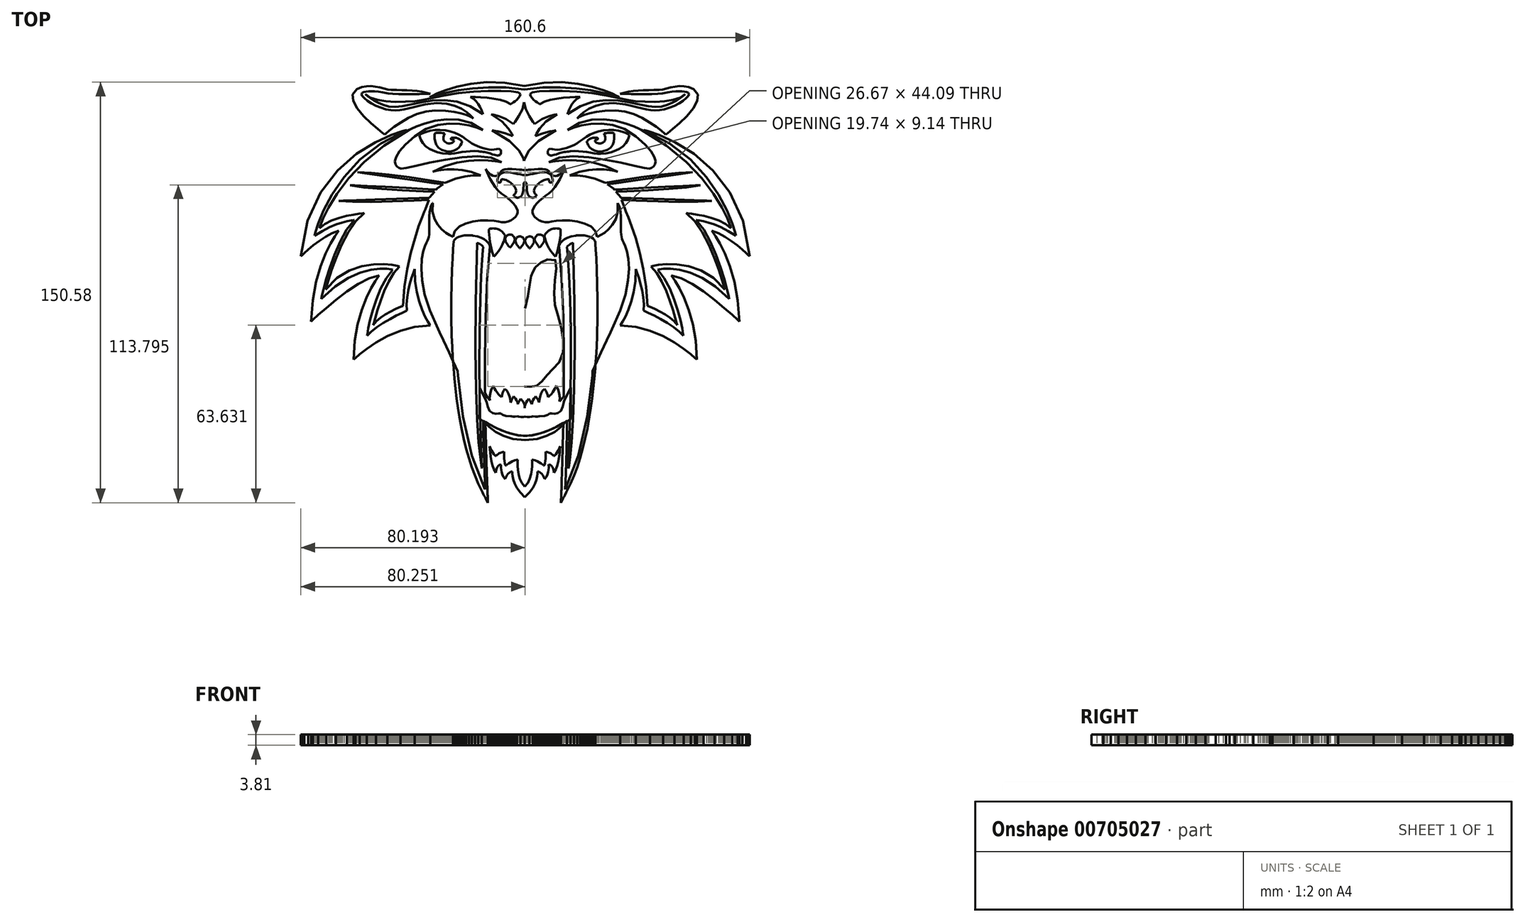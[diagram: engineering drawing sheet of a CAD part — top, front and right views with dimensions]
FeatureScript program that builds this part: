
annotation { "Feature Type Name" : "Feature", "Feature Type Description" : "" }
export const myFeature = defineFeature(function(context is Context, id is Id, definition is map)
    precondition{}
    {
        {
            var Q0;
            Q0=qCreatedBy(makeId("Top.planeOp"),FACE);
            var sketch = newSketch(context, id + "F0", { "sketchPlane" : qUnion([Q0])});
            skLineSegment(sketch, "E0", {"start": v(12.77, -75.29) * mm, "end": v(12.8, -74.69) * mm});
            skLineSegment(sketch, "E1", {"start": v(12.8, -74.69) * mm, "end": v(12.82, -74.1) * mm});
            skLineSegment(sketch, "E2", {"start": v(12.82, -74.1) * mm, "end": v(12.84, -73.5) * mm});
            skLineSegment(sketch, "E3", {"start": v(12.84, -73.5) * mm, "end": v(12.87, -72.9) * mm});
            skLineSegment(sketch, "E4", {"start": v(12.87, -72.9) * mm, "end": v(12.9, -72.3) * mm});
            skLineSegment(sketch, "E5", {"start": v(12.9, -72.3) * mm, "end": v(12.92, -71.7) * mm});
            skLineSegment(sketch, "E6", {"start": v(12.92, -71.7) * mm, "end": v(12.94, -71.1) * mm});
            skLineSegment(sketch, "E7", {"start": v(12.94, -71.1) * mm, "end": v(12.97, -70.5) * mm});
            skLineSegment(sketch, "E8", {"start": v(12.97, -70.5) * mm, "end": v(13.08, -67.74) * mm});
            skLineSegment(sketch, "E9", {"start": v(13.08, -67.74) * mm, "end": v(13.31, -60.6) * mm});
            skLineSegment(sketch, "E10", {"start": v(13.31, -60.6) * mm, "end": v(13.58, -50.1) * mm});
            skLineSegment(sketch, "E11", {"start": v(13.58, -50.1) * mm, "end": v(13.79, -37.28) * mm});
            skLineSegment(sketch, "E12", {"start": v(13.79, -37.28) * mm, "end": v(13.84, -23.18) * mm});
            skLineSegment(sketch, "E13", {"start": v(13.84, -23.18) * mm, "end": v(13.63, -8.86) * mm});
            skLineSegment(sketch, "E14", {"start": v(13.63, -8.86) * mm, "end": v(13.07, 4.68) * mm});
            skLineSegment(sketch, "E15", {"start": v(13.07, 4.68) * mm, "end": v(12.07, 16.37) * mm});
            skLineSegment(sketch, "E16", {"start": v(12.07, 16.37) * mm, "end": v(12.06, 16.4) * mm});
            skLineSegment(sketch, "E17", {"start": v(12.06, 16.4) * mm, "end": v(12.06, 16.43) * mm});
            skLineSegment(sketch, "E18", {"start": v(12.06, 16.43) * mm, "end": v(12.06, 16.46) * mm});
            skLineSegment(sketch, "E19", {"start": v(12.06, 16.46) * mm, "end": v(12.05, 16.49) * mm});
            skLineSegment(sketch, "E20", {"start": v(12.05, 16.49) * mm, "end": v(12.05, 16.52) * mm});
            skLineSegment(sketch, "E21", {"start": v(12.05, 16.52) * mm, "end": v(12.04, 16.54) * mm});
            skLineSegment(sketch, "E22", {"start": v(12.04, 16.54) * mm, "end": v(12.04, 16.57) * mm});
            skLineSegment(sketch, "E23", {"start": v(12.04, 16.57) * mm, "end": v(12.04, 16.6) * mm});
            skLineSegment(sketch, "E24", {"start": v(12.04, 16.6) * mm, "end": v(12.05, 16.63) * mm});
            skLineSegment(sketch, "E25", {"start": v(12.05, 16.63) * mm, "end": v(12.06, 16.66) * mm});
            skLineSegment(sketch, "E26", {"start": v(12.06, 16.66) * mm, "end": v(12.06, 16.69) * mm});
            skLineSegment(sketch, "E27", {"start": v(12.06, 16.69) * mm, "end": v(12.07, 16.71) * mm});
            skLineSegment(sketch, "E28", {"start": v(12.07, 16.71) * mm, "end": v(12.08, 16.74) * mm});
            skLineSegment(sketch, "E29", {"start": v(12.08, 16.74) * mm, "end": v(12.1, 16.77) * mm});
            skLineSegment(sketch, "E30", {"start": v(12.1, 16.77) * mm, "end": v(12.1, 16.8) * mm});
            skLineSegment(sketch, "E31", {"start": v(12.1, 16.8) * mm, "end": v(12.1, 16.82) * mm});
            skLineSegment(sketch, "E32", {"start": v(12.1, 16.82) * mm, "end": v(12.2, 17.03) * mm});
            skLineSegment(sketch, "E33", {"start": v(12.2, 17.03) * mm, "end": v(12.4, 17.4) * mm});
            skLineSegment(sketch, "E34", {"start": v(12.4, 17.4) * mm, "end": v(12.74, 17.88) * mm});
            skLineSegment(sketch, "E35", {"start": v(12.74, 17.88) * mm, "end": v(13.29, 18.43) * mm});
            skLineSegment(sketch, "E36", {"start": v(13.29, 18.43) * mm, "end": v(14.06, 19) * mm});
            skLineSegment(sketch, "E37", {"start": v(14.06, 19) * mm, "end": v(15.09, 19.54) * mm});
            skLineSegment(sketch, "E38", {"start": v(15.09, 19.54) * mm, "end": v(16.42, 20) * mm});
            skLineSegment(sketch, "E39", {"start": v(16.42, 20) * mm, "end": v(18.09, 20.35) * mm});
            skLineSegment(sketch, "E40", {"start": v(18.09, 20.35) * mm, "end": v(18.34, 20.38) * mm});
            skLineSegment(sketch, "E41", {"start": v(18.34, 20.38) * mm, "end": v(18.6, 20.41) * mm});
            skLineSegment(sketch, "E42", {"start": v(18.6, 20.41) * mm, "end": v(18.84, 20.44) * mm});
            skLineSegment(sketch, "E43", {"start": v(18.84, 20.44) * mm, "end": v(19.08, 20.46) * mm});
            skLineSegment(sketch, "E44", {"start": v(19.08, 20.46) * mm, "end": v(19.32, 20.47) * mm});
            skLineSegment(sketch, "E45", {"start": v(19.32, 20.47) * mm, "end": v(19.56, 20.49) * mm});
            skLineSegment(sketch, "E46", {"start": v(19.56, 20.49) * mm, "end": v(19.8, 20.5) * mm});
            skLineSegment(sketch, "E47", {"start": v(19.8, 20.5) * mm, "end": v(20.02, 20.5) * mm});
            skLineSegment(sketch, "E48", {"start": v(20.02, 20.5) * mm, "end": v(21.18, 20.43) * mm});
            skLineSegment(sketch, "E49", {"start": v(21.18, 20.43) * mm, "end": v(22.18, 20.25) * mm});
            skLineSegment(sketch, "E50", {"start": v(22.18, 20.25) * mm, "end": v(23.03, 19.98) * mm});
            skLineSegment(sketch, "E51", {"start": v(23.03, 19.98) * mm, "end": v(23.74, 19.63) * mm});
            skLineSegment(sketch, "E52", {"start": v(23.74, 19.63) * mm, "end": v(24.29, 19.24) * mm});
            skLineSegment(sketch, "E53", {"start": v(24.29, 19.24) * mm, "end": v(24.69, 18.83) * mm});
            skLineSegment(sketch, "E54", {"start": v(24.69, 18.83) * mm, "end": v(24.94, 18.42) * mm});
            skLineSegment(sketch, "E55", {"start": v(24.94, 18.42) * mm, "end": v(25.04, 18.02) * mm});
            skLineSegment(sketch, "E56", {"start": v(25.04, 18.02) * mm, "end": v(25.1, 17.3) * mm});
            skLineSegment(sketch, "E57", {"start": v(25.1, 17.3) * mm, "end": v(25.24, 15.31) * mm});
            skLineSegment(sketch, "E58", {"start": v(25.24, 15.31) * mm, "end": v(25.42, 12.2) * mm});
            skLineSegment(sketch, "E59", {"start": v(25.42, 12.2) * mm, "end": v(25.6, 8.12) * mm});
            skLineSegment(sketch, "E60", {"start": v(25.6, 8.12) * mm, "end": v(25.76, 3.17) * mm});
            skLineSegment(sketch, "E61", {"start": v(25.76, 3.17) * mm, "end": v(25.85, -2.49) * mm});
            skLineSegment(sketch, "E62", {"start": v(25.85, -2.49) * mm, "end": v(25.84, -8.74) * mm});
            skLineSegment(sketch, "E63", {"start": v(25.84, -8.74) * mm, "end": v(25.7, -15.43) * mm});
            skLineSegment(sketch, "E64", {"start": v(25.7, -15.43) * mm, "end": v(25.54, -19.43) * mm});
            skLineSegment(sketch, "E65", {"start": v(25.54, -19.43) * mm, "end": v(25.32, -23.33) * mm});
            skLineSegment(sketch, "E66", {"start": v(25.32, -23.33) * mm, "end": v(25.06, -27.14) * mm});
            skLineSegment(sketch, "E67", {"start": v(25.06, -27.14) * mm, "end": v(24.74, -30.85) * mm});
            skLineSegment(sketch, "E68", {"start": v(24.74, -30.85) * mm, "end": v(24.37, -34.46) * mm});
            skLineSegment(sketch, "E69", {"start": v(24.37, -34.46) * mm, "end": v(23.95, -37.96) * mm});
            skLineSegment(sketch, "E70", {"start": v(23.95, -37.96) * mm, "end": v(23.48, -41.35) * mm});
            skLineSegment(sketch, "E71", {"start": v(23.48, -41.35) * mm, "end": v(22.96, -44.63) * mm});
            skLineSegment(sketch, "E72", {"start": v(22.96, -44.63) * mm, "end": v(22.24, -48.58) * mm});
            skLineSegment(sketch, "E73", {"start": v(22.24, -48.58) * mm, "end": v(21.43, -52.36) * mm});
            skLineSegment(sketch, "E74", {"start": v(21.43, -52.36) * mm, "end": v(20.54, -55.95) * mm});
            skLineSegment(sketch, "E75", {"start": v(20.54, -55.95) * mm, "end": v(19.58, -59.35) * mm});
            skLineSegment(sketch, "E76", {"start": v(19.58, -59.35) * mm, "end": v(18.54, -62.56) * mm});
            skLineSegment(sketch, "E77", {"start": v(18.54, -62.56) * mm, "end": v(17.42, -65.58) * mm});
            skLineSegment(sketch, "E78", {"start": v(17.42, -65.58) * mm, "end": v(16.23, -68.4) * mm});
            skLineSegment(sketch, "E79", {"start": v(16.23, -68.4) * mm, "end": v(14.96, -71.03) * mm});
            skLineSegment(sketch, "E80", {"start": v(14.96, -71.03) * mm, "end": v(14.69, -71.56) * mm});
            skLineSegment(sketch, "E81", {"start": v(14.69, -71.56) * mm, "end": v(14.41, -72.1) * mm});
            skLineSegment(sketch, "E82", {"start": v(14.41, -72.1) * mm, "end": v(14.14, -72.63) * mm});
            skLineSegment(sketch, "E83", {"start": v(14.14, -72.63) * mm, "end": v(13.87, -73.16) * mm});
            skLineSegment(sketch, "E84", {"start": v(13.87, -73.16) * mm, "end": v(13.6, -73.7) * mm});
            skLineSegment(sketch, "E85", {"start": v(13.6, -73.7) * mm, "end": v(13.32, -74.22) * mm});
            skLineSegment(sketch, "E86", {"start": v(13.32, -74.22) * mm, "end": v(13.04, -74.76) * mm});
            skLineSegment(sketch, "E87", {"start": v(13.04, -74.76) * mm, "end": v(12.77, -75.29) * mm});
            skLineSegment(sketch, "E88", {"start": v(14.2, 16.3) * mm, "end": v(15.05, 6.8) * mm});
            skLineSegment(sketch, "E89", {"start": v(15.05, 6.8) * mm, "end": v(15.6, -4.05) * mm});
            skLineSegment(sketch, "E90", {"start": v(15.6, -4.05) * mm, "end": v(15.88, -15.66) * mm});
            skLineSegment(sketch, "E91", {"start": v(15.88, -15.66) * mm, "end": v(15.96, -27.46) * mm});
            skLineSegment(sketch, "E92", {"start": v(15.96, -27.46) * mm, "end": v(15.88, -38.9) * mm});
            skLineSegment(sketch, "E93", {"start": v(15.88, -38.9) * mm, "end": v(15.71, -49.38) * mm});
            skLineSegment(sketch, "E94", {"start": v(15.71, -49.38) * mm, "end": v(15.5, -58.35) * mm});
            skLineSegment(sketch, "E95", {"start": v(15.5, -58.35) * mm, "end": v(15.28, -65.25) * mm});
            skLineSegment(sketch, "E96", {"start": v(15.28, -65.25) * mm, "end": v(16.97, -60.57) * mm});
            skLineSegment(sketch, "E97", {"start": v(16.97, -60.57) * mm, "end": v(18.48, -55.42) * mm});
            skLineSegment(sketch, "E98", {"start": v(18.48, -55.42) * mm, "end": v(19.81, -49.8) * mm});
            skLineSegment(sketch, "E99", {"start": v(19.81, -49.8) * mm, "end": v(20.95, -43.74) * mm});
            skLineSegment(sketch, "E100", {"start": v(20.95, -43.74) * mm, "end": v(21.9, -37.25) * mm});
            skLineSegment(sketch, "E101", {"start": v(21.9, -37.25) * mm, "end": v(22.66, -30.35) * mm});
            skLineSegment(sketch, "E102", {"start": v(22.66, -30.35) * mm, "end": v(23.22, -23.04) * mm});
            skLineSegment(sketch, "E103", {"start": v(23.22, -23.04) * mm, "end": v(23.58, -15.36) * mm});
            skLineSegment(sketch, "E104", {"start": v(23.58, -15.36) * mm, "end": v(23.73, -9.17) * mm});
            skLineSegment(sketch, "E105", {"start": v(23.73, -9.17) * mm, "end": v(23.75, -3.37) * mm});
            skLineSegment(sketch, "E106", {"start": v(23.75, -3.37) * mm, "end": v(23.68, 1.96) * mm});
            skLineSegment(sketch, "E107", {"start": v(23.68, 1.96) * mm, "end": v(23.54, 6.7) * mm});
            skLineSegment(sketch, "E108", {"start": v(23.54, 6.7) * mm, "end": v(23.37, 10.73) * mm});
            skLineSegment(sketch, "E109", {"start": v(23.37, 10.73) * mm, "end": v(23.2, 13.96) * mm});
            skLineSegment(sketch, "E110", {"start": v(23.2, 13.96) * mm, "end": v(23.05, 16.29) * mm});
            skLineSegment(sketch, "E111", {"start": v(23.05, 16.29) * mm, "end": v(22.96, 17.6) * mm});
            skLineSegment(sketch, "E112", {"start": v(22.96, 17.6) * mm, "end": v(22.84, 17.7) * mm});
            skLineSegment(sketch, "E113", {"start": v(22.84, 17.7) * mm, "end": v(22.67, 17.8) * mm});
            skLineSegment(sketch, "E114", {"start": v(22.67, 17.8) * mm, "end": v(22.43, 17.94) * mm});
            skLineSegment(sketch, "E115", {"start": v(22.43, 17.94) * mm, "end": v(22.11, 18.07) * mm});
            skLineSegment(sketch, "E116", {"start": v(22.11, 18.07) * mm, "end": v(21.72, 18.19) * mm});
            skLineSegment(sketch, "E117", {"start": v(21.72, 18.19) * mm, "end": v(21.25, 18.29) * mm});
            skLineSegment(sketch, "E118", {"start": v(21.25, 18.29) * mm, "end": v(20.68, 18.36) * mm});
            skLineSegment(sketch, "E119", {"start": v(20.68, 18.36) * mm, "end": v(20.02, 18.38) * mm});
            skLineSegment(sketch, "E120", {"start": v(20.02, 18.38) * mm, "end": v(19.83, 18.38) * mm});
            skLineSegment(sketch, "E121", {"start": v(19.83, 18.38) * mm, "end": v(19.63, 18.37) * mm});
            skLineSegment(sketch, "E122", {"start": v(19.63, 18.37) * mm, "end": v(19.43, 18.36) * mm});
            skLineSegment(sketch, "E123", {"start": v(19.43, 18.36) * mm, "end": v(19.23, 18.35) * mm});
            skLineSegment(sketch, "E124", {"start": v(19.23, 18.35) * mm, "end": v(19.02, 18.33) * mm});
            skLineSegment(sketch, "E125", {"start": v(19.02, 18.33) * mm, "end": v(18.81, 18.31) * mm});
            skLineSegment(sketch, "E126", {"start": v(18.81, 18.31) * mm, "end": v(18.6, 18.29) * mm});
            skLineSegment(sketch, "E127", {"start": v(18.6, 18.29) * mm, "end": v(18.38, 18.26) * mm});
            skLineSegment(sketch, "E128", {"start": v(18.38, 18.26) * mm, "end": v(17.38, 18.07) * mm});
            skLineSegment(sketch, "E129", {"start": v(17.38, 18.07) * mm, "end": v(16.55, 17.84) * mm});
            skLineSegment(sketch, "E130", {"start": v(16.55, 17.84) * mm, "end": v(15.86, 17.57) * mm});
            skLineSegment(sketch, "E131", {"start": v(15.86, 17.57) * mm, "end": v(15.31, 17.28) * mm});
            skLineSegment(sketch, "E132", {"start": v(15.31, 17.28) * mm, "end": v(14.88, 17) * mm});
            skLineSegment(sketch, "E133", {"start": v(14.88, 17) * mm, "end": v(14.57, 16.73) * mm});
            skLineSegment(sketch, "E134", {"start": v(14.57, 16.73) * mm, "end": v(14.34, 16.5) * mm});
            skLineSegment(sketch, "E135", {"start": v(14.34, 16.5) * mm, "end": v(14.2, 16.3) * mm});
            skLineSegment(sketch, "E136", {"start": v(-16.27, -43.5) * mm, "end": v(-16.09, -43.9) * mm});
            skLineSegment(sketch, "E137", {"start": v(-16.09, -43.9) * mm, "end": v(-15.49, -44.96) * mm});
            skLineSegment(sketch, "E138", {"start": v(-15.49, -44.96) * mm, "end": v(-14.42, -46.45) * mm});
            skLineSegment(sketch, "E139", {"start": v(-14.42, -46.45) * mm, "end": v(-12.83, -48.16) * mm});
            skLineSegment(sketch, "E140", {"start": v(-12.83, -48.16) * mm, "end": v(-10.66, -49.87) * mm});
            skLineSegment(sketch, "E141", {"start": v(-10.66, -49.87) * mm, "end": v(-7.84, -51.36) * mm});
            skLineSegment(sketch, "E142", {"start": v(-7.84, -51.36) * mm, "end": v(-4.32, -52.41) * mm});
            skLineSegment(sketch, "E143", {"start": v(-4.32, -52.41) * mm, "end": v(-0.05, -52.81) * mm});
            skLineSegment(sketch, "E144", {"start": v(-0.05, -52.81) * mm, "end": v(4.23, -52.41) * mm});
            skLineSegment(sketch, "E145", {"start": v(4.23, -52.41) * mm, "end": v(7.74, -51.36) * mm});
            skLineSegment(sketch, "E146", {"start": v(7.74, -51.36) * mm, "end": v(10.56, -49.87) * mm});
            skLineSegment(sketch, "E147", {"start": v(10.56, -49.87) * mm, "end": v(12.74, -48.16) * mm});
            skLineSegment(sketch, "E148", {"start": v(12.74, -48.16) * mm, "end": v(14.33, -46.45) * mm});
            skLineSegment(sketch, "E149", {"start": v(14.33, -46.45) * mm, "end": v(15.4, -44.96) * mm});
            skLineSegment(sketch, "E150", {"start": v(15.4, -44.96) * mm, "end": v(15.99, -43.9) * mm});
            skLineSegment(sketch, "E151", {"start": v(15.99, -43.9) * mm, "end": v(16.17, -43.5) * mm});
            skLineSegment(sketch, "E152", {"start": v(16.17, -43.5) * mm, "end": v(12.12, -43.5) * mm});
            skLineSegment(sketch, "E153", {"start": v(12.12, -43.5) * mm, "end": v(8.06, -43.5) * mm});
            skLineSegment(sketch, "E154", {"start": v(8.06, -43.5) * mm, "end": v(4, -43.5) * mm});
            skLineSegment(sketch, "E155", {"start": v(4, -43.5) * mm, "end": v(-0.05, -43.5) * mm});
            skLineSegment(sketch, "E156", {"start": v(-0.05, -43.5) * mm, "end": v(-4.1, -43.5) * mm});
            skLineSegment(sketch, "E157", {"start": v(-4.1, -43.5) * mm, "end": v(-8.16, -43.5) * mm});
            skLineSegment(sketch, "E158", {"start": v(-8.16, -43.5) * mm, "end": v(-12.22, -43.5) * mm});
            skLineSegment(sketch, "E159", {"start": v(-12.22, -43.5) * mm, "end": v(-16.27, -43.5) * mm});
            skLineSegment(sketch, "E160", {"start": v(-13.36, -75.29) * mm, "end": v(-13.64, -74.76) * mm});
            skLineSegment(sketch, "E161", {"start": v(-13.64, -74.76) * mm, "end": v(-13.9, -74.22) * mm});
            skLineSegment(sketch, "E162", {"start": v(-13.9, -74.22) * mm, "end": v(-14.18, -73.7) * mm});
            skLineSegment(sketch, "E163", {"start": v(-14.18, -73.7) * mm, "end": v(-14.46, -73.16) * mm});
            skLineSegment(sketch, "E164", {"start": v(-14.46, -73.16) * mm, "end": v(-14.73, -72.63) * mm});
            skLineSegment(sketch, "E165", {"start": v(-14.73, -72.63) * mm, "end": v(-15, -72.1) * mm});
            skLineSegment(sketch, "E166", {"start": v(-15, -72.1) * mm, "end": v(-15.28, -71.56) * mm});
            skLineSegment(sketch, "E167", {"start": v(-15.28, -71.56) * mm, "end": v(-15.56, -71.03) * mm});
            skLineSegment(sketch, "E168", {"start": v(-15.56, -71.03) * mm, "end": v(-16.83, -68.4) * mm});
            skLineSegment(sketch, "E169", {"start": v(-16.83, -68.4) * mm, "end": v(-18.02, -65.58) * mm});
            skLineSegment(sketch, "E170", {"start": v(-18.02, -65.58) * mm, "end": v(-19.13, -62.56) * mm});
            skLineSegment(sketch, "E171", {"start": v(-19.13, -62.56) * mm, "end": v(-20.18, -59.35) * mm});
            skLineSegment(sketch, "E172", {"start": v(-20.18, -59.35) * mm, "end": v(-21.14, -55.95) * mm});
            skLineSegment(sketch, "E173", {"start": v(-21.14, -55.95) * mm, "end": v(-22.02, -52.36) * mm});
            skLineSegment(sketch, "E174", {"start": v(-22.02, -52.36) * mm, "end": v(-22.83, -48.58) * mm});
            skLineSegment(sketch, "E175", {"start": v(-22.83, -48.58) * mm, "end": v(-23.56, -44.63) * mm});
            skLineSegment(sketch, "E176", {"start": v(-23.56, -44.63) * mm, "end": v(-24.08, -41.35) * mm});
            skLineSegment(sketch, "E177", {"start": v(-24.08, -41.35) * mm, "end": v(-24.55, -37.96) * mm});
            skLineSegment(sketch, "E178", {"start": v(-24.55, -37.96) * mm, "end": v(-24.97, -34.46) * mm});
            skLineSegment(sketch, "E179", {"start": v(-24.97, -34.46) * mm, "end": v(-25.34, -30.85) * mm});
            skLineSegment(sketch, "E180", {"start": v(-25.34, -30.85) * mm, "end": v(-25.65, -27.14) * mm});
            skLineSegment(sketch, "E181", {"start": v(-25.65, -27.14) * mm, "end": v(-25.92, -23.33) * mm});
            skLineSegment(sketch, "E182", {"start": v(-25.92, -23.33) * mm, "end": v(-26.13, -19.43) * mm});
            skLineSegment(sketch, "E183", {"start": v(-26.13, -19.43) * mm, "end": v(-26.3, -15.43) * mm});
            skLineSegment(sketch, "E184", {"start": v(-26.3, -15.43) * mm, "end": v(-26.44, -8.74) * mm});
            skLineSegment(sketch, "E185", {"start": v(-26.44, -8.74) * mm, "end": v(-26.45, -2.49) * mm});
            skLineSegment(sketch, "E186", {"start": v(-26.45, -2.49) * mm, "end": v(-26.35, 3.17) * mm});
            skLineSegment(sketch, "E187", {"start": v(-26.35, 3.17) * mm, "end": v(-26.2, 8.12) * mm});
            skLineSegment(sketch, "E188", {"start": v(-26.2, 8.12) * mm, "end": v(-26, 12.21) * mm});
            skLineSegment(sketch, "E189", {"start": v(-26, 12.21) * mm, "end": v(-25.83, 15.32) * mm});
            skLineSegment(sketch, "E190", {"start": v(-25.83, 15.32) * mm, "end": v(-25.7, 17.3) * mm});
            skLineSegment(sketch, "E191", {"start": v(-25.7, 17.3) * mm, "end": v(-25.64, 18.03) * mm});
            skLineSegment(sketch, "E192", {"start": v(-25.64, 18.03) * mm, "end": v(-25.53, 18.42) * mm});
            skLineSegment(sketch, "E193", {"start": v(-25.53, 18.42) * mm, "end": v(-25.28, 18.83) * mm});
            skLineSegment(sketch, "E194", {"start": v(-25.28, 18.83) * mm, "end": v(-24.88, 19.24) * mm});
            skLineSegment(sketch, "E195", {"start": v(-24.88, 19.24) * mm, "end": v(-24.33, 19.63) * mm});
            skLineSegment(sketch, "E196", {"start": v(-24.33, 19.63) * mm, "end": v(-23.63, 19.98) * mm});
            skLineSegment(sketch, "E197", {"start": v(-23.63, 19.98) * mm, "end": v(-22.78, 20.25) * mm});
            skLineSegment(sketch, "E198", {"start": v(-22.78, 20.25) * mm, "end": v(-21.77, 20.43) * mm});
            skLineSegment(sketch, "E199", {"start": v(-21.77, 20.43) * mm, "end": v(-20.62, 20.5) * mm});
            skLineSegment(sketch, "E200", {"start": v(-20.62, 20.5) * mm, "end": v(-20.39, 20.5) * mm});
            skLineSegment(sketch, "E201", {"start": v(-20.39, 20.5) * mm, "end": v(-20.15, 20.49) * mm});
            skLineSegment(sketch, "E202", {"start": v(-20.15, 20.49) * mm, "end": v(-19.92, 20.47) * mm});
            skLineSegment(sketch, "E203", {"start": v(-19.92, 20.47) * mm, "end": v(-19.68, 20.46) * mm});
            skLineSegment(sketch, "E204", {"start": v(-19.68, 20.46) * mm, "end": v(-19.43, 20.44) * mm});
            skLineSegment(sketch, "E205", {"start": v(-19.43, 20.44) * mm, "end": v(-19.18, 20.41) * mm});
            skLineSegment(sketch, "E206", {"start": v(-19.18, 20.41) * mm, "end": v(-18.93, 20.38) * mm});
            skLineSegment(sketch, "E207", {"start": v(-18.93, 20.38) * mm, "end": v(-18.68, 20.35) * mm});
            skLineSegment(sketch, "E208", {"start": v(-18.68, 20.35) * mm, "end": v(-17.02, 20) * mm});
            skLineSegment(sketch, "E209", {"start": v(-17.02, 20) * mm, "end": v(-15.68, 19.54) * mm});
            skLineSegment(sketch, "E210", {"start": v(-15.68, 19.54) * mm, "end": v(-14.65, 19) * mm});
            skLineSegment(sketch, "E211", {"start": v(-14.65, 19) * mm, "end": v(-13.88, 18.43) * mm});
            skLineSegment(sketch, "E212", {"start": v(-13.88, 18.43) * mm, "end": v(-13.34, 17.88) * mm});
            skLineSegment(sketch, "E213", {"start": v(-13.34, 17.88) * mm, "end": v(-12.99, 17.4) * mm});
            skLineSegment(sketch, "E214", {"start": v(-12.99, 17.4) * mm, "end": v(-12.79, 17.03) * mm});
            skLineSegment(sketch, "E215", {"start": v(-12.79, 17.03) * mm, "end": v(-12.7, 16.82) * mm});
            skLineSegment(sketch, "E216", {"start": v(-12.7, 16.82) * mm, "end": v(-12.7, 16.8) * mm});
            skLineSegment(sketch, "E217", {"start": v(-12.7, 16.8) * mm, "end": v(-12.69, 16.77) * mm});
            skLineSegment(sketch, "E218", {"start": v(-12.69, 16.77) * mm, "end": v(-12.68, 16.74) * mm});
            skLineSegment(sketch, "E219", {"start": v(-12.68, 16.74) * mm, "end": v(-12.67, 16.71) * mm});
            skLineSegment(sketch, "E220", {"start": v(-12.67, 16.71) * mm, "end": v(-12.66, 16.69) * mm});
            skLineSegment(sketch, "E221", {"start": v(-12.66, 16.69) * mm, "end": v(-12.65, 16.66) * mm});
            skLineSegment(sketch, "E222", {"start": v(-12.65, 16.66) * mm, "end": v(-12.64, 16.63) * mm});
            skLineSegment(sketch, "E223", {"start": v(-12.64, 16.63) * mm, "end": v(-12.63, 16.6) * mm});
            skLineSegment(sketch, "E224", {"start": v(-12.63, 16.6) * mm, "end": v(-12.64, 16.57) * mm});
            skLineSegment(sketch, "E225", {"start": v(-12.64, 16.57) * mm, "end": v(-12.64, 16.54) * mm});
            skLineSegment(sketch, "E226", {"start": v(-12.64, 16.54) * mm, "end": v(-12.64, 16.52) * mm});
            skLineSegment(sketch, "E227", {"start": v(-12.64, 16.52) * mm, "end": v(-12.65, 16.49) * mm});
            skLineSegment(sketch, "E228", {"start": v(-12.65, 16.49) * mm, "end": v(-12.65, 16.46) * mm});
            skLineSegment(sketch, "E229", {"start": v(-12.65, 16.46) * mm, "end": v(-12.65, 16.43) * mm});
            skLineSegment(sketch, "E230", {"start": v(-12.65, 16.43) * mm, "end": v(-12.66, 16.4) * mm});
            skLineSegment(sketch, "E231", {"start": v(-12.66, 16.4) * mm, "end": v(-12.66, 16.37) * mm});
            skLineSegment(sketch, "E232", {"start": v(-12.66, 16.37) * mm, "end": v(-13.67, 4.68) * mm});
            skLineSegment(sketch, "E233", {"start": v(-13.67, 4.68) * mm, "end": v(-14.22, -8.86) * mm});
            skLineSegment(sketch, "E234", {"start": v(-14.22, -8.86) * mm, "end": v(-14.43, -23.18) * mm});
            skLineSegment(sketch, "E235", {"start": v(-14.43, -23.18) * mm, "end": v(-14.38, -37.28) * mm});
            skLineSegment(sketch, "E236", {"start": v(-14.38, -37.28) * mm, "end": v(-14.18, -50.1) * mm});
            skLineSegment(sketch, "E237", {"start": v(-14.18, -50.1) * mm, "end": v(-13.9, -60.6) * mm});
            skLineSegment(sketch, "E238", {"start": v(-13.9, -60.6) * mm, "end": v(-13.67, -67.74) * mm});
            skLineSegment(sketch, "E239", {"start": v(-13.67, -67.74) * mm, "end": v(-13.56, -70.5) * mm});
            skLineSegment(sketch, "E240", {"start": v(-13.56, -70.5) * mm, "end": v(-13.54, -71.1) * mm});
            skLineSegment(sketch, "E241", {"start": v(-13.54, -71.1) * mm, "end": v(-13.51, -71.7) * mm});
            skLineSegment(sketch, "E242", {"start": v(-13.51, -71.7) * mm, "end": v(-13.49, -72.3) * mm});
            skLineSegment(sketch, "E243", {"start": v(-13.49, -72.3) * mm, "end": v(-13.46, -72.9) * mm});
            skLineSegment(sketch, "E244", {"start": v(-13.46, -72.9) * mm, "end": v(-13.44, -73.5) * mm});
            skLineSegment(sketch, "E245", {"start": v(-13.44, -73.5) * mm, "end": v(-13.41, -74.1) * mm});
            skLineSegment(sketch, "E246", {"start": v(-13.41, -74.1) * mm, "end": v(-13.39, -74.69) * mm});
            skLineSegment(sketch, "E247", {"start": v(-13.39, -74.69) * mm, "end": v(-13.36, -75.29) * mm});
            skLineSegment(sketch, "E248", {"start": v(-23.55, 17.6) * mm, "end": v(-23.65, 16.28) * mm});
            skLineSegment(sketch, "E249", {"start": v(-23.65, 16.28) * mm, "end": v(-23.8, 13.95) * mm});
            skLineSegment(sketch, "E250", {"start": v(-23.8, 13.95) * mm, "end": v(-23.97, 10.71) * mm});
            skLineSegment(sketch, "E251", {"start": v(-23.97, 10.71) * mm, "end": v(-24.14, 6.67) * mm});
            skLineSegment(sketch, "E252", {"start": v(-24.14, 6.67) * mm, "end": v(-24.27, 1.94) * mm});
            skLineSegment(sketch, "E253", {"start": v(-24.27, 1.94) * mm, "end": v(-24.34, -3.4) * mm});
            skLineSegment(sketch, "E254", {"start": v(-24.34, -3.4) * mm, "end": v(-24.32, -9.2) * mm});
            skLineSegment(sketch, "E255", {"start": v(-24.32, -9.2) * mm, "end": v(-24.18, -15.39) * mm});
            skLineSegment(sketch, "E256", {"start": v(-24.18, -15.39) * mm, "end": v(-23.82, -23.06) * mm});
            skLineSegment(sketch, "E257", {"start": v(-23.82, -23.06) * mm, "end": v(-23.26, -30.36) * mm});
            skLineSegment(sketch, "E258", {"start": v(-23.26, -30.36) * mm, "end": v(-22.5, -37.26) * mm});
            skLineSegment(sketch, "E259", {"start": v(-22.5, -37.26) * mm, "end": v(-21.55, -43.75) * mm});
            skLineSegment(sketch, "E260", {"start": v(-21.55, -43.75) * mm, "end": v(-20.4, -49.8) * mm});
            skLineSegment(sketch, "E261", {"start": v(-20.4, -49.8) * mm, "end": v(-19.08, -55.42) * mm});
            skLineSegment(sketch, "E262", {"start": v(-19.08, -55.42) * mm, "end": v(-17.57, -60.57) * mm});
            skLineSegment(sketch, "E263", {"start": v(-17.57, -60.57) * mm, "end": v(-15.87, -65.25) * mm});
            skLineSegment(sketch, "E264", {"start": v(-15.87, -65.25) * mm, "end": v(-16.08, -58.35) * mm});
            skLineSegment(sketch, "E265", {"start": v(-16.08, -58.35) * mm, "end": v(-16.3, -49.38) * mm});
            skLineSegment(sketch, "E266", {"start": v(-16.3, -49.38) * mm, "end": v(-16.48, -38.9) * mm});
            skLineSegment(sketch, "E267", {"start": v(-16.48, -38.9) * mm, "end": v(-16.55, -27.46) * mm});
            skLineSegment(sketch, "E268", {"start": v(-16.55, -27.46) * mm, "end": v(-16.47, -15.66) * mm});
            skLineSegment(sketch, "E269", {"start": v(-16.47, -15.66) * mm, "end": v(-16.19, -4.05) * mm});
            skLineSegment(sketch, "E270", {"start": v(-16.19, -4.05) * mm, "end": v(-15.65, 6.8) * mm});
            skLineSegment(sketch, "E271", {"start": v(-15.65, 6.8) * mm, "end": v(-14.8, 16.3) * mm});
            skLineSegment(sketch, "E272", {"start": v(-14.8, 16.3) * mm, "end": v(-14.94, 16.5) * mm});
            skLineSegment(sketch, "E273", {"start": v(-14.94, 16.5) * mm, "end": v(-15.16, 16.73) * mm});
            skLineSegment(sketch, "E274", {"start": v(-15.16, 16.73) * mm, "end": v(-15.48, 17) * mm});
            skLineSegment(sketch, "E275", {"start": v(-15.48, 17) * mm, "end": v(-15.9, 17.28) * mm});
            skLineSegment(sketch, "E276", {"start": v(-15.9, 17.28) * mm, "end": v(-16.46, 17.57) * mm});
            skLineSegment(sketch, "E277", {"start": v(-16.46, 17.57) * mm, "end": v(-17.14, 17.84) * mm});
            skLineSegment(sketch, "E278", {"start": v(-17.14, 17.84) * mm, "end": v(-17.98, 18.07) * mm});
            skLineSegment(sketch, "E279", {"start": v(-17.98, 18.07) * mm, "end": v(-18.98, 18.26) * mm});
            skLineSegment(sketch, "E280", {"start": v(-18.98, 18.26) * mm, "end": v(-19.2, 18.29) * mm});
            skLineSegment(sketch, "E281", {"start": v(-19.2, 18.29) * mm, "end": v(-19.4, 18.31) * mm});
            skLineSegment(sketch, "E282", {"start": v(-19.4, 18.31) * mm, "end": v(-19.62, 18.33) * mm});
            skLineSegment(sketch, "E283", {"start": v(-19.62, 18.33) * mm, "end": v(-19.82, 18.35) * mm});
            skLineSegment(sketch, "E284", {"start": v(-19.82, 18.35) * mm, "end": v(-20.03, 18.36) * mm});
            skLineSegment(sketch, "E285", {"start": v(-20.03, 18.36) * mm, "end": v(-20.23, 18.37) * mm});
            skLineSegment(sketch, "E286", {"start": v(-20.23, 18.37) * mm, "end": v(-20.42, 18.38) * mm});
            skLineSegment(sketch, "E287", {"start": v(-20.42, 18.38) * mm, "end": v(-20.62, 18.38) * mm});
            skLineSegment(sketch, "E288", {"start": v(-20.62, 18.38) * mm, "end": v(-21.28, 18.36) * mm});
            skLineSegment(sketch, "E289", {"start": v(-21.28, 18.36) * mm, "end": v(-21.84, 18.29) * mm});
            skLineSegment(sketch, "E290", {"start": v(-21.84, 18.29) * mm, "end": v(-22.32, 18.19) * mm});
            skLineSegment(sketch, "E291", {"start": v(-22.32, 18.19) * mm, "end": v(-22.7, 18.07) * mm});
            skLineSegment(sketch, "E292", {"start": v(-22.7, 18.07) * mm, "end": v(-23.02, 17.94) * mm});
            skLineSegment(sketch, "E293", {"start": v(-23.02, 17.94) * mm, "end": v(-23.26, 17.8) * mm});
            skLineSegment(sketch, "E294", {"start": v(-23.26, 17.8) * mm, "end": v(-23.43, 17.7) * mm});
            skLineSegment(sketch, "E295", {"start": v(-23.43, 17.7) * mm, "end": v(-23.55, 17.6) * mm});
            skLineSegment(sketch, "E296", {"start": v(-0.05, 43.85) * mm, "end": v(-0.03, 43.85) * mm});
            skLineSegment(sketch, "E297", {"start": v(-0.03, 43.85) * mm, "end": v(0.06, 43.84) * mm});
            skLineSegment(sketch, "E298", {"start": v(0.06, 43.84) * mm, "end": v(0.27, 43.84) * mm});
            skLineSegment(sketch, "E299", {"start": v(0.27, 43.84) * mm, "end": v(0.64, 43.86) * mm});
            skLineSegment(sketch, "E300", {"start": v(0.64, 43.86) * mm, "end": v(1.22, 43.89) * mm});
            skLineSegment(sketch, "E301", {"start": v(1.22, 43.89) * mm, "end": v(2.06, 43.95) * mm});
            skLineSegment(sketch, "E302", {"start": v(2.06, 43.95) * mm, "end": v(3.2, 44.04) * mm});
            skLineSegment(sketch, "E303", {"start": v(3.2, 44.04) * mm, "end": v(4.68, 44.17) * mm});
            skLineSegment(sketch, "E304", {"start": v(4.68, 44.17) * mm, "end": v(6.13, 44.22) * mm});
            skLineSegment(sketch, "E305", {"start": v(6.13, 44.22) * mm, "end": v(7.18, 44.08) * mm});
            skLineSegment(sketch, "E306", {"start": v(7.18, 44.08) * mm, "end": v(7.92, 43.8) * mm});
            skLineSegment(sketch, "E307", {"start": v(7.92, 43.8) * mm, "end": v(8.44, 43.4) * mm});
            skLineSegment(sketch, "E308", {"start": v(8.44, 43.4) * mm, "end": v(8.84, 42.97) * mm});
            skLineSegment(sketch, "E309", {"start": v(8.84, 42.97) * mm, "end": v(9.2, 42.52) * mm});
            skLineSegment(sketch, "E310", {"start": v(9.2, 42.52) * mm, "end": v(9.6, 42.1) * mm});
            skLineSegment(sketch, "E311", {"start": v(9.6, 42.1) * mm, "end": v(10.15, 41.77) * mm});
            skLineSegment(sketch, "E312", {"start": v(10.15, 41.77) * mm, "end": v(10.82, 41.66) * mm});
            skLineSegment(sketch, "E313", {"start": v(10.82, 41.66) * mm, "end": v(11.5, 41.83) * mm});
            skLineSegment(sketch, "E314", {"start": v(11.5, 41.83) * mm, "end": v(12.14, 42.2) * mm});
            skLineSegment(sketch, "E315", {"start": v(12.14, 42.2) * mm, "end": v(12.74, 42.7) * mm});
            skLineSegment(sketch, "E316", {"start": v(12.74, 42.7) * mm, "end": v(13.26, 43.22) * mm});
            skLineSegment(sketch, "E317", {"start": v(13.26, 43.22) * mm, "end": v(13.66, 43.7) * mm});
            skLineSegment(sketch, "E318", {"start": v(13.66, 43.7) * mm, "end": v(13.93, 44.04) * mm});
            skLineSegment(sketch, "E319", {"start": v(13.93, 44.04) * mm, "end": v(14.02, 44.17) * mm});
            skLineSegment(sketch, "E320", {"start": v(14.02, 44.17) * mm, "end": v(13.9, 43.88) * mm});
            skLineSegment(sketch, "E321", {"start": v(13.9, 43.88) * mm, "end": v(13.57, 43.1) * mm});
            skLineSegment(sketch, "E322", {"start": v(13.57, 43.1) * mm, "end": v(13.05, 41.94) * mm});
            skLineSegment(sketch, "E323", {"start": v(13.05, 41.94) * mm, "end": v(12.36, 40.57) * mm});
            skLineSegment(sketch, "E324", {"start": v(12.36, 40.57) * mm, "end": v(11.53, 39.1) * mm});
            skLineSegment(sketch, "E325", {"start": v(11.53, 39.1) * mm, "end": v(10.58, 37.67) * mm});
            skLineSegment(sketch, "E326", {"start": v(10.58, 37.67) * mm, "end": v(9.55, 36.42) * mm});
            skLineSegment(sketch, "E327", {"start": v(9.55, 36.42) * mm, "end": v(8.45, 35.47) * mm});
            skLineSegment(sketch, "E328", {"start": v(8.45, 35.47) * mm, "end": v(7.33, 34.69) * mm});
            skLineSegment(sketch, "E329", {"start": v(7.33, 34.69) * mm, "end": v(6.24, 33.84) * mm});
            skLineSegment(sketch, "E330", {"start": v(6.24, 33.84) * mm, "end": v(5.21, 32.94) * mm});
            skLineSegment(sketch, "E331", {"start": v(5.21, 32.94) * mm, "end": v(4.3, 32.03) * mm});
            skLineSegment(sketch, "E332", {"start": v(4.3, 32.03) * mm, "end": v(3.53, 31.12) * mm});
            skLineSegment(sketch, "E333", {"start": v(3.53, 31.12) * mm, "end": v(2.97, 30.23) * mm});
            skLineSegment(sketch, "E334", {"start": v(2.97, 30.23) * mm, "end": v(2.64, 29.38) * mm});
            skLineSegment(sketch, "E335", {"start": v(2.64, 29.38) * mm, "end": v(2.6, 28.6) * mm});
            skLineSegment(sketch, "E336", {"start": v(2.6, 28.6) * mm, "end": v(2.86, 27.84) * mm});
            skLineSegment(sketch, "E337", {"start": v(2.86, 27.84) * mm, "end": v(3.37, 27.1) * mm});
            skLineSegment(sketch, "E338", {"start": v(3.37, 27.1) * mm, "end": v(4.1, 26.42) * mm});
            skLineSegment(sketch, "E339", {"start": v(4.1, 26.42) * mm, "end": v(5, 25.84) * mm});
            skLineSegment(sketch, "E340", {"start": v(5, 25.84) * mm, "end": v(6.02, 25.4) * mm});
            skLineSegment(sketch, "E341", {"start": v(6.02, 25.4) * mm, "end": v(7.14, 25.15) * mm});
            skLineSegment(sketch, "E342", {"start": v(7.14, 25.15) * mm, "end": v(8.31, 25.12) * mm});
            skLineSegment(sketch, "E343", {"start": v(8.31, 25.12) * mm, "end": v(9.49, 25.36) * mm});
            skLineSegment(sketch, "E344", {"start": v(9.49, 25.36) * mm, "end": v(11.07, 25.68) * mm});
            skLineSegment(sketch, "E345", {"start": v(11.07, 25.68) * mm, "end": v(13.3, 25.83) * mm});
            skLineSegment(sketch, "E346", {"start": v(13.3, 25.83) * mm, "end": v(15.92, 25.76) * mm});
            skLineSegment(sketch, "E347", {"start": v(15.92, 25.76) * mm, "end": v(18.66, 25.4) * mm});
            skLineSegment(sketch, "E348", {"start": v(18.66, 25.4) * mm, "end": v(21.28, 24.7) * mm});
            skLineSegment(sketch, "E349", {"start": v(21.28, 24.7) * mm, "end": v(23.5, 23.59) * mm});
            skLineSegment(sketch, "E350", {"start": v(23.5, 23.59) * mm, "end": v(25.05, 22.03) * mm});
            skLineSegment(sketch, "E351", {"start": v(25.05, 22.03) * mm, "end": v(25.7, 19.95) * mm});
            skLineSegment(sketch, "E352", {"start": v(25.7, 19.95) * mm, "end": v(26.06, 20.1) * mm});
            skLineSegment(sketch, "E353", {"start": v(26.06, 20.1) * mm, "end": v(27, 20.56) * mm});
            skLineSegment(sketch, "E354", {"start": v(27, 20.56) * mm, "end": v(28.33, 21.37) * mm});
            skLineSegment(sketch, "E355", {"start": v(28.33, 21.37) * mm, "end": v(29.8, 22.58) * mm});
            skLineSegment(sketch, "E356", {"start": v(29.8, 22.58) * mm, "end": v(31.23, 24.22) * mm});
            skLineSegment(sketch, "E357", {"start": v(31.23, 24.22) * mm, "end": v(32.39, 26.32) * mm});
            skLineSegment(sketch, "E358", {"start": v(32.39, 26.32) * mm, "end": v(33.06, 28.92) * mm});
            skLineSegment(sketch, "E359", {"start": v(33.06, 28.92) * mm, "end": v(33.04, 32.06) * mm});
            skLineSegment(sketch, "E360", {"start": v(33.04, 32.06) * mm, "end": v(33.1, 31.98) * mm});
            skLineSegment(sketch, "E361", {"start": v(33.1, 31.98) * mm, "end": v(33.25, 31.74) * mm});
            skLineSegment(sketch, "E362", {"start": v(33.25, 31.74) * mm, "end": v(33.46, 31.3) * mm});
            skLineSegment(sketch, "E363", {"start": v(33.46, 31.3) * mm, "end": v(33.7, 30.67) * mm});
            skLineSegment(sketch, "E364", {"start": v(33.7, 30.67) * mm, "end": v(33.94, 29.81) * mm});
            skLineSegment(sketch, "E365", {"start": v(33.94, 29.81) * mm, "end": v(34.13, 28.71) * mm});
            skLineSegment(sketch, "E366", {"start": v(34.13, 28.71) * mm, "end": v(34.25, 27.36) * mm});
            skLineSegment(sketch, "E367", {"start": v(34.25, 27.36) * mm, "end": v(34.27, 25.73) * mm});
            skLineSegment(sketch, "E368", {"start": v(34.27, 25.73) * mm, "end": v(34.23, 24.12) * mm});
            skLineSegment(sketch, "E369", {"start": v(34.23, 24.12) * mm, "end": v(34.22, 22.78) * mm});
            skLineSegment(sketch, "E370", {"start": v(34.22, 22.78) * mm, "end": v(34.24, 21.67) * mm});
            skLineSegment(sketch, "E371", {"start": v(34.24, 21.67) * mm, "end": v(34.3, 20.74) * mm});
            skLineSegment(sketch, "E372", {"start": v(34.3, 20.74) * mm, "end": v(34.43, 19.94) * mm});
            skLineSegment(sketch, "E373", {"start": v(34.43, 19.94) * mm, "end": v(34.62, 19.22) * mm});
            skLineSegment(sketch, "E374", {"start": v(34.62, 19.22) * mm, "end": v(34.9, 18.52) * mm});
            skLineSegment(sketch, "E375", {"start": v(34.9, 18.52) * mm, "end": v(35.27, 17.8) * mm});
            skLineSegment(sketch, "E376", {"start": v(35.27, 17.8) * mm, "end": v(35.8, 16.65) * mm});
            skLineSegment(sketch, "E377", {"start": v(35.8, 16.65) * mm, "end": v(36.4, 14.71) * mm});
            skLineSegment(sketch, "E378", {"start": v(36.4, 14.71) * mm, "end": v(36.91, 12) * mm});
            skLineSegment(sketch, "E379", {"start": v(36.91, 12) * mm, "end": v(37.12, 8.52) * mm});
            skLineSegment(sketch, "E380", {"start": v(37.12, 8.52) * mm, "end": v(36.82, 4.26) * mm});
            skLineSegment(sketch, "E381", {"start": v(36.82, 4.26) * mm, "end": v(35.84, -0.75) * mm});
            skLineSegment(sketch, "E382", {"start": v(35.84, -0.75) * mm, "end": v(33.98, -6.53) * mm});
            skLineSegment(sketch, "E383", {"start": v(33.98, -6.53) * mm, "end": v(31.04, -13.05) * mm});
            skLineSegment(sketch, "E384", {"start": v(31.04, -13.05) * mm, "end": v(30.52, -14.19) * mm});
            skLineSegment(sketch, "E385", {"start": v(30.52, -14.19) * mm, "end": v(29.13, -17.2) * mm});
            skLineSegment(sketch, "E386", {"start": v(29.13, -17.2) * mm, "end": v(27.15, -21.52) * mm});
            skLineSegment(sketch, "E387", {"start": v(27.15, -21.52) * mm, "end": v(24.86, -26.57) * mm});
            skLineSegment(sketch, "E388", {"start": v(24.86, -26.57) * mm, "end": v(22.51, -31.77) * mm});
            skLineSegment(sketch, "E389", {"start": v(22.51, -31.77) * mm, "end": v(20.4, -36.55) * mm});
            skLineSegment(sketch, "E390", {"start": v(20.4, -36.55) * mm, "end": v(18.78, -40.34) * mm});
            skLineSegment(sketch, "E391", {"start": v(18.78, -40.34) * mm, "end": v(17.93, -42.56) * mm});
            skLineSegment(sketch, "E392", {"start": v(17.93, -42.56) * mm, "end": v(17.14, -43.88) * mm});
            skLineSegment(sketch, "E393", {"start": v(17.14, -43.88) * mm, "end": v(15.64, -45.33) * mm});
            skLineSegment(sketch, "E394", {"start": v(15.64, -45.33) * mm, "end": v(13.56, -46.8) * mm});
            skLineSegment(sketch, "E395", {"start": v(13.56, -46.8) * mm, "end": v(11.06, -48.2) * mm});
            skLineSegment(sketch, "E396", {"start": v(11.06, -48.2) * mm, "end": v(8.3, -49.44) * mm});
            skLineSegment(sketch, "E397", {"start": v(8.3, -49.44) * mm, "end": v(5.43, -50.44) * mm});
            skLineSegment(sketch, "E398", {"start": v(5.43, -50.44) * mm, "end": v(2.6, -51.1) * mm});
            skLineSegment(sketch, "E399", {"start": v(2.6, -51.1) * mm, "end": v(-0.05, -51.35) * mm});
            skLineSegment(sketch, "E400", {"start": v(-0.05, -51.35) * mm, "end": v(-2.7, -51.1) * mm});
            skLineSegment(sketch, "E401", {"start": v(-2.7, -51.1) * mm, "end": v(-5.53, -50.44) * mm});
            skLineSegment(sketch, "E402", {"start": v(-5.53, -50.44) * mm, "end": v(-8.4, -49.44) * mm});
            skLineSegment(sketch, "E403", {"start": v(-8.4, -49.44) * mm, "end": v(-11.16, -48.2) * mm});
            skLineSegment(sketch, "E404", {"start": v(-11.16, -48.2) * mm, "end": v(-13.66, -46.8) * mm});
            skLineSegment(sketch, "E405", {"start": v(-13.66, -46.8) * mm, "end": v(-15.73, -45.33) * mm});
            skLineSegment(sketch, "E406", {"start": v(-15.73, -45.33) * mm, "end": v(-17.24, -43.88) * mm});
            skLineSegment(sketch, "E407", {"start": v(-17.24, -43.88) * mm, "end": v(-18.03, -42.56) * mm});
            skLineSegment(sketch, "E408", {"start": v(-18.03, -42.56) * mm, "end": v(-18.87, -40.34) * mm});
            skLineSegment(sketch, "E409", {"start": v(-18.87, -40.34) * mm, "end": v(-20.5, -36.55) * mm});
            skLineSegment(sketch, "E410", {"start": v(-20.5, -36.55) * mm, "end": v(-22.61, -31.77) * mm});
            skLineSegment(sketch, "E411", {"start": v(-22.61, -31.77) * mm, "end": v(-24.95, -26.57) * mm});
            skLineSegment(sketch, "E412", {"start": v(-24.95, -26.57) * mm, "end": v(-27.25, -21.52) * mm});
            skLineSegment(sketch, "E413", {"start": v(-27.25, -21.52) * mm, "end": v(-29.23, -17.2) * mm});
            skLineSegment(sketch, "E414", {"start": v(-29.23, -17.2) * mm, "end": v(-30.61, -14.19) * mm});
            skLineSegment(sketch, "E415", {"start": v(-30.61, -14.19) * mm, "end": v(-31.14, -13.05) * mm});
            skLineSegment(sketch, "E416", {"start": v(-31.14, -13.05) * mm, "end": v(-34.08, -6.53) * mm});
            skLineSegment(sketch, "E417", {"start": v(-34.08, -6.53) * mm, "end": v(-35.94, -0.75) * mm});
            skLineSegment(sketch, "E418", {"start": v(-35.94, -0.75) * mm, "end": v(-36.92, 4.26) * mm});
            skLineSegment(sketch, "E419", {"start": v(-36.92, 4.26) * mm, "end": v(-37.21, 8.52) * mm});
            skLineSegment(sketch, "E420", {"start": v(-37.21, 8.52) * mm, "end": v(-37, 12) * mm});
            skLineSegment(sketch, "E421", {"start": v(-37, 12) * mm, "end": v(-36.5, 14.71) * mm});
            skLineSegment(sketch, "E422", {"start": v(-36.5, 14.71) * mm, "end": v(-35.89, 16.65) * mm});
            skLineSegment(sketch, "E423", {"start": v(-35.89, 16.65) * mm, "end": v(-35.36, 17.8) * mm});
            skLineSegment(sketch, "E424", {"start": v(-35.36, 17.8) * mm, "end": v(-35, 18.52) * mm});
            skLineSegment(sketch, "E425", {"start": v(-35, 18.52) * mm, "end": v(-34.72, 19.22) * mm});
            skLineSegment(sketch, "E426", {"start": v(-34.72, 19.22) * mm, "end": v(-34.52, 19.94) * mm});
            skLineSegment(sketch, "E427", {"start": v(-34.52, 19.94) * mm, "end": v(-34.4, 20.74) * mm});
            skLineSegment(sketch, "E428", {"start": v(-34.4, 20.74) * mm, "end": v(-34.33, 21.67) * mm});
            skLineSegment(sketch, "E429", {"start": v(-34.33, 21.67) * mm, "end": v(-34.31, 22.78) * mm});
            skLineSegment(sketch, "E430", {"start": v(-34.31, 22.78) * mm, "end": v(-34.33, 24.12) * mm});
            skLineSegment(sketch, "E431", {"start": v(-34.33, 24.12) * mm, "end": v(-34.37, 25.73) * mm});
            skLineSegment(sketch, "E432", {"start": v(-34.37, 25.73) * mm, "end": v(-34.35, 27.36) * mm});
            skLineSegment(sketch, "E433", {"start": v(-34.35, 27.36) * mm, "end": v(-34.23, 28.71) * mm});
            skLineSegment(sketch, "E434", {"start": v(-34.23, 28.71) * mm, "end": v(-34.03, 29.81) * mm});
            skLineSegment(sketch, "E435", {"start": v(-34.03, 29.81) * mm, "end": v(-33.8, 30.67) * mm});
            skLineSegment(sketch, "E436", {"start": v(-33.8, 30.67) * mm, "end": v(-33.56, 31.3) * mm});
            skLineSegment(sketch, "E437", {"start": v(-33.56, 31.3) * mm, "end": v(-33.35, 31.74) * mm});
            skLineSegment(sketch, "E438", {"start": v(-33.35, 31.74) * mm, "end": v(-33.2, 31.98) * mm});
            skLineSegment(sketch, "E439", {"start": v(-33.2, 31.98) * mm, "end": v(-33.14, 32.06) * mm});
            skLineSegment(sketch, "E440", {"start": v(-33.14, 32.06) * mm, "end": v(-33.16, 28.92) * mm});
            skLineSegment(sketch, "E441", {"start": v(-33.16, 28.92) * mm, "end": v(-32.49, 26.32) * mm});
            skLineSegment(sketch, "E442", {"start": v(-32.49, 26.32) * mm, "end": v(-31.33, 24.22) * mm});
            skLineSegment(sketch, "E443", {"start": v(-31.33, 24.22) * mm, "end": v(-29.9, 22.58) * mm});
            skLineSegment(sketch, "E444", {"start": v(-29.9, 22.58) * mm, "end": v(-28.42, 21.37) * mm});
            skLineSegment(sketch, "E445", {"start": v(-28.42, 21.37) * mm, "end": v(-27.1, 20.56) * mm});
            skLineSegment(sketch, "E446", {"start": v(-27.1, 20.56) * mm, "end": v(-26.15, 20.1) * mm});
            skLineSegment(sketch, "E447", {"start": v(-26.15, 20.1) * mm, "end": v(-25.79, 19.95) * mm});
            skLineSegment(sketch, "E448", {"start": v(-25.79, 19.95) * mm, "end": v(-25.15, 22.03) * mm});
            skLineSegment(sketch, "E449", {"start": v(-25.15, 22.03) * mm, "end": v(-23.6, 23.59) * mm});
            skLineSegment(sketch, "E450", {"start": v(-23.6, 23.59) * mm, "end": v(-21.37, 24.7) * mm});
            skLineSegment(sketch, "E451", {"start": v(-21.37, 24.7) * mm, "end": v(-18.76, 25.4) * mm});
            skLineSegment(sketch, "E452", {"start": v(-18.76, 25.4) * mm, "end": v(-16.01, 25.76) * mm});
            skLineSegment(sketch, "E453", {"start": v(-16.01, 25.76) * mm, "end": v(-13.4, 25.83) * mm});
            skLineSegment(sketch, "E454", {"start": v(-13.4, 25.83) * mm, "end": v(-11.16, 25.68) * mm});
            skLineSegment(sketch, "E455", {"start": v(-11.16, 25.68) * mm, "end": v(-9.59, 25.36) * mm});
            skLineSegment(sketch, "E456", {"start": v(-9.59, 25.36) * mm, "end": v(-8.4, 25.12) * mm});
            skLineSegment(sketch, "E457", {"start": v(-8.4, 25.12) * mm, "end": v(-7.24, 25.15) * mm});
            skLineSegment(sketch, "E458", {"start": v(-7.24, 25.15) * mm, "end": v(-6.12, 25.4) * mm});
            skLineSegment(sketch, "E459", {"start": v(-6.12, 25.4) * mm, "end": v(-5.09, 25.84) * mm});
            skLineSegment(sketch, "E460", {"start": v(-5.09, 25.84) * mm, "end": v(-4.19, 26.42) * mm});
            skLineSegment(sketch, "E461", {"start": v(-4.19, 26.42) * mm, "end": v(-3.46, 27.1) * mm});
            skLineSegment(sketch, "E462", {"start": v(-3.46, 27.1) * mm, "end": v(-2.95, 27.84) * mm});
            skLineSegment(sketch, "E463", {"start": v(-2.95, 27.84) * mm, "end": v(-2.7, 28.6) * mm});
            skLineSegment(sketch, "E464", {"start": v(-2.7, 28.6) * mm, "end": v(-2.74, 29.38) * mm});
            skLineSegment(sketch, "E465", {"start": v(-2.74, 29.38) * mm, "end": v(-3.07, 30.23) * mm});
            skLineSegment(sketch, "E466", {"start": v(-3.07, 30.23) * mm, "end": v(-3.63, 31.12) * mm});
            skLineSegment(sketch, "E467", {"start": v(-3.63, 31.12) * mm, "end": v(-4.4, 32.03) * mm});
            skLineSegment(sketch, "E468", {"start": v(-4.4, 32.03) * mm, "end": v(-5.3, 32.94) * mm});
            skLineSegment(sketch, "E469", {"start": v(-5.3, 32.94) * mm, "end": v(-6.34, 33.84) * mm});
            skLineSegment(sketch, "E470", {"start": v(-6.34, 33.84) * mm, "end": v(-7.43, 34.69) * mm});
            skLineSegment(sketch, "E471", {"start": v(-7.43, 34.69) * mm, "end": v(-8.55, 35.47) * mm});
            skLineSegment(sketch, "E472", {"start": v(-8.55, 35.47) * mm, "end": v(-9.65, 36.42) * mm});
            skLineSegment(sketch, "E473", {"start": v(-9.65, 36.42) * mm, "end": v(-10.68, 37.67) * mm});
            skLineSegment(sketch, "E474", {"start": v(-10.68, 37.67) * mm, "end": v(-11.62, 39.1) * mm});
            skLineSegment(sketch, "E475", {"start": v(-11.62, 39.1) * mm, "end": v(-12.45, 40.57) * mm});
            skLineSegment(sketch, "E476", {"start": v(-12.45, 40.57) * mm, "end": v(-13.14, 41.94) * mm});
            skLineSegment(sketch, "E477", {"start": v(-13.14, 41.94) * mm, "end": v(-13.67, 43.1) * mm});
            skLineSegment(sketch, "E478", {"start": v(-13.67, 43.1) * mm, "end": v(-14, 43.88) * mm});
            skLineSegment(sketch, "E479", {"start": v(-14, 43.88) * mm, "end": v(-14.12, 44.17) * mm});
            skLineSegment(sketch, "E480", {"start": v(-14.12, 44.17) * mm, "end": v(-14.03, 44.04) * mm});
            skLineSegment(sketch, "E481", {"start": v(-14.03, 44.04) * mm, "end": v(-13.76, 43.7) * mm});
            skLineSegment(sketch, "E482", {"start": v(-13.76, 43.7) * mm, "end": v(-13.35, 43.22) * mm});
            skLineSegment(sketch, "E483", {"start": v(-13.35, 43.22) * mm, "end": v(-12.84, 42.7) * mm});
            skLineSegment(sketch, "E484", {"start": v(-12.84, 42.7) * mm, "end": v(-12.24, 42.2) * mm});
            skLineSegment(sketch, "E485", {"start": v(-12.24, 42.2) * mm, "end": v(-11.59, 41.83) * mm});
            skLineSegment(sketch, "E486", {"start": v(-11.59, 41.83) * mm, "end": v(-10.92, 41.66) * mm});
            skLineSegment(sketch, "E487", {"start": v(-10.92, 41.66) * mm, "end": v(-10.25, 41.77) * mm});
            skLineSegment(sketch, "E488", {"start": v(-10.25, 41.77) * mm, "end": v(-9.7, 42.1) * mm});
            skLineSegment(sketch, "E489", {"start": v(-9.7, 42.1) * mm, "end": v(-9.3, 42.52) * mm});
            skLineSegment(sketch, "E490", {"start": v(-9.3, 42.52) * mm, "end": v(-8.93, 42.97) * mm});
            skLineSegment(sketch, "E491", {"start": v(-8.93, 42.97) * mm, "end": v(-8.54, 43.4) * mm});
            skLineSegment(sketch, "E492", {"start": v(-8.54, 43.4) * mm, "end": v(-8.02, 43.8) * mm});
            skLineSegment(sketch, "E493", {"start": v(-8.02, 43.8) * mm, "end": v(-7.28, 44.08) * mm});
            skLineSegment(sketch, "E494", {"start": v(-7.28, 44.08) * mm, "end": v(-6.23, 44.22) * mm});
            skLineSegment(sketch, "E495", {"start": v(-6.23, 44.22) * mm, "end": v(-4.78, 44.17) * mm});
            skLineSegment(sketch, "E496", {"start": v(-4.78, 44.17) * mm, "end": v(-3.3, 44.04) * mm});
            skLineSegment(sketch, "E497", {"start": v(-3.3, 44.04) * mm, "end": v(-2.15, 43.95) * mm});
            skLineSegment(sketch, "E498", {"start": v(-2.15, 43.95) * mm, "end": v(-1.32, 43.89) * mm});
            skLineSegment(sketch, "E499", {"start": v(-1.32, 43.89) * mm, "end": v(-0.74, 43.86) * mm});
            skLineSegment(sketch, "E500", {"start": v(-0.74, 43.86) * mm, "end": v(-0.37, 43.84) * mm});
            skLineSegment(sketch, "E501", {"start": v(-0.37, 43.84) * mm, "end": v(-0.16, 43.84) * mm});
            skLineSegment(sketch, "E502", {"start": v(-0.16, 43.84) * mm, "end": v(-0.07, 43.85) * mm});
            skLineSegment(sketch, "E503", {"start": v(-0.07, 43.85) * mm, "end": v(-0.05, 43.85) * mm});
            skLineSegment(sketch, "E504", {"start": v(0.06, -42.54) * mm, "end": v(0.3, -42.5) * mm});
            skLineSegment(sketch, "E505", {"start": v(0.3, -42.5) * mm, "end": v(0.96, -42.36) * mm});
            skLineSegment(sketch, "E506", {"start": v(0.96, -42.36) * mm, "end": v(1.98, -42.16) * mm});
            skLineSegment(sketch, "E507", {"start": v(1.98, -42.16) * mm, "end": v(3.3, -41.89) * mm});
            skLineSegment(sketch, "E508", {"start": v(3.3, -41.89) * mm, "end": v(4.84, -41.57) * mm});
            skLineSegment(sketch, "E509", {"start": v(4.84, -41.57) * mm, "end": v(6.55, -41.2) * mm});
            skLineSegment(sketch, "E510", {"start": v(6.55, -41.2) * mm, "end": v(8.35, -40.8) * mm});
            skLineSegment(sketch, "E511", {"start": v(8.35, -40.8) * mm, "end": v(10.2, -40.38) * mm});
            skLineSegment(sketch, "E512", {"start": v(10.2, -40.38) * mm, "end": v(11.93, -39.42) * mm});
            skLineSegment(sketch, "E513", {"start": v(11.93, -39.42) * mm, "end": v(13.48, -37.58) * mm});
            skLineSegment(sketch, "E514", {"start": v(13.48, -37.58) * mm, "end": v(14.82, -35.18) * mm});
            skLineSegment(sketch, "E515", {"start": v(14.82, -35.18) * mm, "end": v(15.95, -32.53) * mm});
            skLineSegment(sketch, "E516", {"start": v(15.95, -32.53) * mm, "end": v(16.84, -29.94) * mm});
            skLineSegment(sketch, "E517", {"start": v(16.84, -29.94) * mm, "end": v(17.5, -27.7) * mm});
            skLineSegment(sketch, "E518", {"start": v(17.5, -27.7) * mm, "end": v(17.9, -26.13) * mm});
            skLineSegment(sketch, "E519", {"start": v(17.9, -26.13) * mm, "end": v(18.04, -25.54) * mm});
            skLineSegment(sketch, "E520", {"start": v(18.04, -25.54) * mm, "end": v(17.76, -20.88) * mm});
            skLineSegment(sketch, "E521", {"start": v(17.76, -20.88) * mm, "end": v(17.48, -16.22) * mm});
            skLineSegment(sketch, "E522", {"start": v(17.48, -16.22) * mm, "end": v(17.2, -11.56) * mm});
            skLineSegment(sketch, "E523", {"start": v(17.2, -11.56) * mm, "end": v(16.92, -6.9) * mm});
            skLineSegment(sketch, "E524", {"start": v(16.92, -6.9) * mm, "end": v(16.65, -2.23) * mm});
            skLineSegment(sketch, "E525", {"start": v(16.65, -2.23) * mm, "end": v(16.37, 2.43) * mm});
            skLineSegment(sketch, "E526", {"start": v(16.37, 2.43) * mm, "end": v(16.09, 7.1) * mm});
            skLineSegment(sketch, "E527", {"start": v(16.09, 7.1) * mm, "end": v(15.8, 11.76) * mm});
            skLineSegment(sketch, "E528", {"start": v(15.8, 11.76) * mm, "end": v(14.44, 14.82) * mm});
            skLineSegment(sketch, "E529", {"start": v(14.44, 14.82) * mm, "end": v(12.32, 16.83) * mm});
            skLineSegment(sketch, "E530", {"start": v(12.32, 16.83) * mm, "end": v(9.74, 17.98) * mm});
            skLineSegment(sketch, "E531", {"start": v(9.74, 17.98) * mm, "end": v(6.98, 18.48) * mm});
            skLineSegment(sketch, "E532", {"start": v(6.98, 18.48) * mm, "end": v(4.34, 18.52) * mm});
            skLineSegment(sketch, "E533", {"start": v(4.34, 18.52) * mm, "end": v(2.1, 18.3) * mm});
            skLineSegment(sketch, "E534", {"start": v(2.1, 18.3) * mm, "end": v(0.53, 18.02) * mm});
            skLineSegment(sketch, "E535", {"start": v(0.53, 18.02) * mm, "end": v(-0.05, 17.89) * mm});
            skLineSegment(sketch, "E536", {"start": v(-0.05, 17.89) * mm, "end": v(-0.63, 18.02) * mm});
            skLineSegment(sketch, "E537", {"start": v(-0.63, 18.02) * mm, "end": v(-2.2, 18.3) * mm});
            skLineSegment(sketch, "E538", {"start": v(-2.2, 18.3) * mm, "end": v(-4.44, 18.52) * mm});
            skLineSegment(sketch, "E539", {"start": v(-4.44, 18.52) * mm, "end": v(-7.08, 18.48) * mm});
            skLineSegment(sketch, "E540", {"start": v(-7.08, 18.48) * mm, "end": v(-9.84, 17.98) * mm});
            skLineSegment(sketch, "E541", {"start": v(-9.84, 17.98) * mm, "end": v(-12.42, 16.83) * mm});
            skLineSegment(sketch, "E542", {"start": v(-12.42, 16.83) * mm, "end": v(-14.54, 14.82) * mm});
            skLineSegment(sketch, "E543", {"start": v(-14.54, 14.82) * mm, "end": v(-15.9, 11.76) * mm});
            skLineSegment(sketch, "E544", {"start": v(-15.9, 11.76) * mm, "end": v(-16.18, 7.1) * mm});
            skLineSegment(sketch, "E545", {"start": v(-16.18, 7.1) * mm, "end": v(-16.46, 2.43) * mm});
            skLineSegment(sketch, "E546", {"start": v(-16.46, 2.43) * mm, "end": v(-16.74, -2.23) * mm});
            skLineSegment(sketch, "E547", {"start": v(-16.74, -2.23) * mm, "end": v(-17.02, -6.9) * mm});
            skLineSegment(sketch, "E548", {"start": v(-17.02, -6.9) * mm, "end": v(-17.3, -11.56) * mm});
            skLineSegment(sketch, "E549", {"start": v(-17.3, -11.56) * mm, "end": v(-17.58, -16.22) * mm});
            skLineSegment(sketch, "E550", {"start": v(-17.58, -16.22) * mm, "end": v(-17.86, -20.88) * mm});
            skLineSegment(sketch, "E551", {"start": v(-17.86, -20.88) * mm, "end": v(-18.14, -25.54) * mm});
            skLineSegment(sketch, "E552", {"start": v(-18.14, -25.54) * mm, "end": v(-18, -26.13) * mm});
            skLineSegment(sketch, "E553", {"start": v(-18, -26.13) * mm, "end": v(-17.6, -27.7) * mm});
            skLineSegment(sketch, "E554", {"start": v(-17.6, -27.7) * mm, "end": v(-16.94, -29.94) * mm});
            skLineSegment(sketch, "E555", {"start": v(-16.94, -29.94) * mm, "end": v(-16.04, -32.53) * mm});
            skLineSegment(sketch, "E556", {"start": v(-16.04, -32.53) * mm, "end": v(-14.92, -35.18) * mm});
            skLineSegment(sketch, "E557", {"start": v(-14.92, -35.18) * mm, "end": v(-13.57, -37.58) * mm});
            skLineSegment(sketch, "E558", {"start": v(-13.57, -37.58) * mm, "end": v(-12.03, -39.42) * mm});
            skLineSegment(sketch, "E559", {"start": v(-12.03, -39.42) * mm, "end": v(-10.29, -40.38) * mm});
            skLineSegment(sketch, "E560", {"start": v(-10.29, -40.38) * mm, "end": v(-8.45, -40.8) * mm});
            skLineSegment(sketch, "E561", {"start": v(-8.45, -40.8) * mm, "end": v(-6.64, -41.2) * mm});
            skLineSegment(sketch, "E562", {"start": v(-6.64, -41.2) * mm, "end": v(-4.94, -41.57) * mm});
            skLineSegment(sketch, "E563", {"start": v(-4.94, -41.57) * mm, "end": v(-3.4, -41.89) * mm});
            skLineSegment(sketch, "E564", {"start": v(-3.4, -41.89) * mm, "end": v(-2.08, -42.16) * mm});
            skLineSegment(sketch, "E565", {"start": v(-2.08, -42.16) * mm, "end": v(-1.05, -42.36) * mm});
            skLineSegment(sketch, "E566", {"start": v(-1.05, -42.36) * mm, "end": v(-0.4, -42.5) * mm});
            skLineSegment(sketch, "E567", {"start": v(-0.4, -42.5) * mm, "end": v(-0.16, -42.54) * mm});
            skLineSegment(sketch, "E568", {"start": v(-0.16, -42.54) * mm, "end": v(-0.13, -42.54) * mm});
            skLineSegment(sketch, "E569", {"start": v(-0.13, -42.54) * mm, "end": v(-0.1, -42.54) * mm});
            skLineSegment(sketch, "E570", {"start": v(-0.1, -42.54) * mm, "end": v(-0.08, -42.54) * mm});
            skLineSegment(sketch, "E571", {"start": v(-0.08, -42.54) * mm, "end": v(-0.05, -42.54) * mm});
            skLineSegment(sketch, "E572", {"start": v(-0.05, -42.54) * mm, "end": v(-0.02, -42.54) * mm});
            skLineSegment(sketch, "E573", {"start": v(-0.02, -42.54) * mm, "end": v(0, -42.54) * mm});
            skLineSegment(sketch, "E574", {"start": v(0, -42.54) * mm, "end": v(0.03, -42.54) * mm});
            skLineSegment(sketch, "E575", {"start": v(0.03, -42.54) * mm, "end": v(0.06, -42.54) * mm});
            skLineSegment(sketch, "E576", {"start": v(-24.33, 17.94) * mm, "end": v(-24.52, 15.33) * mm});
            skLineSegment(sketch, "E577", {"start": v(-24.52, 15.33) * mm, "end": v(-24.9, 8.2) * mm});
            skLineSegment(sketch, "E578", {"start": v(-24.9, 8.2) * mm, "end": v(-25.14, -2.39) * mm});
            skLineSegment(sketch, "E579", {"start": v(-25.14, -2.39) * mm, "end": v(-24.99, -15.4) * mm});
            skLineSegment(sketch, "E580", {"start": v(-24.99, -15.4) * mm, "end": v(-24.13, -29.77) * mm});
            skLineSegment(sketch, "E581", {"start": v(-24.13, -29.77) * mm, "end": v(-22.27, -44.45) * mm});
            skLineSegment(sketch, "E582", {"start": v(-22.27, -44.45) * mm, "end": v(-19.11, -58.4) * mm});
            skLineSegment(sketch, "E583", {"start": v(-19.11, -58.4) * mm, "end": v(-14.37, -70.55) * mm});
            skLineSegment(sketch, "E584", {"start": v(-14.37, -70.55) * mm, "end": v(-14.47, -67.96) * mm});
            skLineSegment(sketch, "E585", {"start": v(-14.47, -67.96) * mm, "end": v(-14.7, -60.91) * mm});
            skLineSegment(sketch, "E586", {"start": v(-14.7, -60.91) * mm, "end": v(-14.98, -50.45) * mm});
            skLineSegment(sketch, "E587", {"start": v(-14.98, -50.45) * mm, "end": v(-15.2, -37.6) * mm});
            skLineSegment(sketch, "E588", {"start": v(-15.2, -37.6) * mm, "end": v(-15.25, -23.45) * mm});
            skLineSegment(sketch, "E589", {"start": v(-15.25, -23.45) * mm, "end": v(-15.04, -9) * mm});
            skLineSegment(sketch, "E590", {"start": v(-15.04, -9) * mm, "end": v(-14.48, 4.65) * mm});
            skLineSegment(sketch, "E591", {"start": v(-14.48, 4.65) * mm, "end": v(-13.46, 16.5) * mm});
            skLineSegment(sketch, "E592", {"start": v(-13.46, 16.5) * mm, "end": v(-13.5, 16.6) * mm});
            skLineSegment(sketch, "E593", {"start": v(-13.5, 16.6) * mm, "end": v(-13.64, 16.85) * mm});
            skLineSegment(sketch, "E594", {"start": v(-13.64, 16.85) * mm, "end": v(-13.92, 17.22) * mm});
            skLineSegment(sketch, "E595", {"start": v(-13.92, 17.22) * mm, "end": v(-14.37, 17.67) * mm});
            skLineSegment(sketch, "E596", {"start": v(-14.37, 17.67) * mm, "end": v(-15.02, 18.14) * mm});
            skLineSegment(sketch, "E597", {"start": v(-15.02, 18.14) * mm, "end": v(-15.92, 18.6) * mm});
            skLineSegment(sketch, "E598", {"start": v(-15.92, 18.6) * mm, "end": v(-17.1, 19) * mm});
            skLineSegment(sketch, "E599", {"start": v(-17.1, 19) * mm, "end": v(-18.58, 19.3) * mm});
            skLineSegment(sketch, "E600", {"start": v(-18.58, 19.3) * mm, "end": v(-20.09, 19.43) * mm});
            skLineSegment(sketch, "E601", {"start": v(-20.09, 19.43) * mm, "end": v(-21.33, 19.39) * mm});
            skLineSegment(sketch, "E602", {"start": v(-21.33, 19.39) * mm, "end": v(-22.33, 19.21) * mm});
            skLineSegment(sketch, "E603", {"start": v(-22.33, 19.21) * mm, "end": v(-23.1, 18.95) * mm});
            skLineSegment(sketch, "E604", {"start": v(-23.1, 18.95) * mm, "end": v(-23.66, 18.65) * mm});
            skLineSegment(sketch, "E605", {"start": v(-23.66, 18.65) * mm, "end": v(-24.04, 18.35) * mm});
            skLineSegment(sketch, "E606", {"start": v(-24.04, 18.35) * mm, "end": v(-24.26, 18.1) * mm});
            skLineSegment(sketch, "E607", {"start": v(-24.26, 18.1) * mm, "end": v(-24.33, 17.94) * mm});
            skLineSegment(sketch, "E608", {"start": v(-13.02, 22.63) * mm, "end": v(-13.02, 22.4) * mm});
            skLineSegment(sketch, "E609", {"start": v(-13.02, 22.4) * mm, "end": v(-13, 21.75) * mm});
            skLineSegment(sketch, "E610", {"start": v(-13, 21.75) * mm, "end": v(-12.93, 20.76) * mm});
            skLineSegment(sketch, "E611", {"start": v(-12.93, 20.76) * mm, "end": v(-12.8, 19.48) * mm});
            skLineSegment(sketch, "E612", {"start": v(-12.8, 19.48) * mm, "end": v(-12.6, 17.99) * mm});
            skLineSegment(sketch, "E613", {"start": v(-12.6, 17.99) * mm, "end": v(-12.28, 16.34) * mm});
            skLineSegment(sketch, "E614", {"start": v(-12.28, 16.34) * mm, "end": v(-11.84, 14.6) * mm});
            skLineSegment(sketch, "E615", {"start": v(-11.84, 14.6) * mm, "end": v(-11.26, 12.85) * mm});
            skLineSegment(sketch, "E616", {"start": v(-11.26, 12.85) * mm, "end": v(-11.12, 12.97) * mm});
            skLineSegment(sketch, "E617", {"start": v(-11.12, 12.97) * mm, "end": v(-10.75, 13.34) * mm});
            skLineSegment(sketch, "E618", {"start": v(-10.75, 13.34) * mm, "end": v(-10.2, 13.93) * mm});
            skLineSegment(sketch, "E619", {"start": v(-10.2, 13.93) * mm, "end": v(-9.54, 14.76) * mm});
            skLineSegment(sketch, "E620", {"start": v(-9.54, 14.76) * mm, "end": v(-8.85, 15.82) * mm});
            skLineSegment(sketch, "E621", {"start": v(-8.85, 15.82) * mm, "end": v(-8.18, 17.1) * mm});
            skLineSegment(sketch, "E622", {"start": v(-8.18, 17.1) * mm, "end": v(-7.6, 18.6) * mm});
            skLineSegment(sketch, "E623", {"start": v(-7.6, 18.6) * mm, "end": v(-7.18, 20.3) * mm});
            skLineSegment(sketch, "E624", {"start": v(-7.18, 20.3) * mm, "end": v(-7.21, 20.37) * mm});
            skLineSegment(sketch, "E625", {"start": v(-7.21, 20.37) * mm, "end": v(-7.3, 20.52) * mm});
            skLineSegment(sketch, "E626", {"start": v(-7.3, 20.52) * mm, "end": v(-7.43, 20.75) * mm});
            skLineSegment(sketch, "E627", {"start": v(-7.43, 20.75) * mm, "end": v(-7.63, 21.04) * mm});
            skLineSegment(sketch, "E628", {"start": v(-7.63, 21.04) * mm, "end": v(-7.9, 21.37) * mm});
            skLineSegment(sketch, "E629", {"start": v(-7.9, 21.37) * mm, "end": v(-8.23, 21.71) * mm});
            skLineSegment(sketch, "E630", {"start": v(-8.23, 21.71) * mm, "end": v(-8.64, 22.05) * mm});
            skLineSegment(sketch, "E631", {"start": v(-8.64, 22.05) * mm, "end": v(-9.13, 22.36) * mm});
            skLineSegment(sketch, "E632", {"start": v(-9.13, 22.36) * mm, "end": v(-9.53, 22.55) * mm});
            skLineSegment(sketch, "E633", {"start": v(-9.53, 22.55) * mm, "end": v(-9.98, 22.7) * mm});
            skLineSegment(sketch, "E634", {"start": v(-9.98, 22.7) * mm, "end": v(-10.47, 22.83) * mm});
            skLineSegment(sketch, "E635", {"start": v(-10.47, 22.83) * mm, "end": v(-10.98, 22.9) * mm});
            skLineSegment(sketch, "E636", {"start": v(-10.98, 22.9) * mm, "end": v(-11.5, 22.93) * mm});
            skLineSegment(sketch, "E637", {"start": v(-11.5, 22.93) * mm, "end": v(-12.02, 22.9) * mm});
            skLineSegment(sketch, "E638", {"start": v(-12.02, 22.9) * mm, "end": v(-12.54, 22.8) * mm});
            skLineSegment(sketch, "E639", {"start": v(-12.54, 22.8) * mm, "end": v(-13.02, 22.63) * mm});
            skLineSegment(sketch, "E640", {"start": v(-5.45, 20.74) * mm, "end": v(-5.03, 20.68) * mm});
            skLineSegment(sketch, "E641", {"start": v(-5.03, 20.68) * mm, "end": v(-4.65, 20.5) * mm});
            skLineSegment(sketch, "E642", {"start": v(-4.65, 20.5) * mm, "end": v(-4.32, 20.25) * mm});
            skLineSegment(sketch, "E643", {"start": v(-4.32, 20.25) * mm, "end": v(-4.05, 19.92) * mm});
            skLineSegment(sketch, "E644", {"start": v(-4.05, 19.92) * mm, "end": v(-3.85, 19.55) * mm});
            skLineSegment(sketch, "E645", {"start": v(-3.85, 19.55) * mm, "end": v(-3.74, 19.15) * mm});
            skLineSegment(sketch, "E646", {"start": v(-3.74, 19.15) * mm, "end": v(-3.74, 18.75) * mm});
            skLineSegment(sketch, "E647", {"start": v(-3.74, 18.75) * mm, "end": v(-3.85, 18.38) * mm});
            skLineSegment(sketch, "E648", {"start": v(-3.85, 18.38) * mm, "end": v(-4.05, 18) * mm});
            skLineSegment(sketch, "E649", {"start": v(-4.05, 18) * mm, "end": v(-4.29, 17.6) * mm});
            skLineSegment(sketch, "E650", {"start": v(-4.29, 17.6) * mm, "end": v(-4.55, 17.22) * mm});
            skLineSegment(sketch, "E651", {"start": v(-4.55, 17.22) * mm, "end": v(-4.82, 16.85) * mm});
            skLineSegment(sketch, "E652", {"start": v(-4.82, 16.85) * mm, "end": v(-5.07, 16.53) * mm});
            skLineSegment(sketch, "E653", {"start": v(-5.07, 16.53) * mm, "end": v(-5.27, 16.28) * mm});
            skLineSegment(sketch, "E654", {"start": v(-5.27, 16.28) * mm, "end": v(-5.4, 16.11) * mm});
            skLineSegment(sketch, "E655", {"start": v(-5.4, 16.11) * mm, "end": v(-5.46, 16.05) * mm});
            skLineSegment(sketch, "E656", {"start": v(-5.46, 16.05) * mm, "end": v(-5.53, 16.13) * mm});
            skLineSegment(sketch, "E657", {"start": v(-5.53, 16.13) * mm, "end": v(-5.71, 16.34) * mm});
            skLineSegment(sketch, "E658", {"start": v(-5.71, 16.34) * mm, "end": v(-5.98, 16.65) * mm});
            skLineSegment(sketch, "E659", {"start": v(-5.98, 16.65) * mm, "end": v(-6.29, 17.04) * mm});
            skLineSegment(sketch, "E660", {"start": v(-6.29, 17.04) * mm, "end": v(-6.6, 17.49) * mm});
            skLineSegment(sketch, "E661", {"start": v(-6.6, 17.49) * mm, "end": v(-6.88, 17.96) * mm});
            skLineSegment(sketch, "E662", {"start": v(-6.88, 17.96) * mm, "end": v(-7.08, 18.44) * mm});
            skLineSegment(sketch, "E663", {"start": v(-7.08, 18.44) * mm, "end": v(-7.18, 18.9) * mm});
            skLineSegment(sketch, "E664", {"start": v(-7.18, 18.9) * mm, "end": v(-7.17, 19.3) * mm});
            skLineSegment(sketch, "E665", {"start": v(-7.17, 19.3) * mm, "end": v(-7.08, 19.67) * mm});
            skLineSegment(sketch, "E666", {"start": v(-7.08, 19.67) * mm, "end": v(-6.93, 19.99) * mm});
            skLineSegment(sketch, "E667", {"start": v(-6.93, 19.99) * mm, "end": v(-6.72, 20.25) * mm});
            skLineSegment(sketch, "E668", {"start": v(-6.72, 20.25) * mm, "end": v(-6.45, 20.46) * mm});
            skLineSegment(sketch, "E669", {"start": v(-6.45, 20.46) * mm, "end": v(-6.15, 20.62) * mm});
            skLineSegment(sketch, "E670", {"start": v(-6.15, 20.62) * mm, "end": v(-5.81, 20.71) * mm});
            skLineSegment(sketch, "E671", {"start": v(-5.81, 20.71) * mm, "end": v(-5.45, 20.74) * mm});
            skLineSegment(sketch, "E672", {"start": v(-1.9, 20.08) * mm, "end": v(-1.5, 20.02) * mm});
            skLineSegment(sketch, "E673", {"start": v(-1.5, 20.02) * mm, "end": v(-1.15, 19.86) * mm});
            skLineSegment(sketch, "E674", {"start": v(-1.15, 19.86) * mm, "end": v(-0.84, 19.62) * mm});
            skLineSegment(sketch, "E675", {"start": v(-0.84, 19.62) * mm, "end": v(-0.6, 19.32) * mm});
            skLineSegment(sketch, "E676", {"start": v(-0.6, 19.32) * mm, "end": v(-0.41, 18.97) * mm});
            skLineSegment(sketch, "E677", {"start": v(-0.41, 18.97) * mm, "end": v(-0.31, 18.6) * mm});
            skLineSegment(sketch, "E678", {"start": v(-0.31, 18.6) * mm, "end": v(-0.3, 18.24) * mm});
            skLineSegment(sketch, "E679", {"start": v(-0.3, 18.24) * mm, "end": v(-0.4, 17.89) * mm});
            skLineSegment(sketch, "E680", {"start": v(-0.4, 17.89) * mm, "end": v(-0.6, 17.54) * mm});
            skLineSegment(sketch, "E681", {"start": v(-0.6, 17.54) * mm, "end": v(-0.82, 17.18) * mm});
            skLineSegment(sketch, "E682", {"start": v(-0.82, 17.18) * mm, "end": v(-1.06, 16.82) * mm});
            skLineSegment(sketch, "E683", {"start": v(-1.06, 16.82) * mm, "end": v(-1.3, 16.48) * mm});
            skLineSegment(sketch, "E684", {"start": v(-1.3, 16.48) * mm, "end": v(-1.54, 16.18) * mm});
            skLineSegment(sketch, "E685", {"start": v(-1.54, 16.18) * mm, "end": v(-1.72, 15.95) * mm});
            skLineSegment(sketch, "E686", {"start": v(-1.72, 15.95) * mm, "end": v(-1.85, 15.8) * mm});
            skLineSegment(sketch, "E687", {"start": v(-1.85, 15.8) * mm, "end": v(-1.9, 15.74) * mm});
            skLineSegment(sketch, "E688", {"start": v(-1.9, 15.74) * mm, "end": v(-1.96, 15.8) * mm});
            skLineSegment(sketch, "E689", {"start": v(-1.96, 15.8) * mm, "end": v(-2.14, 16) * mm});
            skLineSegment(sketch, "E690", {"start": v(-2.14, 16) * mm, "end": v(-2.38, 16.29) * mm});
            skLineSegment(sketch, "E691", {"start": v(-2.38, 16.29) * mm, "end": v(-2.67, 16.65) * mm});
            skLineSegment(sketch, "E692", {"start": v(-2.67, 16.65) * mm, "end": v(-2.95, 17.07) * mm});
            skLineSegment(sketch, "E693", {"start": v(-2.95, 17.07) * mm, "end": v(-3.21, 17.5) * mm});
            skLineSegment(sketch, "E694", {"start": v(-3.21, 17.5) * mm, "end": v(-3.4, 17.95) * mm});
            skLineSegment(sketch, "E695", {"start": v(-3.4, 17.95) * mm, "end": v(-3.5, 18.37) * mm});
            skLineSegment(sketch, "E696", {"start": v(-3.5, 18.37) * mm, "end": v(-3.48, 18.75) * mm});
            skLineSegment(sketch, "E697", {"start": v(-3.48, 18.75) * mm, "end": v(-3.4, 19.08) * mm});
            skLineSegment(sketch, "E698", {"start": v(-3.4, 19.08) * mm, "end": v(-3.26, 19.38) * mm});
            skLineSegment(sketch, "E699", {"start": v(-3.26, 19.38) * mm, "end": v(-3.06, 19.62) * mm});
            skLineSegment(sketch, "E700", {"start": v(-3.06, 19.62) * mm, "end": v(-2.82, 19.82) * mm});
            skLineSegment(sketch, "E701", {"start": v(-2.82, 19.82) * mm, "end": v(-2.54, 19.96) * mm});
            skLineSegment(sketch, "E702", {"start": v(-2.54, 19.96) * mm, "end": v(-2.23, 20.05) * mm});
            skLineSegment(sketch, "E703", {"start": v(-2.23, 20.05) * mm, "end": v(-1.9, 20.08) * mm});
            skLineSegment(sketch, "E704", {"start": v(12.68, 22.63) * mm, "end": v(12.67, 22.4) * mm});
            skLineSegment(sketch, "E705", {"start": v(12.67, 22.4) * mm, "end": v(12.65, 21.75) * mm});
            skLineSegment(sketch, "E706", {"start": v(12.65, 21.75) * mm, "end": v(12.58, 20.76) * mm});
            skLineSegment(sketch, "E707", {"start": v(12.58, 20.76) * mm, "end": v(12.46, 19.48) * mm});
            skLineSegment(sketch, "E708", {"start": v(12.46, 19.48) * mm, "end": v(12.25, 17.99) * mm});
            skLineSegment(sketch, "E709", {"start": v(12.25, 17.99) * mm, "end": v(11.94, 16.34) * mm});
            skLineSegment(sketch, "E710", {"start": v(11.94, 16.34) * mm, "end": v(11.5, 14.6) * mm});
            skLineSegment(sketch, "E711", {"start": v(11.5, 14.6) * mm, "end": v(10.92, 12.85) * mm});
            skLineSegment(sketch, "E712", {"start": v(10.92, 12.85) * mm, "end": v(10.78, 12.97) * mm});
            skLineSegment(sketch, "E713", {"start": v(10.78, 12.97) * mm, "end": v(10.4, 13.34) * mm});
            skLineSegment(sketch, "E714", {"start": v(10.4, 13.34) * mm, "end": v(9.85, 13.93) * mm});
            skLineSegment(sketch, "E715", {"start": v(9.85, 13.93) * mm, "end": v(9.2, 14.76) * mm});
            skLineSegment(sketch, "E716", {"start": v(9.2, 14.76) * mm, "end": v(8.5, 15.82) * mm});
            skLineSegment(sketch, "E717", {"start": v(8.5, 15.82) * mm, "end": v(7.83, 17.1) * mm});
            skLineSegment(sketch, "E718", {"start": v(7.83, 17.1) * mm, "end": v(7.26, 18.6) * mm});
            skLineSegment(sketch, "E719", {"start": v(7.26, 18.6) * mm, "end": v(6.84, 20.3) * mm});
            skLineSegment(sketch, "E720", {"start": v(6.84, 20.3) * mm, "end": v(6.87, 20.37) * mm});
            skLineSegment(sketch, "E721", {"start": v(6.87, 20.37) * mm, "end": v(6.95, 20.52) * mm});
            skLineSegment(sketch, "E722", {"start": v(6.95, 20.52) * mm, "end": v(7.09, 20.75) * mm});
            skLineSegment(sketch, "E723", {"start": v(7.09, 20.75) * mm, "end": v(7.29, 21.04) * mm});
            skLineSegment(sketch, "E724", {"start": v(7.29, 21.04) * mm, "end": v(7.55, 21.37) * mm});
            skLineSegment(sketch, "E725", {"start": v(7.55, 21.37) * mm, "end": v(7.89, 21.71) * mm});
            skLineSegment(sketch, "E726", {"start": v(7.89, 21.71) * mm, "end": v(8.3, 22.05) * mm});
            skLineSegment(sketch, "E727", {"start": v(8.3, 22.05) * mm, "end": v(8.79, 22.36) * mm});
            skLineSegment(sketch, "E728", {"start": v(8.79, 22.36) * mm, "end": v(9.19, 22.55) * mm});
            skLineSegment(sketch, "E729", {"start": v(9.19, 22.55) * mm, "end": v(9.64, 22.7) * mm});
            skLineSegment(sketch, "E730", {"start": v(9.64, 22.7) * mm, "end": v(10.12, 22.83) * mm});
            skLineSegment(sketch, "E731", {"start": v(10.12, 22.83) * mm, "end": v(10.63, 22.9) * mm});
            skLineSegment(sketch, "E732", {"start": v(10.63, 22.9) * mm, "end": v(11.16, 22.93) * mm});
            skLineSegment(sketch, "E733", {"start": v(11.16, 22.93) * mm, "end": v(11.68, 22.9) * mm});
            skLineSegment(sketch, "E734", {"start": v(11.68, 22.9) * mm, "end": v(12.2, 22.8) * mm});
            skLineSegment(sketch, "E735", {"start": v(12.2, 22.8) * mm, "end": v(12.68, 22.63) * mm});
            skLineSegment(sketch, "E736", {"start": v(5.1, 20.74) * mm, "end": v(4.69, 20.68) * mm});
            skLineSegment(sketch, "E737", {"start": v(4.69, 20.68) * mm, "end": v(4.3, 20.5) * mm});
            skLineSegment(sketch, "E738", {"start": v(4.3, 20.5) * mm, "end": v(3.97, 20.25) * mm});
            skLineSegment(sketch, "E739", {"start": v(3.97, 20.25) * mm, "end": v(3.7, 19.92) * mm});
            skLineSegment(sketch, "E740", {"start": v(3.7, 19.92) * mm, "end": v(3.5, 19.55) * mm});
            skLineSegment(sketch, "E741", {"start": v(3.5, 19.55) * mm, "end": v(3.4, 19.15) * mm});
            skLineSegment(sketch, "E742", {"start": v(3.4, 19.15) * mm, "end": v(3.4, 18.75) * mm});
            skLineSegment(sketch, "E743", {"start": v(3.4, 18.75) * mm, "end": v(3.5, 18.38) * mm});
            skLineSegment(sketch, "E744", {"start": v(3.5, 18.38) * mm, "end": v(3.7, 18) * mm});
            skLineSegment(sketch, "E745", {"start": v(3.7, 18) * mm, "end": v(3.94, 17.6) * mm});
            skLineSegment(sketch, "E746", {"start": v(3.94, 17.6) * mm, "end": v(4.2, 17.22) * mm});
            skLineSegment(sketch, "E747", {"start": v(4.2, 17.22) * mm, "end": v(4.47, 16.85) * mm});
            skLineSegment(sketch, "E748", {"start": v(4.47, 16.85) * mm, "end": v(4.72, 16.53) * mm});
            skLineSegment(sketch, "E749", {"start": v(4.72, 16.53) * mm, "end": v(4.92, 16.28) * mm});
            skLineSegment(sketch, "E750", {"start": v(4.92, 16.28) * mm, "end": v(5.06, 16.11) * mm});
            skLineSegment(sketch, "E751", {"start": v(5.06, 16.11) * mm, "end": v(5.1, 16.05) * mm});
            skLineSegment(sketch, "E752", {"start": v(5.1, 16.05) * mm, "end": v(5.18, 16.13) * mm});
            skLineSegment(sketch, "E753", {"start": v(5.18, 16.13) * mm, "end": v(5.37, 16.34) * mm});
            skLineSegment(sketch, "E754", {"start": v(5.37, 16.34) * mm, "end": v(5.63, 16.65) * mm});
            skLineSegment(sketch, "E755", {"start": v(5.63, 16.65) * mm, "end": v(5.94, 17.04) * mm});
            skLineSegment(sketch, "E756", {"start": v(5.94, 17.04) * mm, "end": v(6.25, 17.49) * mm});
            skLineSegment(sketch, "E757", {"start": v(6.25, 17.49) * mm, "end": v(6.53, 17.96) * mm});
            skLineSegment(sketch, "E758", {"start": v(6.53, 17.96) * mm, "end": v(6.74, 18.44) * mm});
            skLineSegment(sketch, "E759", {"start": v(6.74, 18.44) * mm, "end": v(6.83, 18.9) * mm});
            skLineSegment(sketch, "E760", {"start": v(6.83, 18.9) * mm, "end": v(6.82, 19.3) * mm});
            skLineSegment(sketch, "E761", {"start": v(6.82, 19.3) * mm, "end": v(6.74, 19.67) * mm});
            skLineSegment(sketch, "E762", {"start": v(6.74, 19.67) * mm, "end": v(6.58, 19.99) * mm});
            skLineSegment(sketch, "E763", {"start": v(6.58, 19.99) * mm, "end": v(6.37, 20.25) * mm});
            skLineSegment(sketch, "E764", {"start": v(6.37, 20.25) * mm, "end": v(6.1, 20.46) * mm});
            skLineSegment(sketch, "E765", {"start": v(6.1, 20.46) * mm, "end": v(5.8, 20.62) * mm});
            skLineSegment(sketch, "E766", {"start": v(5.8, 20.62) * mm, "end": v(5.47, 20.71) * mm});
            skLineSegment(sketch, "E767", {"start": v(5.47, 20.71) * mm, "end": v(5.1, 20.74) * mm});
            skLineSegment(sketch, "E768", {"start": v(1.55, 20.08) * mm, "end": v(1.16, 20.02) * mm});
            skLineSegment(sketch, "E769", {"start": v(1.16, 20.02) * mm, "end": v(0.8, 19.86) * mm});
            skLineSegment(sketch, "E770", {"start": v(0.8, 19.86) * mm, "end": v(0.5, 19.62) * mm});
            skLineSegment(sketch, "E771", {"start": v(0.5, 19.62) * mm, "end": v(0.25, 19.32) * mm});
            skLineSegment(sketch, "E772", {"start": v(0.25, 19.32) * mm, "end": v(0.07, 18.97) * mm});
            skLineSegment(sketch, "E773", {"start": v(0.07, 18.97) * mm, "end": v(-0.03, 18.6) * mm});
            skLineSegment(sketch, "E774", {"start": v(-0.03, 18.6) * mm, "end": v(-0.04, 18.24) * mm});
            skLineSegment(sketch, "E775", {"start": v(-0.04, 18.24) * mm, "end": v(0.06, 17.89) * mm});
            skLineSegment(sketch, "E776", {"start": v(0.06, 17.89) * mm, "end": v(0.25, 17.54) * mm});
            skLineSegment(sketch, "E777", {"start": v(0.25, 17.54) * mm, "end": v(0.47, 17.18) * mm});
            skLineSegment(sketch, "E778", {"start": v(0.47, 17.18) * mm, "end": v(0.72, 16.82) * mm});
            skLineSegment(sketch, "E779", {"start": v(0.72, 16.82) * mm, "end": v(0.96, 16.48) * mm});
            skLineSegment(sketch, "E780", {"start": v(0.96, 16.48) * mm, "end": v(1.2, 16.18) * mm});
            skLineSegment(sketch, "E781", {"start": v(1.2, 16.18) * mm, "end": v(1.38, 15.95) * mm});
            skLineSegment(sketch, "E782", {"start": v(1.38, 15.95) * mm, "end": v(1.5, 15.8) * mm});
            skLineSegment(sketch, "E783", {"start": v(1.5, 15.8) * mm, "end": v(1.55, 15.74) * mm});
            skLineSegment(sketch, "E784", {"start": v(1.55, 15.74) * mm, "end": v(1.62, 15.8) * mm});
            skLineSegment(sketch, "E785", {"start": v(1.62, 15.8) * mm, "end": v(1.8, 16) * mm});
            skLineSegment(sketch, "E786", {"start": v(1.8, 16) * mm, "end": v(2.04, 16.29) * mm});
            skLineSegment(sketch, "E787", {"start": v(2.04, 16.29) * mm, "end": v(2.32, 16.65) * mm});
            skLineSegment(sketch, "E788", {"start": v(2.32, 16.65) * mm, "end": v(2.6, 17.07) * mm});
            skLineSegment(sketch, "E789", {"start": v(2.6, 17.07) * mm, "end": v(2.87, 17.5) * mm});
            skLineSegment(sketch, "E790", {"start": v(2.87, 17.5) * mm, "end": v(3.06, 17.95) * mm});
            skLineSegment(sketch, "E791", {"start": v(3.06, 17.95) * mm, "end": v(3.15, 18.37) * mm});
            skLineSegment(sketch, "E792", {"start": v(3.15, 18.37) * mm, "end": v(3.14, 18.75) * mm});
            skLineSegment(sketch, "E793", {"start": v(3.14, 18.75) * mm, "end": v(3.06, 19.08) * mm});
            skLineSegment(sketch, "E794", {"start": v(3.06, 19.08) * mm, "end": v(2.92, 19.38) * mm});
            skLineSegment(sketch, "E795", {"start": v(2.92, 19.38) * mm, "end": v(2.72, 19.62) * mm});
            skLineSegment(sketch, "E796", {"start": v(2.72, 19.62) * mm, "end": v(2.48, 19.82) * mm});
            skLineSegment(sketch, "E797", {"start": v(2.48, 19.82) * mm, "end": v(2.2, 19.96) * mm});
            skLineSegment(sketch, "E798", {"start": v(2.2, 19.96) * mm, "end": v(1.88, 20.05) * mm});
            skLineSegment(sketch, "E799", {"start": v(1.88, 20.05) * mm, "end": v(1.55, 20.08) * mm});
            skLineSegment(sketch, "E800", {"start": v(-8.28, -41.69) * mm, "end": v(-8.62, -42.08) * mm});
            skLineSegment(sketch, "E801", {"start": v(-8.62, -42.08) * mm, "end": v(-9.07, -42.34) * mm});
            skLineSegment(sketch, "E802", {"start": v(-9.07, -42.34) * mm, "end": v(-9.56, -42.49) * mm});
            skLineSegment(sketch, "E803", {"start": v(-9.56, -42.49) * mm, "end": v(-10.06, -42.55) * mm});
            skLineSegment(sketch, "E804", {"start": v(-10.06, -42.55) * mm, "end": v(-10.53, -42.56) * mm});
            skLineSegment(sketch, "E805", {"start": v(-10.53, -42.56) * mm, "end": v(-10.91, -42.53) * mm});
            skLineSegment(sketch, "E806", {"start": v(-10.91, -42.53) * mm, "end": v(-11.18, -42.49) * mm});
            skLineSegment(sketch, "E807", {"start": v(-11.18, -42.49) * mm, "end": v(-11.28, -42.47) * mm});
            skLineSegment(sketch, "E808", {"start": v(-11.28, -42.47) * mm, "end": v(-12.19, -40.75) * mm});
            skLineSegment(sketch, "E809", {"start": v(-12.19, -40.75) * mm, "end": v(-12.63, -39.1) * mm});
            skLineSegment(sketch, "E810", {"start": v(-12.63, -39.1) * mm, "end": v(-12.7, -37.56) * mm});
            skLineSegment(sketch, "E811", {"start": v(-12.7, -37.56) * mm, "end": v(-12.53, -36.2) * mm});
            skLineSegment(sketch, "E812", {"start": v(-12.53, -36.2) * mm, "end": v(-12.2, -35.05) * mm});
            skLineSegment(sketch, "E813", {"start": v(-12.2, -35.05) * mm, "end": v(-11.84, -34.17) * mm});
            skLineSegment(sketch, "E814", {"start": v(-11.84, -34.17) * mm, "end": v(-11.55, -33.6) * mm});
            skLineSegment(sketch, "E815", {"start": v(-11.55, -33.6) * mm, "end": v(-11.42, -33.4) * mm});
            skLineSegment(sketch, "E816", {"start": v(-11.42, -33.4) * mm, "end": v(-11.37, -33.53) * mm});
            skLineSegment(sketch, "E817", {"start": v(-11.37, -33.53) * mm, "end": v(-11.2, -33.9) * mm});
            skLineSegment(sketch, "E818", {"start": v(-11.2, -33.9) * mm, "end": v(-10.94, -34.41) * mm});
            skLineSegment(sketch, "E819", {"start": v(-10.94, -34.41) * mm, "end": v(-10.58, -35.04) * mm});
            skLineSegment(sketch, "E820", {"start": v(-10.58, -35.04) * mm, "end": v(-10.15, -35.72) * mm});
            skLineSegment(sketch, "E821", {"start": v(-10.15, -35.72) * mm, "end": v(-9.64, -36.4) * mm});
            skLineSegment(sketch, "E822", {"start": v(-9.64, -36.4) * mm, "end": v(-9.07, -37) * mm});
            skLineSegment(sketch, "E823", {"start": v(-9.07, -37) * mm, "end": v(-8.45, -37.47) * mm});
            skLineSegment(sketch, "E824", {"start": v(-8.45, -37.47) * mm, "end": v(-7.95, -37.96) * mm});
            skLineSegment(sketch, "E825", {"start": v(-7.95, -37.96) * mm, "end": v(-7.7, -38.58) * mm});
            skLineSegment(sketch, "E826", {"start": v(-7.7, -38.58) * mm, "end": v(-7.64, -39.27) * mm});
            skLineSegment(sketch, "E827", {"start": v(-7.64, -39.27) * mm, "end": v(-7.72, -39.97) * mm});
            skLineSegment(sketch, "E828", {"start": v(-7.72, -39.97) * mm, "end": v(-7.88, -40.63) * mm});
            skLineSegment(sketch, "E829", {"start": v(-7.88, -40.63) * mm, "end": v(-8.06, -41.17) * mm});
            skLineSegment(sketch, "E830", {"start": v(-8.06, -41.17) * mm, "end": v(-8.22, -41.55) * mm});
            skLineSegment(sketch, "E831", {"start": v(-8.22, -41.55) * mm, "end": v(-8.28, -41.69) * mm});
            skLineSegment(sketch, "E832", {"start": v(-7.3, -34.49) * mm, "end": v(-7.42, -34.65) * mm});
            skLineSegment(sketch, "E833", {"start": v(-7.42, -34.65) * mm, "end": v(-7.68, -35.1) * mm});
            skLineSegment(sketch, "E834", {"start": v(-7.68, -35.1) * mm, "end": v(-8.03, -35.85) * mm});
            skLineSegment(sketch, "E835", {"start": v(-8.03, -35.85) * mm, "end": v(-8.37, -36.85) * mm});
            skLineSegment(sketch, "E836", {"start": v(-8.37, -36.85) * mm, "end": v(-8.63, -38.08) * mm});
            skLineSegment(sketch, "E837", {"start": v(-8.63, -38.08) * mm, "end": v(-8.72, -39.54) * mm});
            skLineSegment(sketch, "E838", {"start": v(-8.72, -39.54) * mm, "end": v(-8.56, -41.19) * mm});
            skLineSegment(sketch, "E839", {"start": v(-8.56, -41.19) * mm, "end": v(-8.06, -43.02) * mm});
            skLineSegment(sketch, "E840", {"start": v(-8.06, -43.02) * mm, "end": v(-8.03, -43.06) * mm});
            skLineSegment(sketch, "E841", {"start": v(-8.03, -43.06) * mm, "end": v(-7.96, -43.14) * mm});
            skLineSegment(sketch, "E842", {"start": v(-7.96, -43.14) * mm, "end": v(-7.86, -43.22) * mm});
            skLineSegment(sketch, "E843", {"start": v(-7.86, -43.22) * mm, "end": v(-7.7, -43.32) * mm});
            skLineSegment(sketch, "E844", {"start": v(-7.7, -43.32) * mm, "end": v(-7.51, -43.4) * mm});
            skLineSegment(sketch, "E845", {"start": v(-7.51, -43.4) * mm, "end": v(-7.27, -43.47) * mm});
            skLineSegment(sketch, "E846", {"start": v(-7.27, -43.47) * mm, "end": v(-6.98, -43.5) * mm});
            skLineSegment(sketch, "E847", {"start": v(-6.98, -43.5) * mm, "end": v(-6.64, -43.5) * mm});
            skLineSegment(sketch, "E848", {"start": v(-6.64, -43.5) * mm, "end": v(-6.42, -43.45) * mm});
            skLineSegment(sketch, "E849", {"start": v(-6.42, -43.45) * mm, "end": v(-6.22, -43.4) * mm});
            skLineSegment(sketch, "E850", {"start": v(-6.22, -43.4) * mm, "end": v(-6.05, -43.33) * mm});
            skLineSegment(sketch, "E851", {"start": v(-6.05, -43.33) * mm, "end": v(-5.9, -43.24) * mm});
            skLineSegment(sketch, "E852", {"start": v(-5.9, -43.24) * mm, "end": v(-5.78, -43.16) * mm});
            skLineSegment(sketch, "E853", {"start": v(-5.78, -43.16) * mm, "end": v(-5.68, -43.07) * mm});
            skLineSegment(sketch, "E854", {"start": v(-5.68, -43.07) * mm, "end": v(-5.6, -43) * mm});
            skLineSegment(sketch, "E855", {"start": v(-5.6, -43) * mm, "end": v(-5.56, -42.92) * mm});
            skLineSegment(sketch, "E856", {"start": v(-5.56, -42.92) * mm, "end": v(-5.33, -42.2) * mm});
            skLineSegment(sketch, "E857", {"start": v(-5.33, -42.2) * mm, "end": v(-5.2, -41.2) * mm});
            skLineSegment(sketch, "E858", {"start": v(-5.2, -41.2) * mm, "end": v(-5.2, -40) * mm});
            skLineSegment(sketch, "E859", {"start": v(-5.2, -40) * mm, "end": v(-5.32, -38.72) * mm});
            skLineSegment(sketch, "E860", {"start": v(-5.32, -38.72) * mm, "end": v(-5.59, -37.43) * mm});
            skLineSegment(sketch, "E861", {"start": v(-5.59, -37.43) * mm, "end": v(-6, -36.23) * mm});
            skLineSegment(sketch, "E862", {"start": v(-6, -36.23) * mm, "end": v(-6.57, -35.22) * mm});
            skLineSegment(sketch, "E863", {"start": v(-6.57, -35.22) * mm, "end": v(-7.3, -34.49) * mm});
            skLineSegment(sketch, "E864", {"start": v(-4.14, -37.26) * mm, "end": v(-4.21, -37.35) * mm});
            skLineSegment(sketch, "E865", {"start": v(-4.21, -37.35) * mm, "end": v(-4.4, -37.6) * mm});
            skLineSegment(sketch, "E866", {"start": v(-4.4, -37.6) * mm, "end": v(-4.67, -38.01) * mm});
            skLineSegment(sketch, "E867", {"start": v(-4.67, -38.01) * mm, "end": v(-4.95, -38.55) * mm});
            skLineSegment(sketch, "E868", {"start": v(-4.95, -38.55) * mm, "end": v(-5.2, -39.18) * mm});
            skLineSegment(sketch, "E869", {"start": v(-5.2, -39.18) * mm, "end": v(-5.37, -39.9) * mm});
            skLineSegment(sketch, "E870", {"start": v(-5.37, -39.9) * mm, "end": v(-5.42, -40.7) * mm});
            skLineSegment(sketch, "E871", {"start": v(-5.42, -40.7) * mm, "end": v(-5.3, -41.52) * mm});
            skLineSegment(sketch, "E872", {"start": v(-5.3, -41.52) * mm, "end": v(-5.21, -41.81) * mm});
            skLineSegment(sketch, "E873", {"start": v(-5.21, -41.81) * mm, "end": v(-5.14, -42.06) * mm});
            skLineSegment(sketch, "E874", {"start": v(-5.14, -42.06) * mm, "end": v(-5.06, -42.28) * mm});
            skLineSegment(sketch, "E875", {"start": v(-5.06, -42.28) * mm, "end": v(-4.99, -42.47) * mm});
            skLineSegment(sketch, "E876", {"start": v(-4.99, -42.47) * mm, "end": v(-4.91, -42.63) * mm});
            skLineSegment(sketch, "E877", {"start": v(-4.91, -42.63) * mm, "end": v(-4.83, -42.78) * mm});
            skLineSegment(sketch, "E878", {"start": v(-4.83, -42.78) * mm, "end": v(-4.75, -42.9) * mm});
            skLineSegment(sketch, "E879", {"start": v(-4.75, -42.9) * mm, "end": v(-4.66, -43.01) * mm});
            skLineSegment(sketch, "E880", {"start": v(-4.66, -43.01) * mm, "end": v(-4.5, -43.18) * mm});
            skLineSegment(sketch, "E881", {"start": v(-4.5, -43.18) * mm, "end": v(-4.37, -43.3) * mm});
            skLineSegment(sketch, "E882", {"start": v(-4.37, -43.3) * mm, "end": v(-4.25, -43.38) * mm});
            skLineSegment(sketch, "E883", {"start": v(-4.25, -43.38) * mm, "end": v(-4.13, -43.44) * mm});
            skLineSegment(sketch, "E884", {"start": v(-4.13, -43.44) * mm, "end": v(-4.01, -43.48) * mm});
            skLineSegment(sketch, "E885", {"start": v(-4.01, -43.48) * mm, "end": v(-3.88, -43.5) * mm});
            skLineSegment(sketch, "E886", {"start": v(-3.88, -43.5) * mm, "end": v(-3.74, -43.5) * mm});
            skLineSegment(sketch, "E887", {"start": v(-3.74, -43.5) * mm, "end": v(-3.57, -43.5) * mm});
            skLineSegment(sketch, "E888", {"start": v(-3.57, -43.5) * mm, "end": v(-3.45, -43.49) * mm});
            skLineSegment(sketch, "E889", {"start": v(-3.45, -43.49) * mm, "end": v(-3.34, -43.44) * mm});
            skLineSegment(sketch, "E890", {"start": v(-3.34, -43.44) * mm, "end": v(-3.23, -43.38) * mm});
            skLineSegment(sketch, "E891", {"start": v(-3.23, -43.38) * mm, "end": v(-3.13, -43.3) * mm});
            skLineSegment(sketch, "E892", {"start": v(-3.13, -43.3) * mm, "end": v(-3.04, -43.2) * mm});
            skLineSegment(sketch, "E893", {"start": v(-3.04, -43.2) * mm, "end": v(-2.96, -43.08) * mm});
            skLineSegment(sketch, "E894", {"start": v(-2.96, -43.08) * mm, "end": v(-2.89, -42.97) * mm});
            skLineSegment(sketch, "E895", {"start": v(-2.89, -42.97) * mm, "end": v(-2.83, -42.85) * mm});
            skLineSegment(sketch, "E896", {"start": v(-2.83, -42.85) * mm, "end": v(-2.68, -42.34) * mm});
            skLineSegment(sketch, "E897", {"start": v(-2.68, -42.34) * mm, "end": v(-2.57, -41.7) * mm});
            skLineSegment(sketch, "E898", {"start": v(-2.57, -41.7) * mm, "end": v(-2.53, -41) * mm});
            skLineSegment(sketch, "E899", {"start": v(-2.53, -41) * mm, "end": v(-2.6, -40.22) * mm});
            skLineSegment(sketch, "E900", {"start": v(-2.6, -40.22) * mm, "end": v(-2.76, -39.43) * mm});
            skLineSegment(sketch, "E901", {"start": v(-2.76, -39.43) * mm, "end": v(-3.06, -38.65) * mm});
            skLineSegment(sketch, "E902", {"start": v(-3.06, -38.65) * mm, "end": v(-3.51, -37.92) * mm});
            skLineSegment(sketch, "E903", {"start": v(-3.51, -37.92) * mm, "end": v(-4.14, -37.26) * mm});
            skLineSegment(sketch, "E904", {"start": v(-1.6, -38.11) * mm, "end": v(-1.67, -38.2) * mm});
            skLineSegment(sketch, "E905", {"start": v(-1.67, -38.2) * mm, "end": v(-1.84, -38.42) * mm});
            skLineSegment(sketch, "E906", {"start": v(-1.84, -38.42) * mm, "end": v(-2.08, -38.77) * mm});
            skLineSegment(sketch, "E907", {"start": v(-2.08, -38.77) * mm, "end": v(-2.33, -39.22) * mm});
            skLineSegment(sketch, "E908", {"start": v(-2.33, -39.22) * mm, "end": v(-2.56, -39.77) * mm});
            skLineSegment(sketch, "E909", {"start": v(-2.56, -39.77) * mm, "end": v(-2.72, -40.4) * mm});
            skLineSegment(sketch, "E910", {"start": v(-2.72, -40.4) * mm, "end": v(-2.77, -41.08) * mm});
            skLineSegment(sketch, "E911", {"start": v(-2.77, -41.08) * mm, "end": v(-2.65, -41.8) * mm});
            skLineSegment(sketch, "E912", {"start": v(-2.65, -41.8) * mm, "end": v(-2.58, -42.02) * mm});
            skLineSegment(sketch, "E913", {"start": v(-2.58, -42.02) * mm, "end": v(-2.51, -42.23) * mm});
            skLineSegment(sketch, "E914", {"start": v(-2.51, -42.23) * mm, "end": v(-2.44, -42.42) * mm});
            skLineSegment(sketch, "E915", {"start": v(-2.44, -42.42) * mm, "end": v(-2.36, -42.6) * mm});
            skLineSegment(sketch, "E916", {"start": v(-2.36, -42.6) * mm, "end": v(-2.29, -42.74) * mm});
            skLineSegment(sketch, "E917", {"start": v(-2.29, -42.74) * mm, "end": v(-2.21, -42.88) * mm});
            skLineSegment(sketch, "E918", {"start": v(-2.21, -42.88) * mm, "end": v(-2.13, -43) * mm});
            skLineSegment(sketch, "E919", {"start": v(-2.13, -43) * mm, "end": v(-2.06, -43.1) * mm});
            skLineSegment(sketch, "E920", {"start": v(-2.06, -43.1) * mm, "end": v(-1.98, -43.19) * mm});
            skLineSegment(sketch, "E921", {"start": v(-1.98, -43.19) * mm, "end": v(-1.9, -43.27) * mm});
            skLineSegment(sketch, "E922", {"start": v(-1.9, -43.27) * mm, "end": v(-1.81, -43.34) * mm});
            skLineSegment(sketch, "E923", {"start": v(-1.81, -43.34) * mm, "end": v(-1.72, -43.4) * mm});
            skLineSegment(sketch, "E924", {"start": v(-1.72, -43.4) * mm, "end": v(-1.61, -43.44) * mm});
            skLineSegment(sketch, "E925", {"start": v(-1.61, -43.44) * mm, "end": v(-1.5, -43.47) * mm});
            skLineSegment(sketch, "E926", {"start": v(-1.5, -43.47) * mm, "end": v(-1.35, -43.5) * mm});
            skLineSegment(sketch, "E927", {"start": v(-1.35, -43.5) * mm, "end": v(-1.19, -43.5) * mm});
            skLineSegment(sketch, "E928", {"start": v(-1.19, -43.5) * mm, "end": v(-1.02, -43.49) * mm});
            skLineSegment(sketch, "E929", {"start": v(-1.02, -43.49) * mm, "end": v(-0.88, -43.45) * mm});
            skLineSegment(sketch, "E930", {"start": v(-0.88, -43.45) * mm, "end": v(-0.76, -43.4) * mm});
            skLineSegment(sketch, "E931", {"start": v(-0.76, -43.4) * mm, "end": v(-0.66, -43.33) * mm});
            skLineSegment(sketch, "E932", {"start": v(-0.66, -43.33) * mm, "end": v(-0.59, -43.25) * mm});
            skLineSegment(sketch, "E933", {"start": v(-0.59, -43.25) * mm, "end": v(-0.53, -43.18) * mm});
            skLineSegment(sketch, "E934", {"start": v(-0.53, -43.18) * mm, "end": v(-0.48, -43.1) * mm});
            skLineSegment(sketch, "E935", {"start": v(-0.48, -43.1) * mm, "end": v(-0.45, -43.05) * mm});
            skLineSegment(sketch, "E936", {"start": v(-0.45, -43.05) * mm, "end": v(-0.31, -42.6) * mm});
            skLineSegment(sketch, "E937", {"start": v(-0.31, -42.6) * mm, "end": v(-0.21, -42.04) * mm});
            skLineSegment(sketch, "E938", {"start": v(-0.21, -42.04) * mm, "end": v(-0.17, -41.4) * mm});
            skLineSegment(sketch, "E939", {"start": v(-0.17, -41.4) * mm, "end": v(-0.22, -40.72) * mm});
            skLineSegment(sketch, "E940", {"start": v(-0.22, -40.72) * mm, "end": v(-0.36, -40.02) * mm});
            skLineSegment(sketch, "E941", {"start": v(-0.36, -40.02) * mm, "end": v(-0.63, -39.33) * mm});
            skLineSegment(sketch, "E942", {"start": v(-0.63, -39.33) * mm, "end": v(-1.03, -38.69) * mm});
            skLineSegment(sketch, "E943", {"start": v(-1.03, -38.69) * mm, "end": v(-1.6, -38.11) * mm});
            skLineSegment(sketch, "E944", {"start": v(7.93, -41.69) * mm, "end": v(8.28, -42.08) * mm});
            skLineSegment(sketch, "E945", {"start": v(8.28, -42.08) * mm, "end": v(8.72, -42.34) * mm});
            skLineSegment(sketch, "E946", {"start": v(8.72, -42.34) * mm, "end": v(9.21, -42.49) * mm});
            skLineSegment(sketch, "E947", {"start": v(9.21, -42.49) * mm, "end": v(9.72, -42.55) * mm});
            skLineSegment(sketch, "E948", {"start": v(9.72, -42.55) * mm, "end": v(10.18, -42.56) * mm});
            skLineSegment(sketch, "E949", {"start": v(10.18, -42.56) * mm, "end": v(10.57, -42.53) * mm});
            skLineSegment(sketch, "E950", {"start": v(10.57, -42.53) * mm, "end": v(10.83, -42.49) * mm});
            skLineSegment(sketch, "E951", {"start": v(10.83, -42.49) * mm, "end": v(10.93, -42.47) * mm});
            skLineSegment(sketch, "E952", {"start": v(10.93, -42.47) * mm, "end": v(11.84, -40.75) * mm});
            skLineSegment(sketch, "E953", {"start": v(11.84, -40.75) * mm, "end": v(12.29, -39.1) * mm});
            skLineSegment(sketch, "E954", {"start": v(12.29, -39.1) * mm, "end": v(12.37, -37.56) * mm});
            skLineSegment(sketch, "E955", {"start": v(12.37, -37.56) * mm, "end": v(12.19, -36.2) * mm});
            skLineSegment(sketch, "E956", {"start": v(12.19, -36.2) * mm, "end": v(11.86, -35.05) * mm});
            skLineSegment(sketch, "E957", {"start": v(11.86, -35.05) * mm, "end": v(11.5, -34.17) * mm});
            skLineSegment(sketch, "E958", {"start": v(11.5, -34.17) * mm, "end": v(11.2, -33.6) * mm});
            skLineSegment(sketch, "E959", {"start": v(11.2, -33.6) * mm, "end": v(11.08, -33.4) * mm});
            skLineSegment(sketch, "E960", {"start": v(11.08, -33.4) * mm, "end": v(11.02, -33.53) * mm});
            skLineSegment(sketch, "E961", {"start": v(11.02, -33.53) * mm, "end": v(10.86, -33.9) * mm});
            skLineSegment(sketch, "E962", {"start": v(10.86, -33.9) * mm, "end": v(10.6, -34.41) * mm});
            skLineSegment(sketch, "E963", {"start": v(10.6, -34.41) * mm, "end": v(10.24, -35.04) * mm});
            skLineSegment(sketch, "E964", {"start": v(10.24, -35.04) * mm, "end": v(9.8, -35.72) * mm});
            skLineSegment(sketch, "E965", {"start": v(9.8, -35.72) * mm, "end": v(9.3, -36.4) * mm});
            skLineSegment(sketch, "E966", {"start": v(9.3, -36.4) * mm, "end": v(8.72, -37) * mm});
            skLineSegment(sketch, "E967", {"start": v(8.72, -37) * mm, "end": v(8.1, -37.47) * mm});
            skLineSegment(sketch, "E968", {"start": v(8.1, -37.47) * mm, "end": v(7.6, -37.96) * mm});
            skLineSegment(sketch, "E969", {"start": v(7.6, -37.96) * mm, "end": v(7.35, -38.58) * mm});
            skLineSegment(sketch, "E970", {"start": v(7.35, -38.58) * mm, "end": v(7.3, -39.27) * mm});
            skLineSegment(sketch, "E971", {"start": v(7.3, -39.27) * mm, "end": v(7.37, -39.97) * mm});
            skLineSegment(sketch, "E972", {"start": v(7.37, -39.97) * mm, "end": v(7.53, -40.63) * mm});
            skLineSegment(sketch, "E973", {"start": v(7.53, -40.63) * mm, "end": v(7.72, -41.17) * mm});
            skLineSegment(sketch, "E974", {"start": v(7.72, -41.17) * mm, "end": v(7.87, -41.55) * mm});
            skLineSegment(sketch, "E975", {"start": v(7.87, -41.55) * mm, "end": v(7.93, -41.69) * mm});
            skLineSegment(sketch, "E976", {"start": v(6.96, -34.49) * mm, "end": v(7.07, -34.65) * mm});
            skLineSegment(sketch, "E977", {"start": v(7.07, -34.65) * mm, "end": v(7.34, -35.1) * mm});
            skLineSegment(sketch, "E978", {"start": v(7.34, -35.1) * mm, "end": v(7.69, -35.85) * mm});
            skLineSegment(sketch, "E979", {"start": v(7.69, -35.85) * mm, "end": v(8.03, -36.85) * mm});
            skLineSegment(sketch, "E980", {"start": v(8.03, -36.85) * mm, "end": v(8.29, -38.08) * mm});
            skLineSegment(sketch, "E981", {"start": v(8.29, -38.08) * mm, "end": v(8.37, -39.54) * mm});
            skLineSegment(sketch, "E982", {"start": v(8.37, -39.54) * mm, "end": v(8.21, -41.19) * mm});
            skLineSegment(sketch, "E983", {"start": v(8.21, -41.19) * mm, "end": v(7.71, -43.02) * mm});
            skLineSegment(sketch, "E984", {"start": v(7.71, -43.02) * mm, "end": v(7.69, -43.06) * mm});
            skLineSegment(sketch, "E985", {"start": v(7.69, -43.06) * mm, "end": v(7.62, -43.14) * mm});
            skLineSegment(sketch, "E986", {"start": v(7.62, -43.14) * mm, "end": v(7.5, -43.22) * mm});
            skLineSegment(sketch, "E987", {"start": v(7.5, -43.22) * mm, "end": v(7.36, -43.32) * mm});
            skLineSegment(sketch, "E988", {"start": v(7.36, -43.32) * mm, "end": v(7.17, -43.4) * mm});
            skLineSegment(sketch, "E989", {"start": v(7.17, -43.4) * mm, "end": v(6.92, -43.47) * mm});
            skLineSegment(sketch, "E990", {"start": v(6.92, -43.47) * mm, "end": v(6.64, -43.5) * mm});
            skLineSegment(sketch, "E991", {"start": v(6.64, -43.5) * mm, "end": v(6.3, -43.5) * mm});
            skLineSegment(sketch, "E992", {"start": v(6.3, -43.5) * mm, "end": v(6.08, -43.45) * mm});
            skLineSegment(sketch, "E993", {"start": v(6.08, -43.45) * mm, "end": v(5.88, -43.4) * mm});
            skLineSegment(sketch, "E994", {"start": v(5.88, -43.4) * mm, "end": v(5.7, -43.33) * mm});
            skLineSegment(sketch, "E995", {"start": v(5.7, -43.33) * mm, "end": v(5.56, -43.24) * mm});
            skLineSegment(sketch, "E996", {"start": v(5.56, -43.24) * mm, "end": v(5.43, -43.16) * mm});
            skLineSegment(sketch, "E997", {"start": v(5.43, -43.16) * mm, "end": v(5.33, -43.07) * mm});
            skLineSegment(sketch, "E998", {"start": v(5.33, -43.07) * mm, "end": v(5.26, -43) * mm});
            skLineSegment(sketch, "E999", {"start": v(5.26, -43) * mm, "end": v(5.22, -42.92) * mm});
            skLineSegment(sketch, "E1000", {"start": v(5.22, -42.92) * mm, "end": v(4.98, -42.2) * mm});
            skLineSegment(sketch, "E1001", {"start": v(4.98, -42.2) * mm, "end": v(4.86, -41.2) * mm});
            skLineSegment(sketch, "E1002", {"start": v(4.86, -41.2) * mm, "end": v(4.85, -40) * mm});
            skLineSegment(sketch, "E1003", {"start": v(4.85, -40) * mm, "end": v(4.98, -38.72) * mm});
            skLineSegment(sketch, "E1004", {"start": v(4.98, -38.72) * mm, "end": v(5.24, -37.43) * mm});
            skLineSegment(sketch, "E1005", {"start": v(5.24, -37.43) * mm, "end": v(5.66, -36.23) * mm});
            skLineSegment(sketch, "E1006", {"start": v(5.66, -36.23) * mm, "end": v(6.23, -35.22) * mm});
            skLineSegment(sketch, "E1007", {"start": v(6.23, -35.22) * mm, "end": v(6.96, -34.49) * mm});
            skLineSegment(sketch, "E1008", {"start": v(3.8, -37.26) * mm, "end": v(3.87, -37.35) * mm});
            skLineSegment(sketch, "E1009", {"start": v(3.87, -37.35) * mm, "end": v(4.06, -37.6) * mm});
            skLineSegment(sketch, "E1010", {"start": v(4.06, -37.6) * mm, "end": v(4.32, -38.01) * mm});
            skLineSegment(sketch, "E1011", {"start": v(4.32, -38.01) * mm, "end": v(4.6, -38.55) * mm});
            skLineSegment(sketch, "E1012", {"start": v(4.6, -38.55) * mm, "end": v(4.85, -39.18) * mm});
            skLineSegment(sketch, "E1013", {"start": v(4.85, -39.18) * mm, "end": v(5.03, -39.9) * mm});
            skLineSegment(sketch, "E1014", {"start": v(5.03, -39.9) * mm, "end": v(5.08, -40.7) * mm});
            skLineSegment(sketch, "E1015", {"start": v(5.08, -40.7) * mm, "end": v(4.95, -41.52) * mm});
            skLineSegment(sketch, "E1016", {"start": v(4.95, -41.52) * mm, "end": v(4.87, -41.81) * mm});
            skLineSegment(sketch, "E1017", {"start": v(4.87, -41.81) * mm, "end": v(4.8, -42.06) * mm});
            skLineSegment(sketch, "E1018", {"start": v(4.8, -42.06) * mm, "end": v(4.72, -42.28) * mm});
            skLineSegment(sketch, "E1019", {"start": v(4.72, -42.28) * mm, "end": v(4.64, -42.47) * mm});
            skLineSegment(sketch, "E1020", {"start": v(4.64, -42.47) * mm, "end": v(4.57, -42.63) * mm});
            skLineSegment(sketch, "E1021", {"start": v(4.57, -42.63) * mm, "end": v(4.49, -42.78) * mm});
            skLineSegment(sketch, "E1022", {"start": v(4.49, -42.78) * mm, "end": v(4.4, -42.9) * mm});
            skLineSegment(sketch, "E1023", {"start": v(4.4, -42.9) * mm, "end": v(4.3, -43.01) * mm});
            skLineSegment(sketch, "E1024", {"start": v(4.3, -43.01) * mm, "end": v(4.16, -43.18) * mm});
            skLineSegment(sketch, "E1025", {"start": v(4.16, -43.18) * mm, "end": v(4.02, -43.3) * mm});
            skLineSegment(sketch, "E1026", {"start": v(4.02, -43.3) * mm, "end": v(3.9, -43.38) * mm});
            skLineSegment(sketch, "E1027", {"start": v(3.9, -43.38) * mm, "end": v(3.78, -43.44) * mm});
            skLineSegment(sketch, "E1028", {"start": v(3.78, -43.44) * mm, "end": v(3.67, -43.48) * mm});
            skLineSegment(sketch, "E1029", {"start": v(3.67, -43.48) * mm, "end": v(3.54, -43.5) * mm});
            skLineSegment(sketch, "E1030", {"start": v(3.54, -43.5) * mm, "end": v(3.4, -43.5) * mm});
            skLineSegment(sketch, "E1031", {"start": v(3.4, -43.5) * mm, "end": v(3.22, -43.5) * mm});
            skLineSegment(sketch, "E1032", {"start": v(3.22, -43.5) * mm, "end": v(3.1, -43.49) * mm});
            skLineSegment(sketch, "E1033", {"start": v(3.1, -43.49) * mm, "end": v(3, -43.44) * mm});
            skLineSegment(sketch, "E1034", {"start": v(3, -43.44) * mm, "end": v(2.88, -43.38) * mm});
            skLineSegment(sketch, "E1035", {"start": v(2.88, -43.38) * mm, "end": v(2.78, -43.3) * mm});
            skLineSegment(sketch, "E1036", {"start": v(2.78, -43.3) * mm, "end": v(2.7, -43.2) * mm});
            skLineSegment(sketch, "E1037", {"start": v(2.7, -43.2) * mm, "end": v(2.61, -43.08) * mm});
            skLineSegment(sketch, "E1038", {"start": v(2.61, -43.08) * mm, "end": v(2.54, -42.97) * mm});
            skLineSegment(sketch, "E1039", {"start": v(2.54, -42.97) * mm, "end": v(2.49, -42.85) * mm});
            skLineSegment(sketch, "E1040", {"start": v(2.49, -42.85) * mm, "end": v(2.33, -42.34) * mm});
            skLineSegment(sketch, "E1041", {"start": v(2.33, -42.34) * mm, "end": v(2.22, -41.7) * mm});
            skLineSegment(sketch, "E1042", {"start": v(2.22, -41.7) * mm, "end": v(2.19, -41) * mm});
            skLineSegment(sketch, "E1043", {"start": v(2.19, -41) * mm, "end": v(2.25, -40.22) * mm});
            skLineSegment(sketch, "E1044", {"start": v(2.25, -40.22) * mm, "end": v(2.41, -39.43) * mm});
            skLineSegment(sketch, "E1045", {"start": v(2.41, -39.43) * mm, "end": v(2.72, -38.65) * mm});
            skLineSegment(sketch, "E1046", {"start": v(2.72, -38.65) * mm, "end": v(3.17, -37.92) * mm});
            skLineSegment(sketch, "E1047", {"start": v(3.17, -37.92) * mm, "end": v(3.8, -37.26) * mm});
            skLineSegment(sketch, "E1048", {"start": v(1.25, -38.11) * mm, "end": v(1.32, -38.2) * mm});
            skLineSegment(sketch, "E1049", {"start": v(1.32, -38.2) * mm, "end": v(1.5, -38.42) * mm});
            skLineSegment(sketch, "E1050", {"start": v(1.5, -38.42) * mm, "end": v(1.73, -38.77) * mm});
            skLineSegment(sketch, "E1051", {"start": v(1.73, -38.77) * mm, "end": v(1.99, -39.22) * mm});
            skLineSegment(sketch, "E1052", {"start": v(1.99, -39.22) * mm, "end": v(2.22, -39.77) * mm});
            skLineSegment(sketch, "E1053", {"start": v(2.22, -39.77) * mm, "end": v(2.38, -40.4) * mm});
            skLineSegment(sketch, "E1054", {"start": v(2.38, -40.4) * mm, "end": v(2.42, -41.08) * mm});
            skLineSegment(sketch, "E1055", {"start": v(2.42, -41.08) * mm, "end": v(2.3, -41.8) * mm});
            skLineSegment(sketch, "E1056", {"start": v(2.3, -41.8) * mm, "end": v(2.24, -42.02) * mm});
            skLineSegment(sketch, "E1057", {"start": v(2.24, -42.02) * mm, "end": v(2.17, -42.23) * mm});
            skLineSegment(sketch, "E1058", {"start": v(2.17, -42.23) * mm, "end": v(2.1, -42.42) * mm});
            skLineSegment(sketch, "E1059", {"start": v(2.1, -42.42) * mm, "end": v(2.02, -42.6) * mm});
            skLineSegment(sketch, "E1060", {"start": v(2.02, -42.6) * mm, "end": v(1.94, -42.74) * mm});
            skLineSegment(sketch, "E1061", {"start": v(1.94, -42.74) * mm, "end": v(1.87, -42.88) * mm});
            skLineSegment(sketch, "E1062", {"start": v(1.87, -42.88) * mm, "end": v(1.79, -43) * mm});
            skLineSegment(sketch, "E1063", {"start": v(1.79, -43) * mm, "end": v(1.71, -43.1) * mm});
            skLineSegment(sketch, "E1064", {"start": v(1.71, -43.1) * mm, "end": v(1.63, -43.19) * mm});
            skLineSegment(sketch, "E1065", {"start": v(1.63, -43.19) * mm, "end": v(1.55, -43.27) * mm});
            skLineSegment(sketch, "E1066", {"start": v(1.55, -43.27) * mm, "end": v(1.47, -43.34) * mm});
            skLineSegment(sketch, "E1067", {"start": v(1.47, -43.34) * mm, "end": v(1.37, -43.4) * mm});
            skLineSegment(sketch, "E1068", {"start": v(1.37, -43.4) * mm, "end": v(1.27, -43.44) * mm});
            skLineSegment(sketch, "E1069", {"start": v(1.27, -43.44) * mm, "end": v(1.14, -43.47) * mm});
            skLineSegment(sketch, "E1070", {"start": v(1.14, -43.47) * mm, "end": v(1, -43.5) * mm});
            skLineSegment(sketch, "E1071", {"start": v(1, -43.5) * mm, "end": v(0.84, -43.5) * mm});
            skLineSegment(sketch, "E1072", {"start": v(0.84, -43.5) * mm, "end": v(0.68, -43.49) * mm});
            skLineSegment(sketch, "E1073", {"start": v(0.68, -43.49) * mm, "end": v(0.53, -43.45) * mm});
            skLineSegment(sketch, "E1074", {"start": v(0.53, -43.45) * mm, "end": v(0.42, -43.4) * mm});
            skLineSegment(sketch, "E1075", {"start": v(0.42, -43.4) * mm, "end": v(0.32, -43.33) * mm});
            skLineSegment(sketch, "E1076", {"start": v(0.32, -43.33) * mm, "end": v(0.24, -43.25) * mm});
            skLineSegment(sketch, "E1077", {"start": v(0.24, -43.25) * mm, "end": v(0.18, -43.18) * mm});
            skLineSegment(sketch, "E1078", {"start": v(0.18, -43.18) * mm, "end": v(0.14, -43.1) * mm});
            skLineSegment(sketch, "E1079", {"start": v(0.14, -43.1) * mm, "end": v(0.1, -43.05) * mm});
            skLineSegment(sketch, "E1080", {"start": v(0.1, -43.05) * mm, "end": v(-0.04, -42.6) * mm});
            skLineSegment(sketch, "E1081", {"start": v(-0.04, -42.6) * mm, "end": v(-0.14, -42.04) * mm});
            skLineSegment(sketch, "E1082", {"start": v(-0.14, -42.04) * mm, "end": v(-0.17, -41.4) * mm});
            skLineSegment(sketch, "E1083", {"start": v(-0.17, -41.4) * mm, "end": v(-0.13, -40.72) * mm});
            skLineSegment(sketch, "E1084", {"start": v(-0.13, -40.72) * mm, "end": v(0.02, -40.02) * mm});
            skLineSegment(sketch, "E1085", {"start": v(0.02, -40.02) * mm, "end": v(0.28, -39.33) * mm});
            skLineSegment(sketch, "E1086", {"start": v(0.28, -39.33) * mm, "end": v(0.69, -38.69) * mm});
            skLineSegment(sketch, "E1087", {"start": v(0.69, -38.69) * mm, "end": v(1.25, -38.11) * mm});
            skLineSegment(sketch, "E1088", {"start": v(-0.05, 39.46) * mm, "end": v(0.17, 39.39) * mm});
            skLineSegment(sketch, "E1089", {"start": v(0.17, 39.39) * mm, "end": v(0.33, 39.19) * mm});
            skLineSegment(sketch, "E1090", {"start": v(0.33, 39.19) * mm, "end": v(0.43, 38.88) * mm});
            skLineSegment(sketch, "E1091", {"start": v(0.43, 38.88) * mm, "end": v(0.5, 38.48) * mm});
            skLineSegment(sketch, "E1092", {"start": v(0.5, 38.48) * mm, "end": v(0.53, 38.02) * mm});
            skLineSegment(sketch, "E1093", {"start": v(0.53, 38.02) * mm, "end": v(0.56, 37.51) * mm});
            skLineSegment(sketch, "E1094", {"start": v(0.56, 37.51) * mm, "end": v(0.58, 36.98) * mm});
            skLineSegment(sketch, "E1095", {"start": v(0.58, 36.98) * mm, "end": v(0.62, 36.45) * mm});
            skLineSegment(sketch, "E1096", {"start": v(0.62, 36.45) * mm, "end": v(0.69, 35.95) * mm});
            skLineSegment(sketch, "E1097", {"start": v(0.69, 35.95) * mm, "end": v(0.8, 35.49) * mm});
            skLineSegment(sketch, "E1098", {"start": v(0.8, 35.49) * mm, "end": v(0.97, 35.07) * mm});
            skLineSegment(sketch, "E1099", {"start": v(0.97, 35.07) * mm, "end": v(1.17, 34.71) * mm});
            skLineSegment(sketch, "E1100", {"start": v(1.17, 34.71) * mm, "end": v(1.42, 34.41) * mm});
            skLineSegment(sketch, "E1101", {"start": v(1.42, 34.41) * mm, "end": v(1.72, 34.18) * mm});
            skLineSegment(sketch, "E1102", {"start": v(1.72, 34.18) * mm, "end": v(2.07, 34.02) * mm});
            skLineSegment(sketch, "E1103", {"start": v(2.07, 34.02) * mm, "end": v(2.47, 33.93) * mm});
            skLineSegment(sketch, "E1104", {"start": v(2.47, 33.93) * mm, "end": v(2.86, 33.95) * mm});
            skLineSegment(sketch, "E1105", {"start": v(2.86, 33.95) * mm, "end": v(3.2, 34.04) * mm});
            skLineSegment(sketch, "E1106", {"start": v(3.2, 34.04) * mm, "end": v(3.47, 34.2) * mm});
            skLineSegment(sketch, "E1107", {"start": v(3.47, 34.2) * mm, "end": v(3.69, 34.38) * mm});
            skLineSegment(sketch, "E1108", {"start": v(3.69, 34.38) * mm, "end": v(3.86, 34.57) * mm});
            skLineSegment(sketch, "E1109", {"start": v(3.86, 34.57) * mm, "end": v(3.98, 34.73) * mm});
            skLineSegment(sketch, "E1110", {"start": v(3.98, 34.73) * mm, "end": v(4.04, 34.85) * mm});
            skLineSegment(sketch, "E1111", {"start": v(4.04, 34.85) * mm, "end": v(4.07, 34.9) * mm});
            skLineSegment(sketch, "E1112", {"start": v(4.07, 34.9) * mm, "end": v(3.49, 35.36) * mm});
            skLineSegment(sketch, "E1113", {"start": v(3.49, 35.36) * mm, "end": v(3.2, 35.88) * mm});
            skLineSegment(sketch, "E1114", {"start": v(3.2, 35.88) * mm, "end": v(3.15, 36.42) * mm});
            skLineSegment(sketch, "E1115", {"start": v(3.15, 36.42) * mm, "end": v(3.27, 36.96) * mm});
            skLineSegment(sketch, "E1116", {"start": v(3.27, 36.96) * mm, "end": v(3.5, 37.47) * mm});
            skLineSegment(sketch, "E1117", {"start": v(3.5, 37.47) * mm, "end": v(3.8, 37.9) * mm});
            skLineSegment(sketch, "E1118", {"start": v(3.8, 37.9) * mm, "end": v(4.08, 38.26) * mm});
            skLineSegment(sketch, "E1119", {"start": v(4.08, 38.26) * mm, "end": v(4.3, 38.5) * mm});
            skLineSegment(sketch, "E1120", {"start": v(4.3, 38.5) * mm, "end": v(4.49, 38.68) * mm});
            skLineSegment(sketch, "E1121", {"start": v(4.49, 38.68) * mm, "end": v(4.74, 38.92) * mm});
            skLineSegment(sketch, "E1122", {"start": v(4.74, 38.92) * mm, "end": v(5.04, 39.2) * mm});
            skLineSegment(sketch, "E1123", {"start": v(5.04, 39.2) * mm, "end": v(5.4, 39.48) * mm});
            skLineSegment(sketch, "E1124", {"start": v(5.4, 39.48) * mm, "end": v(5.8, 39.76) * mm});
            skLineSegment(sketch, "E1125", {"start": v(5.8, 39.76) * mm, "end": v(6.26, 40.03) * mm});
            skLineSegment(sketch, "E1126", {"start": v(6.26, 40.03) * mm, "end": v(6.76, 40.25) * mm});
            skLineSegment(sketch, "E1127", {"start": v(6.76, 40.25) * mm, "end": v(7.3, 40.42) * mm});
            skLineSegment(sketch, "E1128", {"start": v(7.3, 40.42) * mm, "end": v(7.79, 40.52) * mm});
            skLineSegment(sketch, "E1129", {"start": v(7.79, 40.52) * mm, "end": v(8.14, 40.53) * mm});
            skLineSegment(sketch, "E1130", {"start": v(8.14, 40.53) * mm, "end": v(8.38, 40.47) * mm});
            skLineSegment(sketch, "E1131", {"start": v(8.38, 40.47) * mm, "end": v(8.53, 40.36) * mm});
            skLineSegment(sketch, "E1132", {"start": v(8.53, 40.36) * mm, "end": v(8.6, 40.21) * mm});
            skLineSegment(sketch, "E1133", {"start": v(8.6, 40.21) * mm, "end": v(8.62, 40.05) * mm});
            skLineSegment(sketch, "E1134", {"start": v(8.62, 40.05) * mm, "end": v(8.6, 39.88) * mm});
            skLineSegment(sketch, "E1135", {"start": v(8.6, 39.88) * mm, "end": v(8.59, 39.73) * mm});
            skLineSegment(sketch, "E1136", {"start": v(8.59, 39.73) * mm, "end": v(8.62, 39.59) * mm});
            skLineSegment(sketch, "E1137", {"start": v(8.62, 39.59) * mm, "end": v(8.75, 39.47) * mm});
            skLineSegment(sketch, "E1138", {"start": v(8.75, 39.47) * mm, "end": v(8.94, 39.38) * mm});
            skLineSegment(sketch, "E1139", {"start": v(8.94, 39.38) * mm, "end": v(9.16, 39.34) * mm});
            skLineSegment(sketch, "E1140", {"start": v(9.16, 39.34) * mm, "end": v(9.4, 39.36) * mm});
            skLineSegment(sketch, "E1141", {"start": v(9.4, 39.36) * mm, "end": v(9.6, 39.47) * mm});
            skLineSegment(sketch, "E1142", {"start": v(9.6, 39.47) * mm, "end": v(9.75, 39.68) * mm});
            skLineSegment(sketch, "E1143", {"start": v(9.75, 39.68) * mm, "end": v(9.82, 40) * mm});
            skLineSegment(sketch, "E1144", {"start": v(9.82, 40) * mm, "end": v(9.82, 40.4) * mm});
            skLineSegment(sketch, "E1145", {"start": v(9.82, 40.4) * mm, "end": v(9.76, 40.8) * mm});
            skLineSegment(sketch, "E1146", {"start": v(9.76, 40.8) * mm, "end": v(9.64, 41.22) * mm});
            skLineSegment(sketch, "E1147", {"start": v(9.64, 41.22) * mm, "end": v(9.44, 41.63) * mm});
            skLineSegment(sketch, "E1148", {"start": v(9.44, 41.63) * mm, "end": v(9.17, 42.02) * mm});
            skLineSegment(sketch, "E1149", {"start": v(9.17, 42.02) * mm, "end": v(8.8, 42.38) * mm});
            skLineSegment(sketch, "E1150", {"start": v(8.8, 42.38) * mm, "end": v(8.33, 42.7) * mm});
            skLineSegment(sketch, "E1151", {"start": v(8.33, 42.7) * mm, "end": v(7.75, 42.94) * mm});
            skLineSegment(sketch, "E1152", {"start": v(7.75, 42.94) * mm, "end": v(7, 43.08) * mm});
            skLineSegment(sketch, "E1153", {"start": v(7, 43.08) * mm, "end": v(6.07, 43.05) * mm});
            skLineSegment(sketch, "E1154", {"start": v(6.07, 43.05) * mm, "end": v(5, 42.92) * mm});
            skLineSegment(sketch, "E1155", {"start": v(5, 42.92) * mm, "end": v(3.87, 42.71) * mm});
            skLineSegment(sketch, "E1156", {"start": v(3.87, 42.71) * mm, "end": v(2.74, 42.48) * mm});
            skLineSegment(sketch, "E1157", {"start": v(2.74, 42.48) * mm, "end": v(1.67, 42.26) * mm});
            skLineSegment(sketch, "E1158", {"start": v(1.67, 42.26) * mm, "end": v(0.72, 42.1) * mm});
            skLineSegment(sketch, "E1159", {"start": v(0.72, 42.1) * mm, "end": v(-0.05, 42.03) * mm});
            skLineSegment(sketch, "E1160", {"start": v(-0.05, 42.03) * mm, "end": v(-0.82, 42.1) * mm});
            skLineSegment(sketch, "E1161", {"start": v(-0.82, 42.1) * mm, "end": v(-1.77, 42.26) * mm});
            skLineSegment(sketch, "E1162", {"start": v(-1.77, 42.26) * mm, "end": v(-2.84, 42.48) * mm});
            skLineSegment(sketch, "E1163", {"start": v(-2.84, 42.48) * mm, "end": v(-3.97, 42.71) * mm});
            skLineSegment(sketch, "E1164", {"start": v(-3.97, 42.71) * mm, "end": v(-5.1, 42.92) * mm});
            skLineSegment(sketch, "E1165", {"start": v(-5.1, 42.92) * mm, "end": v(-6.17, 43.05) * mm});
            skLineSegment(sketch, "E1166", {"start": v(-6.17, 43.05) * mm, "end": v(-7.1, 43.08) * mm});
            skLineSegment(sketch, "E1167", {"start": v(-7.1, 43.08) * mm, "end": v(-7.85, 42.94) * mm});
            skLineSegment(sketch, "E1168", {"start": v(-7.85, 42.94) * mm, "end": v(-8.43, 42.7) * mm});
            skLineSegment(sketch, "E1169", {"start": v(-8.43, 42.7) * mm, "end": v(-8.9, 42.38) * mm});
            skLineSegment(sketch, "E1170", {"start": v(-8.9, 42.38) * mm, "end": v(-9.26, 42.02) * mm});
            skLineSegment(sketch, "E1171", {"start": v(-9.26, 42.02) * mm, "end": v(-9.54, 41.63) * mm});
            skLineSegment(sketch, "E1172", {"start": v(-9.54, 41.63) * mm, "end": v(-9.73, 41.22) * mm});
            skLineSegment(sketch, "E1173", {"start": v(-9.73, 41.22) * mm, "end": v(-9.86, 40.8) * mm});
            skLineSegment(sketch, "E1174", {"start": v(-9.86, 40.8) * mm, "end": v(-9.91, 40.4) * mm});
            skLineSegment(sketch, "E1175", {"start": v(-9.91, 40.4) * mm, "end": v(-9.92, 40) * mm});
            skLineSegment(sketch, "E1176", {"start": v(-9.92, 40) * mm, "end": v(-9.85, 39.68) * mm});
            skLineSegment(sketch, "E1177", {"start": v(-9.85, 39.68) * mm, "end": v(-9.7, 39.47) * mm});
            skLineSegment(sketch, "E1178", {"start": v(-9.7, 39.47) * mm, "end": v(-9.5, 39.36) * mm});
            skLineSegment(sketch, "E1179", {"start": v(-9.5, 39.36) * mm, "end": v(-9.26, 39.34) * mm});
            skLineSegment(sketch, "E1180", {"start": v(-9.26, 39.34) * mm, "end": v(-9.04, 39.38) * mm});
            skLineSegment(sketch, "E1181", {"start": v(-9.04, 39.38) * mm, "end": v(-8.85, 39.47) * mm});
            skLineSegment(sketch, "E1182", {"start": v(-8.85, 39.47) * mm, "end": v(-8.72, 39.59) * mm});
            skLineSegment(sketch, "E1183", {"start": v(-8.72, 39.59) * mm, "end": v(-8.68, 39.73) * mm});
            skLineSegment(sketch, "E1184", {"start": v(-8.68, 39.73) * mm, "end": v(-8.7, 39.88) * mm});
            skLineSegment(sketch, "E1185", {"start": v(-8.7, 39.88) * mm, "end": v(-8.72, 40.05) * mm});
            skLineSegment(sketch, "E1186", {"start": v(-8.72, 40.05) * mm, "end": v(-8.7, 40.21) * mm});
            skLineSegment(sketch, "E1187", {"start": v(-8.7, 40.21) * mm, "end": v(-8.62, 40.36) * mm});
            skLineSegment(sketch, "E1188", {"start": v(-8.62, 40.36) * mm, "end": v(-8.48, 40.47) * mm});
            skLineSegment(sketch, "E1189", {"start": v(-8.48, 40.47) * mm, "end": v(-8.24, 40.53) * mm});
            skLineSegment(sketch, "E1190", {"start": v(-8.24, 40.53) * mm, "end": v(-7.89, 40.52) * mm});
            skLineSegment(sketch, "E1191", {"start": v(-7.89, 40.52) * mm, "end": v(-7.4, 40.42) * mm});
            skLineSegment(sketch, "E1192", {"start": v(-7.4, 40.42) * mm, "end": v(-6.85, 40.25) * mm});
            skLineSegment(sketch, "E1193", {"start": v(-6.85, 40.25) * mm, "end": v(-6.35, 40.03) * mm});
            skLineSegment(sketch, "E1194", {"start": v(-6.35, 40.03) * mm, "end": v(-5.9, 39.76) * mm});
            skLineSegment(sketch, "E1195", {"start": v(-5.9, 39.76) * mm, "end": v(-5.5, 39.48) * mm});
            skLineSegment(sketch, "E1196", {"start": v(-5.5, 39.48) * mm, "end": v(-5.14, 39.2) * mm});
            skLineSegment(sketch, "E1197", {"start": v(-5.14, 39.2) * mm, "end": v(-4.83, 38.92) * mm});
            skLineSegment(sketch, "E1198", {"start": v(-4.83, 38.92) * mm, "end": v(-4.58, 38.68) * mm});
            skLineSegment(sketch, "E1199", {"start": v(-4.58, 38.68) * mm, "end": v(-4.4, 38.5) * mm});
            skLineSegment(sketch, "E1200", {"start": v(-4.4, 38.5) * mm, "end": v(-4.18, 38.26) * mm});
            skLineSegment(sketch, "E1201", {"start": v(-4.18, 38.26) * mm, "end": v(-3.9, 37.9) * mm});
            skLineSegment(sketch, "E1202", {"start": v(-3.9, 37.9) * mm, "end": v(-3.6, 37.47) * mm});
            skLineSegment(sketch, "E1203", {"start": v(-3.6, 37.47) * mm, "end": v(-3.37, 36.96) * mm});
            skLineSegment(sketch, "E1204", {"start": v(-3.37, 36.96) * mm, "end": v(-3.25, 36.42) * mm});
            skLineSegment(sketch, "E1205", {"start": v(-3.25, 36.42) * mm, "end": v(-3.3, 35.88) * mm});
            skLineSegment(sketch, "E1206", {"start": v(-3.3, 35.88) * mm, "end": v(-3.58, 35.36) * mm});
            skLineSegment(sketch, "E1207", {"start": v(-3.58, 35.36) * mm, "end": v(-4.17, 34.9) * mm});
            skLineSegment(sketch, "E1208", {"start": v(-4.17, 34.9) * mm, "end": v(-4.14, 34.85) * mm});
            skLineSegment(sketch, "E1209", {"start": v(-4.14, 34.85) * mm, "end": v(-4.07, 34.73) * mm});
            skLineSegment(sketch, "E1210", {"start": v(-4.07, 34.73) * mm, "end": v(-3.95, 34.57) * mm});
            skLineSegment(sketch, "E1211", {"start": v(-3.95, 34.57) * mm, "end": v(-3.79, 34.38) * mm});
            skLineSegment(sketch, "E1212", {"start": v(-3.79, 34.38) * mm, "end": v(-3.56, 34.2) * mm});
            skLineSegment(sketch, "E1213", {"start": v(-3.56, 34.2) * mm, "end": v(-3.29, 34.04) * mm});
            skLineSegment(sketch, "E1214", {"start": v(-3.29, 34.04) * mm, "end": v(-2.95, 33.95) * mm});
            skLineSegment(sketch, "E1215", {"start": v(-2.95, 33.95) * mm, "end": v(-2.56, 33.93) * mm});
            skLineSegment(sketch, "E1216", {"start": v(-2.56, 33.93) * mm, "end": v(-2.17, 34.02) * mm});
            skLineSegment(sketch, "E1217", {"start": v(-2.17, 34.02) * mm, "end": v(-1.82, 34.18) * mm});
            skLineSegment(sketch, "E1218", {"start": v(-1.82, 34.18) * mm, "end": v(-1.52, 34.41) * mm});
            skLineSegment(sketch, "E1219", {"start": v(-1.52, 34.41) * mm, "end": v(-1.27, 34.71) * mm});
            skLineSegment(sketch, "E1220", {"start": v(-1.27, 34.71) * mm, "end": v(-1.06, 35.07) * mm});
            skLineSegment(sketch, "E1221", {"start": v(-1.06, 35.07) * mm, "end": v(-0.9, 35.49) * mm});
            skLineSegment(sketch, "E1222", {"start": v(-0.9, 35.49) * mm, "end": v(-0.79, 35.95) * mm});
            skLineSegment(sketch, "E1223", {"start": v(-0.79, 35.95) * mm, "end": v(-0.72, 36.45) * mm});
            skLineSegment(sketch, "E1224", {"start": v(-0.72, 36.45) * mm, "end": v(-0.68, 36.98) * mm});
            skLineSegment(sketch, "E1225", {"start": v(-0.68, 36.98) * mm, "end": v(-0.65, 37.51) * mm});
            skLineSegment(sketch, "E1226", {"start": v(-0.65, 37.51) * mm, "end": v(-0.63, 38.02) * mm});
            skLineSegment(sketch, "E1227", {"start": v(-0.63, 38.02) * mm, "end": v(-0.6, 38.48) * mm});
            skLineSegment(sketch, "E1228", {"start": v(-0.6, 38.48) * mm, "end": v(-0.53, 38.88) * mm});
            skLineSegment(sketch, "E1229", {"start": v(-0.53, 38.88) * mm, "end": v(-0.43, 39.19) * mm});
            skLineSegment(sketch, "E1230", {"start": v(-0.43, 39.19) * mm, "end": v(-0.27, 39.39) * mm});
            skLineSegment(sketch, "E1231", {"start": v(-0.27, 39.39) * mm, "end": v(-0.05, 39.46) * mm});
            skLineSegment(sketch, "E1232", {"start": v(-37.92, 56.2) * mm, "end": v(-37.78, 56.47) * mm});
            skLineSegment(sketch, "E1233", {"start": v(-37.78, 56.47) * mm, "end": v(-37.27, 56.81) * mm});
            skLineSegment(sketch, "E1234", {"start": v(-37.27, 56.81) * mm, "end": v(-36.43, 57.2) * mm});
            skLineSegment(sketch, "E1235", {"start": v(-36.43, 57.2) * mm, "end": v(-35.3, 57.57) * mm});
            skLineSegment(sketch, "E1236", {"start": v(-35.3, 57.57) * mm, "end": v(-33.91, 57.89) * mm});
            skLineSegment(sketch, "E1237", {"start": v(-33.91, 57.89) * mm, "end": v(-32.3, 58.1) * mm});
            skLineSegment(sketch, "E1238", {"start": v(-32.3, 58.1) * mm, "end": v(-30.5, 58.17) * mm});
            skLineSegment(sketch, "E1239", {"start": v(-30.5, 58.17) * mm, "end": v(-28.56, 58.05) * mm});
            skLineSegment(sketch, "E1240", {"start": v(-28.56, 58.05) * mm, "end": v(-26.83, 57.71) * mm});
            skLineSegment(sketch, "E1241", {"start": v(-26.83, 57.71) * mm, "end": v(-25.24, 57.17) * mm});
            skLineSegment(sketch, "E1242", {"start": v(-25.24, 57.17) * mm, "end": v(-23.78, 56.48) * mm});
            skLineSegment(sketch, "E1243", {"start": v(-23.78, 56.48) * mm, "end": v(-22.45, 55.7) * mm});
            skLineSegment(sketch, "E1244", {"start": v(-22.45, 55.7) * mm, "end": v(-21.22, 54.88) * mm});
            skLineSegment(sketch, "E1245", {"start": v(-21.22, 54.88) * mm, "end": v(-20.1, 54.08) * mm});
            skLineSegment(sketch, "E1246", {"start": v(-20.1, 54.08) * mm, "end": v(-19.07, 53.37) * mm});
            skLineSegment(sketch, "E1247", {"start": v(-19.07, 53.37) * mm, "end": v(-18.12, 52.8) * mm});
            skLineSegment(sketch, "E1248", {"start": v(-18.12, 52.8) * mm, "end": v(-17.27, 52.39) * mm});
            skLineSegment(sketch, "E1249", {"start": v(-17.27, 52.39) * mm, "end": v(-16.29, 52) * mm});
            skLineSegment(sketch, "E1250", {"start": v(-16.29, 52) * mm, "end": v(-15.24, 51.67) * mm});
            skLineSegment(sketch, "E1251", {"start": v(-15.24, 51.67) * mm, "end": v(-14.15, 51.4) * mm});
            skLineSegment(sketch, "E1252", {"start": v(-14.15, 51.4) * mm, "end": v(-13.07, 51.2) * mm});
            skLineSegment(sketch, "E1253", {"start": v(-13.07, 51.2) * mm, "end": v(-12.03, 51.11) * mm});
            skLineSegment(sketch, "E1254", {"start": v(-12.03, 51.11) * mm, "end": v(-11.09, 51.13) * mm});
            skLineSegment(sketch, "E1255", {"start": v(-11.09, 51.13) * mm, "end": v(-10.28, 51.28) * mm});
            skLineSegment(sketch, "E1256", {"start": v(-10.28, 51.28) * mm, "end": v(-9.64, 51.39) * mm});
            skLineSegment(sketch, "E1257", {"start": v(-9.64, 51.39) * mm, "end": v(-9.17, 51.29) * mm});
            skLineSegment(sketch, "E1258", {"start": v(-9.17, 51.29) * mm, "end": v(-8.86, 51.04) * mm});
            skLineSegment(sketch, "E1259", {"start": v(-8.86, 51.04) * mm, "end": v(-8.69, 50.7) * mm});
            skLineSegment(sketch, "E1260", {"start": v(-8.69, 50.7) * mm, "end": v(-8.63, 50.3) * mm});
            skLineSegment(sketch, "E1261", {"start": v(-8.63, 50.3) * mm, "end": v(-8.68, 49.9) * mm});
            skLineSegment(sketch, "E1262", {"start": v(-8.68, 49.9) * mm, "end": v(-8.8, 49.56) * mm});
            skLineSegment(sketch, "E1263", {"start": v(-8.8, 49.56) * mm, "end": v(-9, 49.33) * mm});
            skLineSegment(sketch, "E1264", {"start": v(-9, 49.33) * mm, "end": v(-9.22, 49.2) * mm});
            skLineSegment(sketch, "E1265", {"start": v(-9.22, 49.2) * mm, "end": v(-9.44, 49.1) * mm});
            skLineSegment(sketch, "E1266", {"start": v(-9.44, 49.1) * mm, "end": v(-9.7, 49.04) * mm});
            skLineSegment(sketch, "E1267", {"start": v(-9.7, 49.04) * mm, "end": v(-10.02, 49.04) * mm});
            skLineSegment(sketch, "E1268", {"start": v(-10.02, 49.04) * mm, "end": v(-10.44, 49.1) * mm});
            skLineSegment(sketch, "E1269", {"start": v(-10.44, 49.1) * mm, "end": v(-10.99, 49.24) * mm});
            skLineSegment(sketch, "E1270", {"start": v(-10.99, 49.24) * mm, "end": v(-11.68, 49.45) * mm});
            skLineSegment(sketch, "E1271", {"start": v(-11.68, 49.45) * mm, "end": v(-12.57, 49.76) * mm});
            skLineSegment(sketch, "E1272", {"start": v(-12.57, 49.76) * mm, "end": v(-13, 49.9) * mm});
            skLineSegment(sketch, "E1273", {"start": v(-13, 49.9) * mm, "end": v(-13.47, 50.02) * mm});
            skLineSegment(sketch, "E1274", {"start": v(-13.47, 50.02) * mm, "end": v(-13.97, 50.13) * mm});
            skLineSegment(sketch, "E1275", {"start": v(-13.97, 50.13) * mm, "end": v(-14.5, 50.23) * mm});
            skLineSegment(sketch, "E1276", {"start": v(-14.5, 50.23) * mm, "end": v(-15.03, 50.32) * mm});
            skLineSegment(sketch, "E1277", {"start": v(-15.03, 50.32) * mm, "end": v(-15.58, 50.4) * mm});
            skLineSegment(sketch, "E1278", {"start": v(-15.58, 50.4) * mm, "end": v(-16.13, 50.48) * mm});
            skLineSegment(sketch, "E1279", {"start": v(-16.13, 50.48) * mm, "end": v(-16.69, 50.55) * mm});
            skLineSegment(sketch, "E1280", {"start": v(-16.69, 50.55) * mm, "end": v(-18.21, 50.65) * mm});
            skLineSegment(sketch, "E1281", {"start": v(-18.21, 50.65) * mm, "end": v(-19.72, 50.6) * mm});
            skLineSegment(sketch, "E1282", {"start": v(-19.72, 50.6) * mm, "end": v(-21.2, 50.45) * mm});
            skLineSegment(sketch, "E1283", {"start": v(-21.2, 50.45) * mm, "end": v(-22.63, 50.24) * mm});
            skLineSegment(sketch, "E1284", {"start": v(-22.63, 50.24) * mm, "end": v(-24, 50.02) * mm});
            skLineSegment(sketch, "E1285", {"start": v(-24, 50.02) * mm, "end": v(-25.29, 49.82) * mm});
            skLineSegment(sketch, "E1286", {"start": v(-25.29, 49.82) * mm, "end": v(-26.47, 49.68) * mm});
            skLineSegment(sketch, "E1287", {"start": v(-26.47, 49.68) * mm, "end": v(-27.54, 49.66) * mm});
            skLineSegment(sketch, "E1288", {"start": v(-27.54, 49.66) * mm, "end": v(-29.5, 49.84) * mm});
            skLineSegment(sketch, "E1289", {"start": v(-29.5, 49.84) * mm, "end": v(-31.3, 50.2) * mm});
            skLineSegment(sketch, "E1290", {"start": v(-31.3, 50.2) * mm, "end": v(-32.94, 50.75) * mm});
            skLineSegment(sketch, "E1291", {"start": v(-32.94, 50.75) * mm, "end": v(-34.38, 51.47) * mm});
            skLineSegment(sketch, "E1292", {"start": v(-34.38, 51.47) * mm, "end": v(-35.61, 52.37) * mm});
            skLineSegment(sketch, "E1293", {"start": v(-35.61, 52.37) * mm, "end": v(-36.63, 53.46) * mm});
            skLineSegment(sketch, "E1294", {"start": v(-36.63, 53.46) * mm, "end": v(-37.4, 54.74) * mm});
            skLineSegment(sketch, "E1295", {"start": v(-37.4, 54.74) * mm, "end": v(-37.92, 56.2) * mm});
            skLineSegment(sketch, "E1296", {"start": v(-28.76, 56.87) * mm, "end": v(-28.86, 56.9) * mm});
            skLineSegment(sketch, "E1297", {"start": v(-28.86, 56.9) * mm, "end": v(-29.15, 56.96) * mm});
            skLineSegment(sketch, "E1298", {"start": v(-29.15, 56.96) * mm, "end": v(-29.59, 57.04) * mm});
            skLineSegment(sketch, "E1299", {"start": v(-29.59, 57.04) * mm, "end": v(-30.12, 57.12) * mm});
            skLineSegment(sketch, "E1300", {"start": v(-30.12, 57.12) * mm, "end": v(-30.7, 57.17) * mm});
            skLineSegment(sketch, "E1301", {"start": v(-30.7, 57.17) * mm, "end": v(-31.3, 57.17) * mm});
            skLineSegment(sketch, "E1302", {"start": v(-31.3, 57.17) * mm, "end": v(-31.87, 57.1) * mm});
            skLineSegment(sketch, "E1303", {"start": v(-31.87, 57.1) * mm, "end": v(-32.36, 56.95) * mm});
            skLineSegment(sketch, "E1304", {"start": v(-32.36, 56.95) * mm, "end": v(-32.4, 56.7) * mm});
            skLineSegment(sketch, "E1305", {"start": v(-32.4, 56.7) * mm, "end": v(-32.44, 56.05) * mm});
            skLineSegment(sketch, "E1306", {"start": v(-32.44, 56.05) * mm, "end": v(-32.42, 55.1) * mm});
            skLineSegment(sketch, "E1307", {"start": v(-32.42, 55.1) * mm, "end": v(-32.25, 54) * mm});
            skLineSegment(sketch, "E1308", {"start": v(-32.25, 54) * mm, "end": v(-31.84, 52.86) * mm});
            skLineSegment(sketch, "E1309", {"start": v(-31.84, 52.86) * mm, "end": v(-31.1, 51.82) * mm});
            skLineSegment(sketch, "E1310", {"start": v(-31.1, 51.82) * mm, "end": v(-29.95, 51) * mm});
            skLineSegment(sketch, "E1311", {"start": v(-29.95, 51) * mm, "end": v(-28.32, 50.5) * mm});
            skLineSegment(sketch, "E1312", {"start": v(-28.32, 50.5) * mm, "end": v(-26.7, 50.46) * mm});
            skLineSegment(sketch, "E1313", {"start": v(-26.7, 50.46) * mm, "end": v(-25.42, 50.76) * mm});
            skLineSegment(sketch, "E1314", {"start": v(-25.42, 50.76) * mm, "end": v(-24.43, 51.3) * mm});
            skLineSegment(sketch, "E1315", {"start": v(-24.43, 51.3) * mm, "end": v(-23.69, 52) * mm});
            skLineSegment(sketch, "E1316", {"start": v(-23.69, 52) * mm, "end": v(-23.18, 52.7) * mm});
            skLineSegment(sketch, "E1317", {"start": v(-23.18, 52.7) * mm, "end": v(-22.85, 53.35) * mm});
            skLineSegment(sketch, "E1318", {"start": v(-22.85, 53.35) * mm, "end": v(-22.68, 53.8) * mm});
            skLineSegment(sketch, "E1319", {"start": v(-22.68, 53.8) * mm, "end": v(-22.63, 53.99) * mm});
            skLineSegment(sketch, "E1320", {"start": v(-22.63, 53.99) * mm, "end": v(-22.69, 54.07) * mm});
            skLineSegment(sketch, "E1321", {"start": v(-22.69, 54.07) * mm, "end": v(-22.86, 54.27) * mm});
            skLineSegment(sketch, "E1322", {"start": v(-22.86, 54.27) * mm, "end": v(-23.15, 54.55) * mm});
            skLineSegment(sketch, "E1323", {"start": v(-23.15, 54.55) * mm, "end": v(-23.55, 54.86) * mm});
            skLineSegment(sketch, "E1324", {"start": v(-23.55, 54.86) * mm, "end": v(-24.08, 55.14) * mm});
            skLineSegment(sketch, "E1325", {"start": v(-24.08, 55.14) * mm, "end": v(-24.74, 55.35) * mm});
            skLineSegment(sketch, "E1326", {"start": v(-24.74, 55.35) * mm, "end": v(-25.53, 55.43) * mm});
            skLineSegment(sketch, "E1327", {"start": v(-25.53, 55.43) * mm, "end": v(-26.46, 55.34) * mm});
            skLineSegment(sketch, "E1328", {"start": v(-26.46, 55.34) * mm, "end": v(-26.48, 55.31) * mm});
            skLineSegment(sketch, "E1329", {"start": v(-26.48, 55.31) * mm, "end": v(-26.53, 55.25) * mm});
            skLineSegment(sketch, "E1330", {"start": v(-26.53, 55.25) * mm, "end": v(-26.58, 55.15) * mm});
            skLineSegment(sketch, "E1331", {"start": v(-26.58, 55.15) * mm, "end": v(-26.61, 55.03) * mm});
            skLineSegment(sketch, "E1332", {"start": v(-26.61, 55.03) * mm, "end": v(-26.59, 54.91) * mm});
            skLineSegment(sketch, "E1333", {"start": v(-26.59, 54.91) * mm, "end": v(-26.48, 54.8) * mm});
            skLineSegment(sketch, "E1334", {"start": v(-26.48, 54.8) * mm, "end": v(-26.27, 54.7) * mm});
            skLineSegment(sketch, "E1335", {"start": v(-26.27, 54.7) * mm, "end": v(-25.93, 54.61) * mm});
            skLineSegment(sketch, "E1336", {"start": v(-25.93, 54.61) * mm, "end": v(-25.62, 54.5) * mm});
            skLineSegment(sketch, "E1337", {"start": v(-25.62, 54.5) * mm, "end": v(-25.5, 54.32) * mm});
            skLineSegment(sketch, "E1338", {"start": v(-25.5, 54.32) * mm, "end": v(-25.56, 54.09) * mm});
            skLineSegment(sketch, "E1339", {"start": v(-25.56, 54.09) * mm, "end": v(-25.76, 53.84) * mm});
            skLineSegment(sketch, "E1340", {"start": v(-25.76, 53.84) * mm, "end": v(-26.09, 53.6) * mm});
            skLineSegment(sketch, "E1341", {"start": v(-26.09, 53.6) * mm, "end": v(-26.5, 53.42) * mm});
            skLineSegment(sketch, "E1342", {"start": v(-26.5, 53.42) * mm, "end": v(-27, 53.31) * mm});
            skLineSegment(sketch, "E1343", {"start": v(-27, 53.31) * mm, "end": v(-27.53, 53.31) * mm});
            skLineSegment(sketch, "E1344", {"start": v(-27.53, 53.31) * mm, "end": v(-28, 53.43) * mm});
            skLineSegment(sketch, "E1345", {"start": v(-28, 53.43) * mm, "end": v(-28.45, 53.66) * mm});
            skLineSegment(sketch, "E1346", {"start": v(-28.45, 53.66) * mm, "end": v(-28.83, 53.99) * mm});
            skLineSegment(sketch, "E1347", {"start": v(-28.83, 53.99) * mm, "end": v(-29.12, 54.41) * mm});
            skLineSegment(sketch, "E1348", {"start": v(-29.12, 54.41) * mm, "end": v(-29.28, 54.92) * mm});
            skLineSegment(sketch, "E1349", {"start": v(-29.28, 54.92) * mm, "end": v(-29.3, 55.51) * mm});
            skLineSegment(sketch, "E1350", {"start": v(-29.3, 55.51) * mm, "end": v(-29.13, 56.16) * mm});
            skLineSegment(sketch, "E1351", {"start": v(-29.13, 56.16) * mm, "end": v(-28.76, 56.87) * mm});
            skLineSegment(sketch, "E1352", {"start": v(37.33, 56.2) * mm, "end": v(37.19, 56.47) * mm});
            skLineSegment(sketch, "E1353", {"start": v(37.19, 56.47) * mm, "end": v(36.68, 56.81) * mm});
            skLineSegment(sketch, "E1354", {"start": v(36.68, 56.81) * mm, "end": v(35.84, 57.2) * mm});
            skLineSegment(sketch, "E1355", {"start": v(35.84, 57.2) * mm, "end": v(34.7, 57.57) * mm});
            skLineSegment(sketch, "E1356", {"start": v(34.7, 57.57) * mm, "end": v(33.32, 57.89) * mm});
            skLineSegment(sketch, "E1357", {"start": v(33.32, 57.89) * mm, "end": v(31.7, 58.1) * mm});
            skLineSegment(sketch, "E1358", {"start": v(31.7, 58.1) * mm, "end": v(29.91, 58.17) * mm});
            skLineSegment(sketch, "E1359", {"start": v(29.91, 58.17) * mm, "end": v(27.97, 58.05) * mm});
            skLineSegment(sketch, "E1360", {"start": v(27.97, 58.05) * mm, "end": v(26.24, 57.71) * mm});
            skLineSegment(sketch, "E1361", {"start": v(26.24, 57.71) * mm, "end": v(24.65, 57.17) * mm});
            skLineSegment(sketch, "E1362", {"start": v(24.65, 57.17) * mm, "end": v(23.19, 56.48) * mm});
            skLineSegment(sketch, "E1363", {"start": v(23.19, 56.48) * mm, "end": v(21.85, 55.7) * mm});
            skLineSegment(sketch, "E1364", {"start": v(21.85, 55.7) * mm, "end": v(20.63, 54.88) * mm});
            skLineSegment(sketch, "E1365", {"start": v(20.63, 54.88) * mm, "end": v(19.5, 54.08) * mm});
            skLineSegment(sketch, "E1366", {"start": v(19.5, 54.08) * mm, "end": v(18.48, 53.37) * mm});
            skLineSegment(sketch, "E1367", {"start": v(18.48, 53.37) * mm, "end": v(17.53, 52.8) * mm});
            skLineSegment(sketch, "E1368", {"start": v(17.53, 52.8) * mm, "end": v(16.67, 52.39) * mm});
            skLineSegment(sketch, "E1369", {"start": v(16.67, 52.39) * mm, "end": v(15.7, 52) * mm});
            skLineSegment(sketch, "E1370", {"start": v(15.7, 52) * mm, "end": v(14.64, 51.67) * mm});
            skLineSegment(sketch, "E1371", {"start": v(14.64, 51.67) * mm, "end": v(13.55, 51.4) * mm});
            skLineSegment(sketch, "E1372", {"start": v(13.55, 51.4) * mm, "end": v(12.47, 51.2) * mm});
            skLineSegment(sketch, "E1373", {"start": v(12.47, 51.2) * mm, "end": v(11.44, 51.11) * mm});
            skLineSegment(sketch, "E1374", {"start": v(11.44, 51.11) * mm, "end": v(10.5, 51.13) * mm});
            skLineSegment(sketch, "E1375", {"start": v(10.5, 51.13) * mm, "end": v(9.69, 51.28) * mm});
            skLineSegment(sketch, "E1376", {"start": v(9.69, 51.28) * mm, "end": v(9.05, 51.39) * mm});
            skLineSegment(sketch, "E1377", {"start": v(9.05, 51.39) * mm, "end": v(8.58, 51.29) * mm});
            skLineSegment(sketch, "E1378", {"start": v(8.58, 51.29) * mm, "end": v(8.27, 51.04) * mm});
            skLineSegment(sketch, "E1379", {"start": v(8.27, 51.04) * mm, "end": v(8.1, 50.7) * mm});
            skLineSegment(sketch, "E1380", {"start": v(8.1, 50.7) * mm, "end": v(8.04, 50.3) * mm});
            skLineSegment(sketch, "E1381", {"start": v(8.04, 50.3) * mm, "end": v(8.09, 49.9) * mm});
            skLineSegment(sketch, "E1382", {"start": v(8.09, 49.9) * mm, "end": v(8.22, 49.56) * mm});
            skLineSegment(sketch, "E1383", {"start": v(8.22, 49.56) * mm, "end": v(8.41, 49.33) * mm});
            skLineSegment(sketch, "E1384", {"start": v(8.41, 49.33) * mm, "end": v(8.63, 49.2) * mm});
            skLineSegment(sketch, "E1385", {"start": v(8.63, 49.2) * mm, "end": v(8.85, 49.1) * mm});
            skLineSegment(sketch, "E1386", {"start": v(8.85, 49.1) * mm, "end": v(9.1, 49.04) * mm});
            skLineSegment(sketch, "E1387", {"start": v(9.1, 49.04) * mm, "end": v(9.43, 49.04) * mm});
            skLineSegment(sketch, "E1388", {"start": v(9.43, 49.04) * mm, "end": v(9.85, 49.1) * mm});
            skLineSegment(sketch, "E1389", {"start": v(9.85, 49.1) * mm, "end": v(10.4, 49.24) * mm});
            skLineSegment(sketch, "E1390", {"start": v(10.4, 49.24) * mm, "end": v(11.1, 49.45) * mm});
            skLineSegment(sketch, "E1391", {"start": v(11.1, 49.45) * mm, "end": v(11.97, 49.76) * mm});
            skLineSegment(sketch, "E1392", {"start": v(11.97, 49.76) * mm, "end": v(12.4, 49.9) * mm});
            skLineSegment(sketch, "E1393", {"start": v(12.4, 49.9) * mm, "end": v(12.88, 50.02) * mm});
            skLineSegment(sketch, "E1394", {"start": v(12.88, 50.02) * mm, "end": v(13.38, 50.13) * mm});
            skLineSegment(sketch, "E1395", {"start": v(13.38, 50.13) * mm, "end": v(13.9, 50.23) * mm});
            skLineSegment(sketch, "E1396", {"start": v(13.9, 50.23) * mm, "end": v(14.44, 50.32) * mm});
            skLineSegment(sketch, "E1397", {"start": v(14.44, 50.32) * mm, "end": v(14.98, 50.4) * mm});
            skLineSegment(sketch, "E1398", {"start": v(14.98, 50.4) * mm, "end": v(15.54, 50.48) * mm});
            skLineSegment(sketch, "E1399", {"start": v(15.54, 50.48) * mm, "end": v(16.1, 50.55) * mm});
            skLineSegment(sketch, "E1400", {"start": v(16.1, 50.55) * mm, "end": v(17.62, 50.65) * mm});
            skLineSegment(sketch, "E1401", {"start": v(17.62, 50.65) * mm, "end": v(19.13, 50.6) * mm});
            skLineSegment(sketch, "E1402", {"start": v(19.13, 50.6) * mm, "end": v(20.6, 50.45) * mm});
            skLineSegment(sketch, "E1403", {"start": v(20.6, 50.45) * mm, "end": v(22.04, 50.24) * mm});
            skLineSegment(sketch, "E1404", {"start": v(22.04, 50.24) * mm, "end": v(23.4, 50.02) * mm});
            skLineSegment(sketch, "E1405", {"start": v(23.4, 50.02) * mm, "end": v(24.7, 49.82) * mm});
            skLineSegment(sketch, "E1406", {"start": v(24.7, 49.82) * mm, "end": v(25.88, 49.68) * mm});
            skLineSegment(sketch, "E1407", {"start": v(25.88, 49.68) * mm, "end": v(26.95, 49.66) * mm});
            skLineSegment(sketch, "E1408", {"start": v(26.95, 49.66) * mm, "end": v(28.9, 49.84) * mm});
            skLineSegment(sketch, "E1409", {"start": v(28.9, 49.84) * mm, "end": v(30.71, 50.2) * mm});
            skLineSegment(sketch, "E1410", {"start": v(30.71, 50.2) * mm, "end": v(32.34, 50.75) * mm});
            skLineSegment(sketch, "E1411", {"start": v(32.34, 50.75) * mm, "end": v(33.78, 51.47) * mm});
            skLineSegment(sketch, "E1412", {"start": v(33.78, 51.47) * mm, "end": v(35.02, 52.37) * mm});
            skLineSegment(sketch, "E1413", {"start": v(35.02, 52.37) * mm, "end": v(36.03, 53.46) * mm});
            skLineSegment(sketch, "E1414", {"start": v(36.03, 53.46) * mm, "end": v(36.8, 54.74) * mm});
            skLineSegment(sketch, "E1415", {"start": v(36.8, 54.74) * mm, "end": v(37.33, 56.2) * mm});
            skLineSegment(sketch, "E1416", {"start": v(28.16, 56.87) * mm, "end": v(28.27, 56.9) * mm});
            skLineSegment(sketch, "E1417", {"start": v(28.27, 56.9) * mm, "end": v(28.56, 56.96) * mm});
            skLineSegment(sketch, "E1418", {"start": v(28.56, 56.96) * mm, "end": v(29, 57.04) * mm});
            skLineSegment(sketch, "E1419", {"start": v(29, 57.04) * mm, "end": v(29.52, 57.12) * mm});
            skLineSegment(sketch, "E1420", {"start": v(29.52, 57.12) * mm, "end": v(30.1, 57.17) * mm});
            skLineSegment(sketch, "E1421", {"start": v(30.1, 57.17) * mm, "end": v(30.7, 57.17) * mm});
            skLineSegment(sketch, "E1422", {"start": v(30.7, 57.17) * mm, "end": v(31.27, 57.1) * mm});
            skLineSegment(sketch, "E1423", {"start": v(31.27, 57.1) * mm, "end": v(31.77, 56.95) * mm});
            skLineSegment(sketch, "E1424", {"start": v(31.77, 56.95) * mm, "end": v(31.8, 56.7) * mm});
            skLineSegment(sketch, "E1425", {"start": v(31.8, 56.7) * mm, "end": v(31.85, 56.05) * mm});
            skLineSegment(sketch, "E1426", {"start": v(31.85, 56.05) * mm, "end": v(31.83, 55.1) * mm});
            skLineSegment(sketch, "E1427", {"start": v(31.83, 55.1) * mm, "end": v(31.66, 54) * mm});
            skLineSegment(sketch, "E1428", {"start": v(31.66, 54) * mm, "end": v(31.24, 52.86) * mm});
            skLineSegment(sketch, "E1429", {"start": v(31.24, 52.86) * mm, "end": v(30.5, 51.82) * mm});
            skLineSegment(sketch, "E1430", {"start": v(30.5, 51.82) * mm, "end": v(29.36, 51) * mm});
            skLineSegment(sketch, "E1431", {"start": v(29.36, 51) * mm, "end": v(27.72, 50.5) * mm});
            skLineSegment(sketch, "E1432", {"start": v(27.72, 50.5) * mm, "end": v(26.11, 50.46) * mm});
            skLineSegment(sketch, "E1433", {"start": v(26.11, 50.46) * mm, "end": v(24.83, 50.76) * mm});
            skLineSegment(sketch, "E1434", {"start": v(24.83, 50.76) * mm, "end": v(23.83, 51.3) * mm});
            skLineSegment(sketch, "E1435", {"start": v(23.83, 51.3) * mm, "end": v(23.1, 52) * mm});
            skLineSegment(sketch, "E1436", {"start": v(23.1, 52) * mm, "end": v(22.58, 52.7) * mm});
            skLineSegment(sketch, "E1437", {"start": v(22.58, 52.7) * mm, "end": v(22.26, 53.35) * mm});
            skLineSegment(sketch, "E1438", {"start": v(22.26, 53.35) * mm, "end": v(22.09, 53.8) * mm});
            skLineSegment(sketch, "E1439", {"start": v(22.09, 53.8) * mm, "end": v(22.04, 53.99) * mm});
            skLineSegment(sketch, "E1440", {"start": v(22.04, 53.99) * mm, "end": v(22.1, 54.07) * mm});
            skLineSegment(sketch, "E1441", {"start": v(22.1, 54.07) * mm, "end": v(22.26, 54.27) * mm});
            skLineSegment(sketch, "E1442", {"start": v(22.26, 54.27) * mm, "end": v(22.55, 54.55) * mm});
            skLineSegment(sketch, "E1443", {"start": v(22.55, 54.55) * mm, "end": v(22.96, 54.86) * mm});
            skLineSegment(sketch, "E1444", {"start": v(22.96, 54.86) * mm, "end": v(23.49, 55.14) * mm});
            skLineSegment(sketch, "E1445", {"start": v(23.49, 55.14) * mm, "end": v(24.15, 55.35) * mm});
            skLineSegment(sketch, "E1446", {"start": v(24.15, 55.35) * mm, "end": v(24.94, 55.43) * mm});
            skLineSegment(sketch, "E1447", {"start": v(24.94, 55.43) * mm, "end": v(25.86, 55.34) * mm});
            skLineSegment(sketch, "E1448", {"start": v(25.86, 55.34) * mm, "end": v(25.88, 55.31) * mm});
            skLineSegment(sketch, "E1449", {"start": v(25.88, 55.31) * mm, "end": v(25.94, 55.25) * mm});
            skLineSegment(sketch, "E1450", {"start": v(25.94, 55.25) * mm, "end": v(25.99, 55.15) * mm});
            skLineSegment(sketch, "E1451", {"start": v(25.99, 55.15) * mm, "end": v(26.02, 55.03) * mm});
            skLineSegment(sketch, "E1452", {"start": v(26.02, 55.03) * mm, "end": v(26, 54.91) * mm});
            skLineSegment(sketch, "E1453", {"start": v(26, 54.91) * mm, "end": v(25.9, 54.8) * mm});
            skLineSegment(sketch, "E1454", {"start": v(25.9, 54.8) * mm, "end": v(25.68, 54.7) * mm});
            skLineSegment(sketch, "E1455", {"start": v(25.68, 54.7) * mm, "end": v(25.34, 54.61) * mm});
            skLineSegment(sketch, "E1456", {"start": v(25.34, 54.61) * mm, "end": v(25.03, 54.5) * mm});
            skLineSegment(sketch, "E1457", {"start": v(25.03, 54.5) * mm, "end": v(24.92, 54.32) * mm});
            skLineSegment(sketch, "E1458", {"start": v(24.92, 54.32) * mm, "end": v(24.97, 54.09) * mm});
            skLineSegment(sketch, "E1459", {"start": v(24.97, 54.09) * mm, "end": v(25.17, 53.84) * mm});
            skLineSegment(sketch, "E1460", {"start": v(25.17, 53.84) * mm, "end": v(25.5, 53.6) * mm});
            skLineSegment(sketch, "E1461", {"start": v(25.5, 53.6) * mm, "end": v(25.9, 53.42) * mm});
            skLineSegment(sketch, "E1462", {"start": v(25.9, 53.42) * mm, "end": v(26.4, 53.31) * mm});
            skLineSegment(sketch, "E1463", {"start": v(26.4, 53.31) * mm, "end": v(26.93, 53.31) * mm});
            skLineSegment(sketch, "E1464", {"start": v(26.93, 53.31) * mm, "end": v(27.4, 53.43) * mm});
            skLineSegment(sketch, "E1465", {"start": v(27.4, 53.43) * mm, "end": v(27.85, 53.66) * mm});
            skLineSegment(sketch, "E1466", {"start": v(27.85, 53.66) * mm, "end": v(28.23, 53.99) * mm});
            skLineSegment(sketch, "E1467", {"start": v(28.23, 53.99) * mm, "end": v(28.52, 54.41) * mm});
            skLineSegment(sketch, "E1468", {"start": v(28.52, 54.41) * mm, "end": v(28.7, 54.92) * mm});
            skLineSegment(sketch, "E1469", {"start": v(28.7, 54.92) * mm, "end": v(28.7, 55.51) * mm});
            skLineSegment(sketch, "E1470", {"start": v(28.7, 55.51) * mm, "end": v(28.54, 56.16) * mm});
            skLineSegment(sketch, "E1471", {"start": v(28.54, 56.16) * mm, "end": v(28.16, 56.87) * mm});
            skLineSegment(sketch, "E1472", {"start": v(-42.38, 58.22) * mm, "end": v(-43.9, 57.8) * mm});
            skLineSegment(sketch, "E1473", {"start": v(-43.9, 57.8) * mm, "end": v(-47.94, 56.41) * mm});
            skLineSegment(sketch, "E1474", {"start": v(-47.94, 56.41) * mm, "end": v(-53.69, 53.77) * mm});
            skLineSegment(sketch, "E1475", {"start": v(-53.69, 53.77) * mm, "end": v(-60.35, 49.62) * mm});
            skLineSegment(sketch, "E1476", {"start": v(-60.35, 49.62) * mm, "end": v(-67.15, 43.72) * mm});
            skLineSegment(sketch, "E1477", {"start": v(-67.15, 43.72) * mm, "end": v(-73.27, 35.81) * mm});
            skLineSegment(sketch, "E1478", {"start": v(-73.27, 35.81) * mm, "end": v(-77.92, 25.64) * mm});
            skLineSegment(sketch, "E1479", {"start": v(-77.92, 25.64) * mm, "end": v(-80.3, 12.94) * mm});
            skLineSegment(sketch, "E1480", {"start": v(-80.3, 12.94) * mm, "end": v(-79.98, 13.27) * mm});
            skLineSegment(sketch, "E1481", {"start": v(-79.98, 13.27) * mm, "end": v(-79.06, 14.14) * mm});
            skLineSegment(sketch, "E1482", {"start": v(-79.06, 14.14) * mm, "end": v(-77.66, 15.4) * mm});
            skLineSegment(sketch, "E1483", {"start": v(-77.66, 15.4) * mm, "end": v(-75.86, 16.9) * mm});
            skLineSegment(sketch, "E1484", {"start": v(-75.86, 16.9) * mm, "end": v(-73.77, 18.47) * mm});
            skLineSegment(sketch, "E1485", {"start": v(-73.77, 18.47) * mm, "end": v(-71.5, 19.96) * mm});
            skLineSegment(sketch, "E1486", {"start": v(-71.5, 19.96) * mm, "end": v(-69.11, 21.2) * mm});
            skLineSegment(sketch, "E1487", {"start": v(-69.11, 21.2) * mm, "end": v(-66.73, 22.03) * mm});
            skLineSegment(sketch, "E1488", {"start": v(-66.73, 22.03) * mm, "end": v(-67.13, 21.53) * mm});
            skLineSegment(sketch, "E1489", {"start": v(-67.13, 21.53) * mm, "end": v(-68.2, 20) * mm});
            skLineSegment(sketch, "E1490", {"start": v(-68.2, 20) * mm, "end": v(-69.7, 17.46) * mm});
            skLineSegment(sketch, "E1491", {"start": v(-69.7, 17.46) * mm, "end": v(-71.46, 13.9) * mm});
            skLineSegment(sketch, "E1492", {"start": v(-71.46, 13.9) * mm, "end": v(-73.23, 9.34) * mm});
            skLineSegment(sketch, "E1493", {"start": v(-73.23, 9.34) * mm, "end": v(-74.83, 3.75) * mm});
            skLineSegment(sketch, "E1494", {"start": v(-74.83, 3.75) * mm, "end": v(-76.04, -2.85) * mm});
            skLineSegment(sketch, "E1495", {"start": v(-76.04, -2.85) * mm, "end": v(-76.64, -10.46) * mm});
            skLineSegment(sketch, "E1496", {"start": v(-76.64, -10.46) * mm, "end": v(-75.95, -9.8) * mm});
            skLineSegment(sketch, "E1497", {"start": v(-75.95, -9.8) * mm, "end": v(-74.05, -8.04) * mm});
            skLineSegment(sketch, "E1498", {"start": v(-74.05, -8.04) * mm, "end": v(-71.2, -5.53) * mm});
            skLineSegment(sketch, "E1499", {"start": v(-71.2, -5.53) * mm, "end": v(-67.7, -2.61) * mm});
            skLineSegment(sketch, "E1500", {"start": v(-67.7, -2.61) * mm, "end": v(-63.78, 0.36) * mm});
            skLineSegment(sketch, "E1501", {"start": v(-63.78, 0.36) * mm, "end": v(-59.73, 3.04) * mm});
            skLineSegment(sketch, "E1502", {"start": v(-59.73, 3.04) * mm, "end": v(-55.8, 5.08) * mm});
            skLineSegment(sketch, "E1503", {"start": v(-55.8, 5.08) * mm, "end": v(-52.29, 6.13) * mm});
            skLineSegment(sketch, "E1504", {"start": v(-52.29, 6.13) * mm, "end": v(-52.68, 5.6) * mm});
            skLineSegment(sketch, "E1505", {"start": v(-52.68, 5.6) * mm, "end": v(-53.7, 4.06) * mm});
            skLineSegment(sketch, "E1506", {"start": v(-53.7, 4.06) * mm, "end": v(-55.16, 1.55) * mm});
            skLineSegment(sketch, "E1507", {"start": v(-55.16, 1.55) * mm, "end": v(-56.83, -1.9) * mm});
            skLineSegment(sketch, "E1508", {"start": v(-56.83, -1.9) * mm, "end": v(-58.5, -6.21) * mm});
            skLineSegment(sketch, "E1509", {"start": v(-58.5, -6.21) * mm, "end": v(-59.95, -11.37) * mm});
            skLineSegment(sketch, "E1510", {"start": v(-59.95, -11.37) * mm, "end": v(-60.98, -17.32) * mm});
            skLineSegment(sketch, "E1511", {"start": v(-60.98, -17.32) * mm, "end": v(-61.37, -24) * mm});
            skLineSegment(sketch, "E1512", {"start": v(-61.37, -24) * mm, "end": v(-60.81, -23.48) * mm});
            skLineSegment(sketch, "E1513", {"start": v(-60.81, -23.48) * mm, "end": v(-59.23, -22.1) * mm});
            skLineSegment(sketch, "E1514", {"start": v(-59.23, -22.1) * mm, "end": v(-56.71, -20.15) * mm});
            skLineSegment(sketch, "E1515", {"start": v(-56.71, -20.15) * mm, "end": v(-53.38, -17.9) * mm});
            skLineSegment(sketch, "E1516", {"start": v(-53.38, -17.9) * mm, "end": v(-49.34, -15.67) * mm});
            skLineSegment(sketch, "E1517", {"start": v(-49.34, -15.67) * mm, "end": v(-44.69, -13.72) * mm});
            skLineSegment(sketch, "E1518", {"start": v(-44.69, -13.72) * mm, "end": v(-39.54, -12.34) * mm});
            skLineSegment(sketch, "E1519", {"start": v(-39.54, -12.34) * mm, "end": v(-34, -11.81) * mm});
            skLineSegment(sketch, "E1520", {"start": v(-34, -11.81) * mm, "end": v(-34.26, -11.44) * mm});
            skLineSegment(sketch, "E1521", {"start": v(-34.26, -11.44) * mm, "end": v(-34.91, -10.37) * mm});
            skLineSegment(sketch, "E1522", {"start": v(-34.91, -10.37) * mm, "end": v(-35.83, -8.63) * mm});
            skLineSegment(sketch, "E1523", {"start": v(-35.83, -8.63) * mm, "end": v(-36.88, -6.27) * mm});
            skLineSegment(sketch, "E1524", {"start": v(-36.88, -6.27) * mm, "end": v(-37.92, -3.34) * mm});
            skLineSegment(sketch, "E1525", {"start": v(-37.92, -3.34) * mm, "end": v(-38.8, 0.11) * mm});
            skLineSegment(sketch, "E1526", {"start": v(-38.8, 0.11) * mm, "end": v(-39.4, 4.05) * mm});
            skLineSegment(sketch, "E1527", {"start": v(-39.4, 4.05) * mm, "end": v(-39.58, 8.42) * mm});
            skLineSegment(sketch, "E1528", {"start": v(-39.58, 8.42) * mm, "end": v(-39.74, 8.01) * mm});
            skLineSegment(sketch, "E1529", {"start": v(-39.74, 8.01) * mm, "end": v(-40.13, 6.89) * mm});
            skLineSegment(sketch, "E1530", {"start": v(-40.13, 6.89) * mm, "end": v(-40.68, 5.2) * mm});
            skLineSegment(sketch, "E1531", {"start": v(-40.68, 5.2) * mm, "end": v(-41.28, 3.1) * mm});
            skLineSegment(sketch, "E1532", {"start": v(-41.28, 3.1) * mm, "end": v(-41.84, 0.73) * mm});
            skLineSegment(sketch, "E1533", {"start": v(-41.84, 0.73) * mm, "end": v(-42.28, -1.76) * mm});
            skLineSegment(sketch, "E1534", {"start": v(-42.28, -1.76) * mm, "end": v(-42.49, -4.2) * mm});
            skLineSegment(sketch, "E1535", {"start": v(-42.49, -4.2) * mm, "end": v(-42.38, -6.45) * mm});
            skLineSegment(sketch, "E1536", {"start": v(-42.38, -6.45) * mm, "end": v(-42.87, -6.68) * mm});
            skLineSegment(sketch, "E1537", {"start": v(-42.87, -6.68) * mm, "end": v(-44.19, -7.33) * mm});
            skLineSegment(sketch, "E1538", {"start": v(-44.19, -7.33) * mm, "end": v(-46.1, -8.3) * mm});
            skLineSegment(sketch, "E1539", {"start": v(-46.1, -8.3) * mm, "end": v(-48.39, -9.55) * mm});
            skLineSegment(sketch, "E1540", {"start": v(-48.39, -9.55) * mm, "end": v(-50.8, -10.97) * mm});
            skLineSegment(sketch, "E1541", {"start": v(-50.8, -10.97) * mm, "end": v(-53.14, -12.5) * mm});
            skLineSegment(sketch, "E1542", {"start": v(-53.14, -12.5) * mm, "end": v(-55.15, -14.04) * mm});
            skLineSegment(sketch, "E1543", {"start": v(-55.15, -14.04) * mm, "end": v(-56.62, -15.54) * mm});
            skLineSegment(sketch, "E1544", {"start": v(-56.62, -15.54) * mm, "end": v(-56.5, -14.82) * mm});
            skLineSegment(sketch, "E1545", {"start": v(-56.5, -14.82) * mm, "end": v(-56.14, -12.85) * mm});
            skLineSegment(sketch, "E1546", {"start": v(-56.14, -12.85) * mm, "end": v(-55.5, -9.94) * mm});
            skLineSegment(sketch, "E1547", {"start": v(-55.5, -9.94) * mm, "end": v(-54.57, -6.39) * mm});
            skLineSegment(sketch, "E1548", {"start": v(-54.57, -6.39) * mm, "end": v(-53.32, -2.5) * mm});
            skLineSegment(sketch, "E1549", {"start": v(-53.32, -2.5) * mm, "end": v(-51.72, 1.41) * mm});
            skLineSegment(sketch, "E1550", {"start": v(-51.72, 1.41) * mm, "end": v(-49.76, 5.06) * mm});
            skLineSegment(sketch, "E1551", {"start": v(-49.76, 5.06) * mm, "end": v(-47.4, 8.13) * mm});
            skLineSegment(sketch, "E1552", {"start": v(-47.4, 8.13) * mm, "end": v(-47.95, 8.25) * mm});
            skLineSegment(sketch, "E1553", {"start": v(-47.95, 8.25) * mm, "end": v(-49.51, 8.47) * mm});
            skLineSegment(sketch, "E1554", {"start": v(-49.51, 8.47) * mm, "end": v(-51.96, 8.53) * mm});
            skLineSegment(sketch, "E1555", {"start": v(-51.96, 8.53) * mm, "end": v(-55.17, 8.18) * mm});
            skLineSegment(sketch, "E1556", {"start": v(-55.17, 8.18) * mm, "end": v(-59, 7.17) * mm});
            skLineSegment(sketch, "E1557", {"start": v(-59, 7.17) * mm, "end": v(-63.34, 5.26) * mm});
            skLineSegment(sketch, "E1558", {"start": v(-63.34, 5.26) * mm, "end": v(-68.04, 2.2) * mm});
            skLineSegment(sketch, "E1559", {"start": v(-68.04, 2.2) * mm, "end": v(-72.98, -2.27) * mm});
            skLineSegment(sketch, "E1560", {"start": v(-72.98, -2.27) * mm, "end": v(-72.8, -1.39) * mm});
            skLineSegment(sketch, "E1561", {"start": v(-72.8, -1.39) * mm, "end": v(-72.22, 1.01) * mm});
            skLineSegment(sketch, "E1562", {"start": v(-72.22, 1.01) * mm, "end": v(-71.28, 4.55) * mm});
            skLineSegment(sketch, "E1563", {"start": v(-71.28, 4.55) * mm, "end": v(-69.97, 8.84) * mm});
            skLineSegment(sketch, "E1564", {"start": v(-69.97, 8.84) * mm, "end": v(-68.3, 13.5) * mm});
            skLineSegment(sketch, "E1565", {"start": v(-68.3, 13.5) * mm, "end": v(-66.27, 18.16) * mm});
            skLineSegment(sketch, "E1566", {"start": v(-66.27, 18.16) * mm, "end": v(-63.89, 22.44) * mm});
            skLineSegment(sketch, "E1567", {"start": v(-63.89, 22.44) * mm, "end": v(-61.16, 25.95) * mm});
            skLineSegment(sketch, "E1568", {"start": v(-61.16, 25.95) * mm, "end": v(-61.46, 25.91) * mm});
            skLineSegment(sketch, "E1569", {"start": v(-61.46, 25.91) * mm, "end": v(-62.33, 25.78) * mm});
            skLineSegment(sketch, "E1570", {"start": v(-62.33, 25.78) * mm, "end": v(-63.7, 25.5) * mm});
            skLineSegment(sketch, "E1571", {"start": v(-63.7, 25.5) * mm, "end": v(-65.47, 25.03) * mm});
            skLineSegment(sketch, "E1572", {"start": v(-65.47, 25.03) * mm, "end": v(-67.6, 24.32) * mm});
            skLineSegment(sketch, "E1573", {"start": v(-67.6, 24.32) * mm, "end": v(-70, 23.33) * mm});
            skLineSegment(sketch, "E1574", {"start": v(-70, 23.33) * mm, "end": v(-72.62, 22.01) * mm});
            skLineSegment(sketch, "E1575", {"start": v(-72.62, 22.01) * mm, "end": v(-75.36, 20.32) * mm});
            skLineSegment(sketch, "E1576", {"start": v(-75.36, 20.32) * mm, "end": v(-75.07, 21.49) * mm});
            skLineSegment(sketch, "E1577", {"start": v(-75.07, 21.49) * mm, "end": v(-74.06, 24.67) * mm});
            skLineSegment(sketch, "E1578", {"start": v(-74.06, 24.67) * mm, "end": v(-72.15, 29.36) * mm});
            skLineSegment(sketch, "E1579", {"start": v(-72.15, 29.36) * mm, "end": v(-69.15, 35.07) * mm});
            skLineSegment(sketch, "E1580", {"start": v(-69.15, 35.07) * mm, "end": v(-64.87, 41.31) * mm});
            skLineSegment(sketch, "E1581", {"start": v(-64.87, 41.31) * mm, "end": v(-59.1, 47.58) * mm});
            skLineSegment(sketch, "E1582", {"start": v(-59.1, 47.58) * mm, "end": v(-51.67, 53.38) * mm});
            skLineSegment(sketch, "E1583", {"start": v(-51.67, 53.38) * mm, "end": v(-42.38, 58.22) * mm});
            skLineSegment(sketch, "E1584", {"start": v(-34, 71.13) * mm, "end": v(-35.45, 71.55) * mm});
            skLineSegment(sketch, "E1585", {"start": v(-35.45, 71.55) * mm, "end": v(-37.02, 71.87) * mm});
            skLineSegment(sketch, "E1586", {"start": v(-37.02, 71.87) * mm, "end": v(-38.7, 72.09) * mm});
            skLineSegment(sketch, "E1587", {"start": v(-38.7, 72.09) * mm, "end": v(-40.46, 72.24) * mm});
            skLineSegment(sketch, "E1588", {"start": v(-40.46, 72.24) * mm, "end": v(-42.3, 72.34) * mm});
            skLineSegment(sketch, "E1589", {"start": v(-42.3, 72.34) * mm, "end": v(-44.17, 72.4) * mm});
            skLineSegment(sketch, "E1590", {"start": v(-44.17, 72.4) * mm, "end": v(-46.08, 72.47) * mm});
            skLineSegment(sketch, "E1591", {"start": v(-46.08, 72.47) * mm, "end": v(-48, 72.55) * mm});
            skLineSegment(sketch, "E1592", {"start": v(-48, 72.55) * mm, "end": v(-49.25, 72.7) * mm});
            skLineSegment(sketch, "E1593", {"start": v(-49.25, 72.7) * mm, "end": v(-50.61, 73.01) * mm});
            skLineSegment(sketch, "E1594", {"start": v(-50.61, 73.01) * mm, "end": v(-52.06, 73.37) * mm});
            skLineSegment(sketch, "E1595", {"start": v(-52.06, 73.37) * mm, "end": v(-53.6, 73.69) * mm});
            skLineSegment(sketch, "E1596", {"start": v(-53.6, 73.69) * mm, "end": v(-55.2, 73.88) * mm});
            skLineSegment(sketch, "E1597", {"start": v(-55.2, 73.88) * mm, "end": v(-56.84, 73.85) * mm});
            skLineSegment(sketch, "E1598", {"start": v(-56.84, 73.85) * mm, "end": v(-58.52, 73.5) * mm});
            skLineSegment(sketch, "E1599", {"start": v(-58.52, 73.5) * mm, "end": v(-60.23, 72.75) * mm});
            skLineSegment(sketch, "E1600", {"start": v(-60.23, 72.75) * mm, "end": v(-61.77, 70.92) * mm});
            skLineSegment(sketch, "E1601", {"start": v(-61.77, 70.92) * mm, "end": v(-61.57, 68.55) * mm});
            skLineSegment(sketch, "E1602", {"start": v(-61.57, 68.55) * mm, "end": v(-60.1, 65.89) * mm});
            skLineSegment(sketch, "E1603", {"start": v(-60.1, 65.89) * mm, "end": v(-57.83, 63.16) * mm});
            skLineSegment(sketch, "E1604", {"start": v(-57.83, 63.16) * mm, "end": v(-55.24, 60.63) * mm});
            skLineSegment(sketch, "E1605", {"start": v(-55.24, 60.63) * mm, "end": v(-52.8, 58.52) * mm});
            skLineSegment(sketch, "E1606", {"start": v(-52.8, 58.52) * mm, "end": v(-50.99, 57.07) * mm});
            skLineSegment(sketch, "E1607", {"start": v(-50.99, 57.07) * mm, "end": v(-50.28, 56.54) * mm});
            skLineSegment(sketch, "E1608", {"start": v(-50.28, 56.54) * mm, "end": v(-49.87, 56.91) * mm});
            skLineSegment(sketch, "E1609", {"start": v(-49.87, 56.91) * mm, "end": v(-48.7, 57.9) * mm});
            skLineSegment(sketch, "E1610", {"start": v(-48.7, 57.9) * mm, "end": v(-46.89, 59.28) * mm});
            skLineSegment(sketch, "E1611", {"start": v(-46.89, 59.28) * mm, "end": v(-44.55, 60.87) * mm});
            skLineSegment(sketch, "E1612", {"start": v(-44.55, 60.87) * mm, "end": v(-41.81, 62.45) * mm});
            skLineSegment(sketch, "E1613", {"start": v(-41.81, 62.45) * mm, "end": v(-38.77, 63.82) * mm});
            skLineSegment(sketch, "E1614", {"start": v(-38.77, 63.82) * mm, "end": v(-35.56, 64.78) * mm});
            skLineSegment(sketch, "E1615", {"start": v(-35.56, 64.78) * mm, "end": v(-32.28, 65.13) * mm});
            skLineSegment(sketch, "E1616", {"start": v(-32.28, 65.13) * mm, "end": v(-28.5, 64.97) * mm});
            skLineSegment(sketch, "E1617", {"start": v(-28.5, 64.97) * mm, "end": v(-25.47, 64.63) * mm});
            skLineSegment(sketch, "E1618", {"start": v(-25.47, 64.63) * mm, "end": v(-23.08, 64.17) * mm});
            skLineSegment(sketch, "E1619", {"start": v(-23.08, 64.17) * mm, "end": v(-21.28, 63.66) * mm});
            skLineSegment(sketch, "E1620", {"start": v(-21.28, 63.66) * mm, "end": v(-20, 63.15) * mm});
            skLineSegment(sketch, "E1621", {"start": v(-20, 63.15) * mm, "end": v(-19.18, 62.7) * mm});
            skLineSegment(sketch, "E1622", {"start": v(-19.18, 62.7) * mm, "end": v(-18.73, 62.4) * mm});
            skLineSegment(sketch, "E1623", {"start": v(-18.73, 62.4) * mm, "end": v(-18.6, 62.28) * mm});
            skLineSegment(sketch, "E1624", {"start": v(-18.6, 62.28) * mm, "end": v(-18.86, 62.6) * mm});
            skLineSegment(sketch, "E1625", {"start": v(-18.86, 62.6) * mm, "end": v(-19.63, 63.42) * mm});
            skLineSegment(sketch, "E1626", {"start": v(-19.63, 63.42) * mm, "end": v(-20.93, 64.54) * mm});
            skLineSegment(sketch, "E1627", {"start": v(-20.93, 64.54) * mm, "end": v(-22.78, 65.75) * mm});
            skLineSegment(sketch, "E1628", {"start": v(-22.78, 65.75) * mm, "end": v(-25.18, 66.85) * mm});
            skLineSegment(sketch, "E1629", {"start": v(-25.18, 66.85) * mm, "end": v(-28.15, 67.62) * mm});
            skLineSegment(sketch, "E1630", {"start": v(-28.15, 67.62) * mm, "end": v(-31.7, 67.86) * mm});
            skLineSegment(sketch, "E1631", {"start": v(-31.7, 67.86) * mm, "end": v(-35.83, 67.36) * mm});
            skLineSegment(sketch, "E1632", {"start": v(-35.83, 67.36) * mm, "end": v(-38.08, 66.85) * mm});
            skLineSegment(sketch, "E1633", {"start": v(-38.08, 66.85) * mm, "end": v(-40.04, 66.35) * mm});
            skLineSegment(sketch, "E1634", {"start": v(-40.04, 66.35) * mm, "end": v(-41.78, 65.9) * mm});
            skLineSegment(sketch, "E1635", {"start": v(-41.78, 65.9) * mm, "end": v(-43.38, 65.52) * mm});
            skLineSegment(sketch, "E1636", {"start": v(-43.38, 65.52) * mm, "end": v(-44.9, 65.27) * mm});
            skLineSegment(sketch, "E1637", {"start": v(-44.9, 65.27) * mm, "end": v(-46.44, 65.17) * mm});
            skLineSegment(sketch, "E1638", {"start": v(-46.44, 65.17) * mm, "end": v(-48.04, 65.25) * mm});
            skLineSegment(sketch, "E1639", {"start": v(-48.04, 65.25) * mm, "end": v(-49.79, 65.56) * mm});
            skLineSegment(sketch, "E1640", {"start": v(-49.79, 65.56) * mm, "end": v(-51.63, 66.1) * mm});
            skLineSegment(sketch, "E1641", {"start": v(-51.63, 66.1) * mm, "end": v(-53.4, 66.85) * mm});
            skLineSegment(sketch, "E1642", {"start": v(-53.4, 66.85) * mm, "end": v(-55.04, 67.72) * mm});
            skLineSegment(sketch, "E1643", {"start": v(-55.04, 67.72) * mm, "end": v(-56.45, 68.63) * mm});
            skLineSegment(sketch, "E1644", {"start": v(-56.45, 68.63) * mm, "end": v(-57.56, 69.54) * mm});
            skLineSegment(sketch, "E1645", {"start": v(-57.56, 69.54) * mm, "end": v(-58.3, 70.36) * mm});
            skLineSegment(sketch, "E1646", {"start": v(-58.3, 70.36) * mm, "end": v(-58.57, 71.02) * mm});
            skLineSegment(sketch, "E1647", {"start": v(-58.57, 71.02) * mm, "end": v(-58.32, 71.46) * mm});
            skLineSegment(sketch, "E1648", {"start": v(-58.32, 71.46) * mm, "end": v(-57.7, 71.73) * mm});
            skLineSegment(sketch, "E1649", {"start": v(-57.7, 71.73) * mm, "end": v(-56.98, 71.92) * mm});
            skLineSegment(sketch, "E1650", {"start": v(-56.98, 71.92) * mm, "end": v(-56.1, 72.02) * mm});
            skLineSegment(sketch, "E1651", {"start": v(-56.1, 72.02) * mm, "end": v(-55.08, 72.04) * mm});
            skLineSegment(sketch, "E1652", {"start": v(-55.08, 72.04) * mm, "end": v(-53.9, 71.98) * mm});
            skLineSegment(sketch, "E1653", {"start": v(-53.9, 71.98) * mm, "end": v(-52.51, 71.84) * mm});
            skLineSegment(sketch, "E1654", {"start": v(-52.51, 71.84) * mm, "end": v(-50.93, 71.6) * mm});
            skLineSegment(sketch, "E1655", {"start": v(-50.93, 71.6) * mm, "end": v(-49.13, 71.3) * mm});
            skLineSegment(sketch, "E1656", {"start": v(-49.13, 71.3) * mm, "end": v(-47.46, 71.1) * mm});
            skLineSegment(sketch, "E1657", {"start": v(-47.46, 71.1) * mm, "end": v(-45.27, 71) * mm});
            skLineSegment(sketch, "E1658", {"start": v(-45.27, 71) * mm, "end": v(-42.78, 70.96) * mm});
            skLineSegment(sketch, "E1659", {"start": v(-42.78, 70.96) * mm, "end": v(-40.24, 70.97) * mm});
            skLineSegment(sketch, "E1660", {"start": v(-40.24, 70.97) * mm, "end": v(-37.86, 71) * mm});
            skLineSegment(sketch, "E1661", {"start": v(-37.86, 71) * mm, "end": v(-35.87, 71.06) * mm});
            skLineSegment(sketch, "E1662", {"start": v(-35.87, 71.06) * mm, "end": v(-34.51, 71.1) * mm});
            skLineSegment(sketch, "E1663", {"start": v(-34.51, 71.1) * mm, "end": v(-34, 71.13) * mm});
            skLineSegment(sketch, "E1664", {"start": v(-0.3, 72.61) * mm, "end": v(6.32, 73.37) * mm});
            skLineSegment(sketch, "E1665", {"start": v(6.32, 73.37) * mm, "end": v(12.58, 73.47) * mm});
            skLineSegment(sketch, "E1666", {"start": v(12.58, 73.47) * mm, "end": v(18.32, 73.09) * mm});
            skLineSegment(sketch, "E1667", {"start": v(18.32, 73.09) * mm, "end": v(23.38, 72.4) * mm});
            skLineSegment(sketch, "E1668", {"start": v(23.38, 72.4) * mm, "end": v(27.6, 71.56) * mm});
            skLineSegment(sketch, "E1669", {"start": v(27.6, 71.56) * mm, "end": v(30.82, 70.75) * mm});
            skLineSegment(sketch, "E1670", {"start": v(30.82, 70.75) * mm, "end": v(32.87, 70.14) * mm});
            skLineSegment(sketch, "E1671", {"start": v(32.87, 70.14) * mm, "end": v(33.59, 69.9) * mm});
            skLineSegment(sketch, "E1672", {"start": v(33.59, 69.9) * mm, "end": v(32.92, 70.26) * mm});
            skLineSegment(sketch, "E1673", {"start": v(32.92, 70.26) * mm, "end": v(31, 71.19) * mm});
            skLineSegment(sketch, "E1674", {"start": v(31, 71.19) * mm, "end": v(27.95, 72.41) * mm});
            skLineSegment(sketch, "E1675", {"start": v(27.95, 72.41) * mm, "end": v(23.87, 73.68) * mm});
            skLineSegment(sketch, "E1676", {"start": v(23.87, 73.68) * mm, "end": v(18.9, 74.72) * mm});
            skLineSegment(sketch, "E1677", {"start": v(18.9, 74.72) * mm, "end": v(13.13, 75.29) * mm});
            skLineSegment(sketch, "E1678", {"start": v(13.13, 75.29) * mm, "end": v(6.7, 75.11) * mm});
            skLineSegment(sketch, "E1679", {"start": v(6.7, 75.11) * mm, "end": v(-0.3, 73.94) * mm});
            skLineSegment(sketch, "E1680", {"start": v(-0.3, 73.94) * mm, "end": v(-7.29, 75.11) * mm});
            skLineSegment(sketch, "E1681", {"start": v(-7.29, 75.11) * mm, "end": v(-13.72, 75.29) * mm});
            skLineSegment(sketch, "E1682", {"start": v(-13.72, 75.29) * mm, "end": v(-19.49, 74.72) * mm});
            skLineSegment(sketch, "E1683", {"start": v(-19.49, 74.72) * mm, "end": v(-24.47, 73.68) * mm});
            skLineSegment(sketch, "E1684", {"start": v(-24.47, 73.68) * mm, "end": v(-28.54, 72.41) * mm});
            skLineSegment(sketch, "E1685", {"start": v(-28.54, 72.41) * mm, "end": v(-31.6, 71.19) * mm});
            skLineSegment(sketch, "E1686", {"start": v(-31.6, 71.19) * mm, "end": v(-33.51, 70.26) * mm});
            skLineSegment(sketch, "E1687", {"start": v(-33.51, 70.26) * mm, "end": v(-34.18, 69.9) * mm});
            skLineSegment(sketch, "E1688", {"start": v(-34.18, 69.9) * mm, "end": v(-33.46, 70.14) * mm});
            skLineSegment(sketch, "E1689", {"start": v(-33.46, 70.14) * mm, "end": v(-31.41, 70.75) * mm});
            skLineSegment(sketch, "E1690", {"start": v(-31.41, 70.75) * mm, "end": v(-28.2, 71.56) * mm});
            skLineSegment(sketch, "E1691", {"start": v(-28.2, 71.56) * mm, "end": v(-23.98, 72.4) * mm});
            skLineSegment(sketch, "E1692", {"start": v(-23.98, 72.4) * mm, "end": v(-18.92, 73.09) * mm});
            skLineSegment(sketch, "E1693", {"start": v(-18.92, 73.09) * mm, "end": v(-13.17, 73.47) * mm});
            skLineSegment(sketch, "E1694", {"start": v(-13.17, 73.47) * mm, "end": v(-6.91, 73.37) * mm});
            skLineSegment(sketch, "E1695", {"start": v(-6.91, 73.37) * mm, "end": v(-0.3, 72.61) * mm});
            skLineSegment(sketch, "E1696", {"start": v(-0.13, -69.53) * mm, "end": v(0.9, -68.2) * mm});
            skLineSegment(sketch, "E1697", {"start": v(0.9, -68.2) * mm, "end": v(1.62, -66.68) * mm});
            skLineSegment(sketch, "E1698", {"start": v(1.62, -66.68) * mm, "end": v(2.08, -65.07) * mm});
            skLineSegment(sketch, "E1699", {"start": v(2.08, -65.07) * mm, "end": v(2.34, -63.5) * mm});
            skLineSegment(sketch, "E1700", {"start": v(2.34, -63.5) * mm, "end": v(2.45, -62.06) * mm});
            skLineSegment(sketch, "E1701", {"start": v(2.45, -62.06) * mm, "end": v(2.46, -60.9) * mm});
            skLineSegment(sketch, "E1702", {"start": v(2.46, -60.9) * mm, "end": v(2.42, -60.11) * mm});
            skLineSegment(sketch, "E1703", {"start": v(2.42, -60.11) * mm, "end": v(2.4, -59.83) * mm});
            skLineSegment(sketch, "E1704", {"start": v(2.4, -59.83) * mm, "end": v(3.45, -60.1) * mm});
            skLineSegment(sketch, "E1705", {"start": v(3.45, -60.1) * mm, "end": v(4.33, -60.44) * mm});
            skLineSegment(sketch, "E1706", {"start": v(4.33, -60.44) * mm, "end": v(5.06, -60.8) * mm});
            skLineSegment(sketch, "E1707", {"start": v(5.06, -60.8) * mm, "end": v(5.64, -61.17) * mm});
            skLineSegment(sketch, "E1708", {"start": v(5.64, -61.17) * mm, "end": v(6.09, -61.5) * mm});
            skLineSegment(sketch, "E1709", {"start": v(6.09, -61.5) * mm, "end": v(6.4, -61.78) * mm});
            skLineSegment(sketch, "E1710", {"start": v(6.4, -61.78) * mm, "end": v(6.57, -61.96) * mm});
            skLineSegment(sketch, "E1711", {"start": v(6.57, -61.96) * mm, "end": v(6.63, -62.03) * mm});
            skLineSegment(sketch, "E1712", {"start": v(6.63, -62.03) * mm, "end": v(6.89, -61.71) * mm});
            skLineSegment(sketch, "E1713", {"start": v(6.89, -61.71) * mm, "end": v(7.07, -61.1) * mm});
            skLineSegment(sketch, "E1714", {"start": v(7.07, -61.1) * mm, "end": v(7.2, -60.3) * mm});
            skLineSegment(sketch, "E1715", {"start": v(7.2, -60.3) * mm, "end": v(7.27, -59.41) * mm});
            skLineSegment(sketch, "E1716", {"start": v(7.27, -59.41) * mm, "end": v(7.31, -58.54) * mm});
            skLineSegment(sketch, "E1717", {"start": v(7.31, -58.54) * mm, "end": v(7.33, -57.78) * mm});
            skLineSegment(sketch, "E1718", {"start": v(7.33, -57.78) * mm, "end": v(7.33, -57.26) * mm});
            skLineSegment(sketch, "E1719", {"start": v(7.33, -57.26) * mm, "end": v(7.32, -57.06) * mm});
            skLineSegment(sketch, "E1720", {"start": v(7.32, -57.06) * mm, "end": v(7.96, -57.16) * mm});
            skLineSegment(sketch, "E1721", {"start": v(7.96, -57.16) * mm, "end": v(8.54, -57.35) * mm});
            skLineSegment(sketch, "E1722", {"start": v(8.54, -57.35) * mm, "end": v(9.05, -57.6) * mm});
            skLineSegment(sketch, "E1723", {"start": v(9.05, -57.6) * mm, "end": v(9.48, -57.86) * mm});
            skLineSegment(sketch, "E1724", {"start": v(9.48, -57.86) * mm, "end": v(9.84, -58.11) * mm});
            skLineSegment(sketch, "E1725", {"start": v(9.84, -58.11) * mm, "end": v(10.1, -58.33) * mm});
            skLineSegment(sketch, "E1726", {"start": v(10.1, -58.33) * mm, "end": v(10.27, -58.49) * mm});
            skLineSegment(sketch, "E1727", {"start": v(10.27, -58.49) * mm, "end": v(10.32, -58.55) * mm});
            skLineSegment(sketch, "E1728", {"start": v(10.32, -58.55) * mm, "end": v(10.66, -58.3) * mm});
            skLineSegment(sketch, "E1729", {"start": v(10.66, -58.3) * mm, "end": v(11.02, -57.86) * mm});
            skLineSegment(sketch, "E1730", {"start": v(11.02, -57.86) * mm, "end": v(11.38, -57.3) * mm});
            skLineSegment(sketch, "E1731", {"start": v(11.38, -57.3) * mm, "end": v(11.71, -56.69) * mm});
            skLineSegment(sketch, "E1732", {"start": v(11.71, -56.69) * mm, "end": v(12.01, -56.1) * mm});
            skLineSegment(sketch, "E1733", {"start": v(12.01, -56.1) * mm, "end": v(12.25, -55.59) * mm});
            skLineSegment(sketch, "E1734", {"start": v(12.25, -55.59) * mm, "end": v(12.4, -55.23) * mm});
            skLineSegment(sketch, "E1735", {"start": v(12.4, -55.23) * mm, "end": v(12.47, -55.1) * mm});
            skLineSegment(sketch, "E1736", {"start": v(12.47, -55.1) * mm, "end": v(12.46, -55.38) * mm});
            skLineSegment(sketch, "E1737", {"start": v(12.46, -55.38) * mm, "end": v(12.42, -56.16) * mm});
            skLineSegment(sketch, "E1738", {"start": v(12.42, -56.16) * mm, "end": v(12.32, -57.31) * mm});
            skLineSegment(sketch, "E1739", {"start": v(12.32, -57.31) * mm, "end": v(12.15, -58.72) * mm});
            skLineSegment(sketch, "E1740", {"start": v(12.15, -58.72) * mm, "end": v(11.87, -60.27) * mm});
            skLineSegment(sketch, "E1741", {"start": v(11.87, -60.27) * mm, "end": v(11.48, -61.84) * mm});
            skLineSegment(sketch, "E1742", {"start": v(11.48, -61.84) * mm, "end": v(10.94, -63.3) * mm});
            skLineSegment(sketch, "E1743", {"start": v(10.94, -63.3) * mm, "end": v(10.23, -64.55) * mm});
            skLineSegment(sketch, "E1744", {"start": v(10.23, -64.55) * mm, "end": v(10.22, -64.41) * mm});
            skLineSegment(sketch, "E1745", {"start": v(10.22, -64.41) * mm, "end": v(10.18, -64.05) * mm});
            skLineSegment(sketch, "E1746", {"start": v(10.18, -64.05) * mm, "end": v(10.09, -63.55) * mm});
            skLineSegment(sketch, "E1747", {"start": v(10.09, -63.55) * mm, "end": v(9.93, -62.98) * mm});
            skLineSegment(sketch, "E1748", {"start": v(9.93, -62.98) * mm, "end": v(9.7, -62.43) * mm});
            skLineSegment(sketch, "E1749", {"start": v(9.7, -62.43) * mm, "end": v(9.37, -61.96) * mm});
            skLineSegment(sketch, "E1750", {"start": v(9.37, -61.96) * mm, "end": v(8.93, -61.67) * mm});
            skLineSegment(sketch, "E1751", {"start": v(8.93, -61.67) * mm, "end": v(8.37, -61.62) * mm});
            skLineSegment(sketch, "E1752", {"start": v(8.37, -61.62) * mm, "end": v(8.38, -61.76) * mm});
            skLineSegment(sketch, "E1753", {"start": v(8.38, -61.76) * mm, "end": v(8.4, -62.15) * mm});
            skLineSegment(sketch, "E1754", {"start": v(8.4, -62.15) * mm, "end": v(8.4, -62.74) * mm});
            skLineSegment(sketch, "E1755", {"start": v(8.4, -62.74) * mm, "end": v(8.35, -63.47) * mm});
            skLineSegment(sketch, "E1756", {"start": v(8.35, -63.47) * mm, "end": v(8.21, -64.3) * mm});
            skLineSegment(sketch, "E1757", {"start": v(8.21, -64.3) * mm, "end": v(7.95, -65.18) * mm});
            skLineSegment(sketch, "E1758", {"start": v(7.95, -65.18) * mm, "end": v(7.54, -66.05) * mm});
            skLineSegment(sketch, "E1759", {"start": v(7.54, -66.05) * mm, "end": v(6.94, -66.86) * mm});
            skLineSegment(sketch, "E1760", {"start": v(6.94, -66.86) * mm, "end": v(6.9, -66.74) * mm});
            skLineSegment(sketch, "E1761", {"start": v(6.9, -66.74) * mm, "end": v(6.76, -66.42) * mm});
            skLineSegment(sketch, "E1762", {"start": v(6.76, -66.42) * mm, "end": v(6.55, -65.97) * mm});
            skLineSegment(sketch, "E1763", {"start": v(6.55, -65.97) * mm, "end": v(6.25, -65.45) * mm});
            skLineSegment(sketch, "E1764", {"start": v(6.25, -65.45) * mm, "end": v(5.88, -64.94) * mm});
            skLineSegment(sketch, "E1765", {"start": v(5.88, -64.94) * mm, "end": v(5.44, -64.5) * mm});
            skLineSegment(sketch, "E1766", {"start": v(5.44, -64.5) * mm, "end": v(4.94, -64.2) * mm});
            skLineSegment(sketch, "E1767", {"start": v(4.94, -64.2) * mm, "end": v(4.37, -64.1) * mm});
            skLineSegment(sketch, "E1768", {"start": v(4.37, -64.1) * mm, "end": v(4.38, -64.32) * mm});
            skLineSegment(sketch, "E1769", {"start": v(4.38, -64.32) * mm, "end": v(4.37, -64.92) * mm});
            skLineSegment(sketch, "E1770", {"start": v(4.37, -64.92) * mm, "end": v(4.27, -65.85) * mm});
            skLineSegment(sketch, "E1771", {"start": v(4.27, -65.85) * mm, "end": v(4, -67.04) * mm});
            skLineSegment(sketch, "E1772", {"start": v(4, -67.04) * mm, "end": v(3.5, -68.44) * mm});
            skLineSegment(sketch, "E1773", {"start": v(3.5, -68.44) * mm, "end": v(2.69, -70) * mm});
            skLineSegment(sketch, "E1774", {"start": v(2.69, -70) * mm, "end": v(1.5, -71.64) * mm});
            skLineSegment(sketch, "E1775", {"start": v(1.5, -71.64) * mm, "end": v(-0.13, -73.3) * mm});
            skLineSegment(sketch, "E1776", {"start": v(-0.13, -73.3) * mm, "end": v(-1.76, -71.64) * mm});
            skLineSegment(sketch, "E1777", {"start": v(-1.76, -71.64) * mm, "end": v(-2.94, -70) * mm});
            skLineSegment(sketch, "E1778", {"start": v(-2.94, -70) * mm, "end": v(-3.75, -68.44) * mm});
            skLineSegment(sketch, "E1779", {"start": v(-3.75, -68.44) * mm, "end": v(-4.25, -67.04) * mm});
            skLineSegment(sketch, "E1780", {"start": v(-4.25, -67.04) * mm, "end": v(-4.52, -65.85) * mm});
            skLineSegment(sketch, "E1781", {"start": v(-4.52, -65.85) * mm, "end": v(-4.62, -64.92) * mm});
            skLineSegment(sketch, "E1782", {"start": v(-4.62, -64.92) * mm, "end": v(-4.63, -64.32) * mm});
            skLineSegment(sketch, "E1783", {"start": v(-4.63, -64.32) * mm, "end": v(-4.62, -64.1) * mm});
            skLineSegment(sketch, "E1784", {"start": v(-4.62, -64.1) * mm, "end": v(-5.19, -64.2) * mm});
            skLineSegment(sketch, "E1785", {"start": v(-5.19, -64.2) * mm, "end": v(-5.7, -64.5) * mm});
            skLineSegment(sketch, "E1786", {"start": v(-5.7, -64.5) * mm, "end": v(-6.14, -64.94) * mm});
            skLineSegment(sketch, "E1787", {"start": v(-6.14, -64.94) * mm, "end": v(-6.5, -65.45) * mm});
            skLineSegment(sketch, "E1788", {"start": v(-6.5, -65.45) * mm, "end": v(-6.8, -65.97) * mm});
            skLineSegment(sketch, "E1789", {"start": v(-6.8, -65.97) * mm, "end": v(-7.02, -66.42) * mm});
            skLineSegment(sketch, "E1790", {"start": v(-7.02, -66.42) * mm, "end": v(-7.15, -66.74) * mm});
            skLineSegment(sketch, "E1791", {"start": v(-7.15, -66.74) * mm, "end": v(-7.2, -66.86) * mm});
            skLineSegment(sketch, "E1792", {"start": v(-7.2, -66.86) * mm, "end": v(-7.8, -66.05) * mm});
            skLineSegment(sketch, "E1793", {"start": v(-7.8, -66.05) * mm, "end": v(-8.2, -65.18) * mm});
            skLineSegment(sketch, "E1794", {"start": v(-8.2, -65.18) * mm, "end": v(-8.47, -64.3) * mm});
            skLineSegment(sketch, "E1795", {"start": v(-8.47, -64.3) * mm, "end": v(-8.6, -63.47) * mm});
            skLineSegment(sketch, "E1796", {"start": v(-8.6, -63.47) * mm, "end": v(-8.66, -62.74) * mm});
            skLineSegment(sketch, "E1797", {"start": v(-8.66, -62.74) * mm, "end": v(-8.66, -62.15) * mm});
            skLineSegment(sketch, "E1798", {"start": v(-8.66, -62.15) * mm, "end": v(-8.63, -61.76) * mm});
            skLineSegment(sketch, "E1799", {"start": v(-8.63, -61.76) * mm, "end": v(-8.62, -61.62) * mm});
            skLineSegment(sketch, "E1800", {"start": v(-8.62, -61.62) * mm, "end": v(-9.18, -61.67) * mm});
            skLineSegment(sketch, "E1801", {"start": v(-9.18, -61.67) * mm, "end": v(-9.62, -61.96) * mm});
            skLineSegment(sketch, "E1802", {"start": v(-9.62, -61.96) * mm, "end": v(-9.95, -62.43) * mm});
            skLineSegment(sketch, "E1803", {"start": v(-9.95, -62.43) * mm, "end": v(-10.18, -62.98) * mm});
            skLineSegment(sketch, "E1804", {"start": v(-10.18, -62.98) * mm, "end": v(-10.34, -63.55) * mm});
            skLineSegment(sketch, "E1805", {"start": v(-10.34, -63.55) * mm, "end": v(-10.43, -64.05) * mm});
            skLineSegment(sketch, "E1806", {"start": v(-10.43, -64.05) * mm, "end": v(-10.47, -64.41) * mm});
            skLineSegment(sketch, "E1807", {"start": v(-10.47, -64.41) * mm, "end": v(-10.48, -64.55) * mm});
            skLineSegment(sketch, "E1808", {"start": v(-10.48, -64.55) * mm, "end": v(-11.2, -63.3) * mm});
            skLineSegment(sketch, "E1809", {"start": v(-11.2, -63.3) * mm, "end": v(-11.73, -61.84) * mm});
            skLineSegment(sketch, "E1810", {"start": v(-11.73, -61.84) * mm, "end": v(-12.13, -60.27) * mm});
            skLineSegment(sketch, "E1811", {"start": v(-12.13, -60.27) * mm, "end": v(-12.4, -58.72) * mm});
            skLineSegment(sketch, "E1812", {"start": v(-12.4, -58.72) * mm, "end": v(-12.57, -57.31) * mm});
            skLineSegment(sketch, "E1813", {"start": v(-12.57, -57.31) * mm, "end": v(-12.67, -56.16) * mm});
            skLineSegment(sketch, "E1814", {"start": v(-12.67, -56.16) * mm, "end": v(-12.7, -55.38) * mm});
            skLineSegment(sketch, "E1815", {"start": v(-12.7, -55.38) * mm, "end": v(-12.72, -55.1) * mm});
            skLineSegment(sketch, "E1816", {"start": v(-12.72, -55.1) * mm, "end": v(-12.66, -55.23) * mm});
            skLineSegment(sketch, "E1817", {"start": v(-12.66, -55.23) * mm, "end": v(-12.5, -55.59) * mm});
            skLineSegment(sketch, "E1818", {"start": v(-12.5, -55.59) * mm, "end": v(-12.27, -56.1) * mm});
            skLineSegment(sketch, "E1819", {"start": v(-12.27, -56.1) * mm, "end": v(-11.97, -56.69) * mm});
            skLineSegment(sketch, "E1820", {"start": v(-11.97, -56.69) * mm, "end": v(-11.63, -57.3) * mm});
            skLineSegment(sketch, "E1821", {"start": v(-11.63, -57.3) * mm, "end": v(-11.27, -57.86) * mm});
            skLineSegment(sketch, "E1822", {"start": v(-11.27, -57.86) * mm, "end": v(-10.91, -58.3) * mm});
            skLineSegment(sketch, "E1823", {"start": v(-10.91, -58.3) * mm, "end": v(-10.58, -58.55) * mm});
            skLineSegment(sketch, "E1824", {"start": v(-10.58, -58.55) * mm, "end": v(-10.52, -58.49) * mm});
            skLineSegment(sketch, "E1825", {"start": v(-10.52, -58.49) * mm, "end": v(-10.36, -58.33) * mm});
            skLineSegment(sketch, "E1826", {"start": v(-10.36, -58.33) * mm, "end": v(-10.1, -58.11) * mm});
            skLineSegment(sketch, "E1827", {"start": v(-10.1, -58.11) * mm, "end": v(-9.74, -57.86) * mm});
            skLineSegment(sketch, "E1828", {"start": v(-9.74, -57.86) * mm, "end": v(-9.3, -57.6) * mm});
            skLineSegment(sketch, "E1829", {"start": v(-9.3, -57.6) * mm, "end": v(-8.79, -57.35) * mm});
            skLineSegment(sketch, "E1830", {"start": v(-8.79, -57.35) * mm, "end": v(-8.21, -57.16) * mm});
            skLineSegment(sketch, "E1831", {"start": v(-8.21, -57.16) * mm, "end": v(-7.58, -57.06) * mm});
            skLineSegment(sketch, "E1832", {"start": v(-7.58, -57.06) * mm, "end": v(-7.58, -57.26) * mm});
            skLineSegment(sketch, "E1833", {"start": v(-7.58, -57.26) * mm, "end": v(-7.58, -57.78) * mm});
            skLineSegment(sketch, "E1834", {"start": v(-7.58, -57.78) * mm, "end": v(-7.57, -58.54) * mm});
            skLineSegment(sketch, "E1835", {"start": v(-7.57, -58.54) * mm, "end": v(-7.53, -59.41) * mm});
            skLineSegment(sketch, "E1836", {"start": v(-7.53, -59.41) * mm, "end": v(-7.45, -60.3) * mm});
            skLineSegment(sketch, "E1837", {"start": v(-7.45, -60.3) * mm, "end": v(-7.32, -61.1) * mm});
            skLineSegment(sketch, "E1838", {"start": v(-7.32, -61.1) * mm, "end": v(-7.14, -61.71) * mm});
            skLineSegment(sketch, "E1839", {"start": v(-7.14, -61.71) * mm, "end": v(-6.89, -62.03) * mm});
            skLineSegment(sketch, "E1840", {"start": v(-6.89, -62.03) * mm, "end": v(-6.83, -61.96) * mm});
            skLineSegment(sketch, "E1841", {"start": v(-6.83, -61.96) * mm, "end": v(-6.65, -61.78) * mm});
            skLineSegment(sketch, "E1842", {"start": v(-6.65, -61.78) * mm, "end": v(-6.34, -61.5) * mm});
            skLineSegment(sketch, "E1843", {"start": v(-6.34, -61.5) * mm, "end": v(-5.9, -61.17) * mm});
            skLineSegment(sketch, "E1844", {"start": v(-5.9, -61.17) * mm, "end": v(-5.32, -60.8) * mm});
            skLineSegment(sketch, "E1845", {"start": v(-5.32, -60.8) * mm, "end": v(-4.59, -60.44) * mm});
            skLineSegment(sketch, "E1846", {"start": v(-4.59, -60.44) * mm, "end": v(-3.7, -60.1) * mm});
            skLineSegment(sketch, "E1847", {"start": v(-3.7, -60.1) * mm, "end": v(-2.65, -59.83) * mm});
            skLineSegment(sketch, "E1848", {"start": v(-2.65, -59.83) * mm, "end": v(-2.68, -60.12) * mm});
            skLineSegment(sketch, "E1849", {"start": v(-2.68, -60.12) * mm, "end": v(-2.72, -60.9) * mm});
            skLineSegment(sketch, "E1850", {"start": v(-2.72, -60.9) * mm, "end": v(-2.73, -62.08) * mm});
            skLineSegment(sketch, "E1851", {"start": v(-2.73, -62.08) * mm, "end": v(-2.63, -63.51) * mm});
            skLineSegment(sketch, "E1852", {"start": v(-2.63, -63.51) * mm, "end": v(-2.38, -65.1) * mm});
            skLineSegment(sketch, "E1853", {"start": v(-2.38, -65.1) * mm, "end": v(-1.92, -66.7) * mm});
            skLineSegment(sketch, "E1854", {"start": v(-1.92, -66.7) * mm, "end": v(-1.19, -68.22) * mm});
            skLineSegment(sketch, "E1855", {"start": v(-1.19, -68.22) * mm, "end": v(-0.13, -69.53) * mm});
            skLineSegment(sketch, "E1856", {"start": v(-15.95, 41.9) * mm, "end": v(-16.7, 41.92) * mm});
            skLineSegment(sketch, "E1857", {"start": v(-16.7, 41.92) * mm, "end": v(-18.68, 41.85) * mm});
            skLineSegment(sketch, "E1858", {"start": v(-18.68, 41.85) * mm, "end": v(-21.54, 41.52) * mm});
            skLineSegment(sketch, "E1859", {"start": v(-21.54, 41.52) * mm, "end": v(-24.89, 40.75) * mm});
            skLineSegment(sketch, "E1860", {"start": v(-24.89, 40.75) * mm, "end": v(-28.36, 39.36) * mm});
            skLineSegment(sketch, "E1861", {"start": v(-28.36, 39.36) * mm, "end": v(-31.58, 37.18) * mm});
            skLineSegment(sketch, "E1862", {"start": v(-31.58, 37.18) * mm, "end": v(-34.17, 34.02) * mm});
            skLineSegment(sketch, "E1863", {"start": v(-34.17, 34.02) * mm, "end": v(-35.76, 29.72) * mm});
            skLineSegment(sketch, "E1864", {"start": v(-35.76, 29.72) * mm, "end": v(-36.07, 29) * mm});
            skLineSegment(sketch, "E1865", {"start": v(-36.07, 29) * mm, "end": v(-36.9, 26.94) * mm});
            skLineSegment(sketch, "E1866", {"start": v(-36.9, 26.94) * mm, "end": v(-38.1, 23.7) * mm});
            skLineSegment(sketch, "E1867", {"start": v(-38.1, 23.7) * mm, "end": v(-39.5, 19.43) * mm});
            skLineSegment(sketch, "E1868", {"start": v(-39.5, 19.43) * mm, "end": v(-40.93, 14.28) * mm});
            skLineSegment(sketch, "E1869", {"start": v(-40.93, 14.28) * mm, "end": v(-42.23, 8.42) * mm});
            skLineSegment(sketch, "E1870", {"start": v(-42.23, 8.42) * mm, "end": v(-43.24, 2) * mm});
            skLineSegment(sketch, "E1871", {"start": v(-43.24, 2) * mm, "end": v(-43.8, -4.84) * mm});
            skLineSegment(sketch, "E1872", {"start": v(-43.8, -4.84) * mm, "end": v(-44.16, -4.98) * mm});
            skLineSegment(sketch, "E1873", {"start": v(-44.16, -4.98) * mm, "end": v(-45.14, -5.38) * mm});
            skLineSegment(sketch, "E1874", {"start": v(-45.14, -5.38) * mm, "end": v(-46.56, -6) * mm});
            skLineSegment(sketch, "E1875", {"start": v(-46.56, -6) * mm, "end": v(-48.25, -6.84) * mm});
            skLineSegment(sketch, "E1876", {"start": v(-48.25, -6.84) * mm, "end": v(-50.05, -7.85) * mm});
            skLineSegment(sketch, "E1877", {"start": v(-50.05, -7.85) * mm, "end": v(-51.78, -9.02) * mm});
            skLineSegment(sketch, "E1878", {"start": v(-51.78, -9.02) * mm, "end": v(-53.28, -10.31) * mm});
            skLineSegment(sketch, "E1879", {"start": v(-53.28, -10.31) * mm, "end": v(-54.38, -11.7) * mm});
            skLineSegment(sketch, "E1880", {"start": v(-54.38, -11.7) * mm, "end": v(-54.2, -11) * mm});
            skLineSegment(sketch, "E1881", {"start": v(-54.2, -11) * mm, "end": v(-53.7, -9.1) * mm});
            skLineSegment(sketch, "E1882", {"start": v(-53.7, -9.1) * mm, "end": v(-52.9, -6.33) * mm});
            skLineSegment(sketch, "E1883", {"start": v(-52.9, -6.33) * mm, "end": v(-51.8, -3) * mm});
            skLineSegment(sketch, "E1884", {"start": v(-51.8, -3) * mm, "end": v(-50.45, 0.54) * mm});
            skLineSegment(sketch, "E1885", {"start": v(-50.45, 0.54) * mm, "end": v(-48.85, 4) * mm});
            skLineSegment(sketch, "E1886", {"start": v(-48.85, 4) * mm, "end": v(-47.04, 7.03) * mm});
            skLineSegment(sketch, "E1887", {"start": v(-47.04, 7.03) * mm, "end": v(-45.03, 9.31) * mm});
            skLineSegment(sketch, "E1888", {"start": v(-45.03, 9.31) * mm, "end": v(-45.74, 9.5) * mm});
            skLineSegment(sketch, "E1889", {"start": v(-45.74, 9.5) * mm, "end": v(-47.7, 9.86) * mm});
            skLineSegment(sketch, "E1890", {"start": v(-47.7, 9.86) * mm, "end": v(-50.64, 10.15) * mm});
            skLineSegment(sketch, "E1891", {"start": v(-50.64, 10.15) * mm, "end": v(-54.33, 10.08) * mm});
            skLineSegment(sketch, "E1892", {"start": v(-54.33, 10.08) * mm, "end": v(-58.5, 9.4) * mm});
            skLineSegment(sketch, "E1893", {"start": v(-58.5, 9.4) * mm, "end": v(-62.92, 7.85) * mm});
            skLineSegment(sketch, "E1894", {"start": v(-62.92, 7.85) * mm, "end": v(-67.32, 5.14) * mm});
            skLineSegment(sketch, "E1895", {"start": v(-67.32, 5.14) * mm, "end": v(-71.44, 1.02) * mm});
            skLineSegment(sketch, "E1896", {"start": v(-71.44, 1.02) * mm, "end": v(-71.2, 1.95) * mm});
            skLineSegment(sketch, "E1897", {"start": v(-71.2, 1.95) * mm, "end": v(-70.46, 4.45) * mm});
            skLineSegment(sketch, "E1898", {"start": v(-70.46, 4.45) * mm, "end": v(-69.28, 8.08) * mm});
            skLineSegment(sketch, "E1899", {"start": v(-69.28, 8.08) * mm, "end": v(-67.68, 12.43) * mm});
            skLineSegment(sketch, "E1900", {"start": v(-67.68, 12.43) * mm, "end": v(-65.68, 17.07) * mm});
            skLineSegment(sketch, "E1901", {"start": v(-65.68, 17.07) * mm, "end": v(-63.3, 21.56) * mm});
            skLineSegment(sketch, "E1902", {"start": v(-63.3, 21.56) * mm, "end": v(-60.6, 25.48) * mm});
            skLineSegment(sketch, "E1903", {"start": v(-60.6, 25.48) * mm, "end": v(-57.56, 28.4) * mm});
            skLineSegment(sketch, "E1904", {"start": v(-57.56, 28.4) * mm, "end": v(-58.07, 28.35) * mm});
            skLineSegment(sketch, "E1905", {"start": v(-58.07, 28.35) * mm, "end": v(-59.45, 28.18) * mm});
            skLineSegment(sketch, "E1906", {"start": v(-59.45, 28.18) * mm, "end": v(-61.48, 27.87) * mm});
            skLineSegment(sketch, "E1907", {"start": v(-61.48, 27.87) * mm, "end": v(-63.95, 27.38) * mm});
            skLineSegment(sketch, "E1908", {"start": v(-63.95, 27.38) * mm, "end": v(-66.61, 26.67) * mm});
            skLineSegment(sketch, "E1909", {"start": v(-66.61, 26.67) * mm, "end": v(-69.27, 25.73) * mm});
            skLineSegment(sketch, "E1910", {"start": v(-69.27, 25.73) * mm, "end": v(-71.7, 24.5) * mm});
            skLineSegment(sketch, "E1911", {"start": v(-71.7, 24.5) * mm, "end": v(-73.66, 22.98) * mm});
            skLineSegment(sketch, "E1912", {"start": v(-73.66, 22.98) * mm, "end": v(-73.35, 23.91) * mm});
            skLineSegment(sketch, "E1913", {"start": v(-73.35, 23.91) * mm, "end": v(-72.33, 26.49) * mm});
            skLineSegment(sketch, "E1914", {"start": v(-72.33, 26.49) * mm, "end": v(-70.4, 30.39) * mm});
            skLineSegment(sketch, "E1915", {"start": v(-70.4, 30.39) * mm, "end": v(-67.43, 35.28) * mm});
            skLineSegment(sketch, "E1916", {"start": v(-67.43, 35.28) * mm, "end": v(-63.23, 40.84) * mm});
            skLineSegment(sketch, "E1917", {"start": v(-63.23, 40.84) * mm, "end": v(-57.63, 46.73) * mm});
            skLineSegment(sketch, "E1918", {"start": v(-57.63, 46.73) * mm, "end": v(-50.47, 52.63) * mm});
            skLineSegment(sketch, "E1919", {"start": v(-50.47, 52.63) * mm, "end": v(-41.57, 58.22) * mm});
            skLineSegment(sketch, "E1920", {"start": v(-41.57, 58.22) * mm, "end": v(-40.86, 58.57) * mm});
            skLineSegment(sketch, "E1921", {"start": v(-40.86, 58.57) * mm, "end": v(-38.93, 59.43) * mm});
            skLineSegment(sketch, "E1922", {"start": v(-38.93, 59.43) * mm, "end": v(-36, 60.49) * mm});
            skLineSegment(sketch, "E1923", {"start": v(-36, 60.49) * mm, "end": v(-32.33, 61.44) * mm});
            skLineSegment(sketch, "E1924", {"start": v(-32.33, 61.44) * mm, "end": v(-28.16, 62) * mm});
            skLineSegment(sketch, "E1925", {"start": v(-28.16, 62) * mm, "end": v(-23.75, 61.85) * mm});
            skLineSegment(sketch, "E1926", {"start": v(-23.75, 61.85) * mm, "end": v(-19.35, 60.69) * mm});
            skLineSegment(sketch, "E1927", {"start": v(-19.35, 60.69) * mm, "end": v(-15.19, 58.22) * mm});
            skLineSegment(sketch, "E1928", {"start": v(-15.19, 58.22) * mm, "end": v(-15.8, 58.47) * mm});
            skLineSegment(sketch, "E1929", {"start": v(-15.8, 58.47) * mm, "end": v(-17.52, 59.07) * mm});
            skLineSegment(sketch, "E1930", {"start": v(-17.52, 59.07) * mm, "end": v(-20.14, 59.76) * mm});
            skLineSegment(sketch, "E1931", {"start": v(-20.14, 59.76) * mm, "end": v(-23.45, 60.3) * mm});
            skLineSegment(sketch, "E1932", {"start": v(-23.45, 60.3) * mm, "end": v(-27.25, 60.43) * mm});
            skLineSegment(sketch, "E1933", {"start": v(-27.25, 60.43) * mm, "end": v(-31.35, 59.91) * mm});
            skLineSegment(sketch, "E1934", {"start": v(-31.35, 59.91) * mm, "end": v(-35.52, 58.5) * mm});
            skLineSegment(sketch, "E1935", {"start": v(-35.52, 58.5) * mm, "end": v(-39.58, 55.92) * mm});
            skLineSegment(sketch, "E1936", {"start": v(-39.58, 55.92) * mm, "end": v(-42.88, 52.97) * mm});
            skLineSegment(sketch, "E1937", {"start": v(-42.88, 52.97) * mm, "end": v(-45.03, 50.53) * mm});
            skLineSegment(sketch, "E1938", {"start": v(-45.03, 50.53) * mm, "end": v(-46.22, 48.55) * mm});
            skLineSegment(sketch, "E1939", {"start": v(-46.22, 48.55) * mm, "end": v(-46.64, 47.01) * mm});
            skLineSegment(sketch, "E1940", {"start": v(-46.64, 47.01) * mm, "end": v(-46.48, 45.85) * mm});
            skLineSegment(sketch, "E1941", {"start": v(-46.48, 45.85) * mm, "end": v(-45.93, 45.04) * mm});
            skLineSegment(sketch, "E1942", {"start": v(-45.93, 45.04) * mm, "end": v(-45.18, 44.53) * mm});
            skLineSegment(sketch, "E1943", {"start": v(-45.18, 44.53) * mm, "end": v(-44.42, 44.27) * mm});
            skLineSegment(sketch, "E1944", {"start": v(-44.42, 44.27) * mm, "end": v(-42.66, 44.51) * mm});
            skLineSegment(sketch, "E1945", {"start": v(-42.66, 44.51) * mm, "end": v(-39.1, 45.32) * mm});
            skLineSegment(sketch, "E1946", {"start": v(-39.1, 45.32) * mm, "end": v(-34.26, 46.42) * mm});
            skLineSegment(sketch, "E1947", {"start": v(-34.26, 46.42) * mm, "end": v(-28.63, 47.54) * mm});
            skLineSegment(sketch, "E1948", {"start": v(-28.63, 47.54) * mm, "end": v(-22.73, 48.4) * mm});
            skLineSegment(sketch, "E1949", {"start": v(-22.73, 48.4) * mm, "end": v(-17.07, 48.7) * mm});
            skLineSegment(sketch, "E1950", {"start": v(-17.07, 48.7) * mm, "end": v(-12.14, 48.2) * mm});
            skLineSegment(sketch, "E1951", {"start": v(-12.14, 48.2) * mm, "end": v(-8.46, 46.6) * mm});
            skLineSegment(sketch, "E1952", {"start": v(-8.46, 46.6) * mm, "end": v(-9.05, 46.72) * mm});
            skLineSegment(sketch, "E1953", {"start": v(-9.05, 46.72) * mm, "end": v(-10.7, 46.98) * mm});
            skLineSegment(sketch, "E1954", {"start": v(-10.7, 46.98) * mm, "end": v(-13.22, 47.23) * mm});
            skLineSegment(sketch, "E1955", {"start": v(-13.22, 47.23) * mm, "end": v(-16.46, 47.32) * mm});
            skLineSegment(sketch, "E1956", {"start": v(-16.46, 47.32) * mm, "end": v(-20.24, 47.1) * mm});
            skLineSegment(sketch, "E1957", {"start": v(-20.24, 47.1) * mm, "end": v(-24.4, 46.43) * mm});
            skLineSegment(sketch, "E1958", {"start": v(-24.4, 46.43) * mm, "end": v(-28.74, 45.16) * mm});
            skLineSegment(sketch, "E1959", {"start": v(-28.74, 45.16) * mm, "end": v(-33.12, 43.13) * mm});
            skLineSegment(sketch, "E1960", {"start": v(-33.12, 43.13) * mm, "end": v(-32.77, 43.25) * mm});
            skLineSegment(sketch, "E1961", {"start": v(-32.77, 43.25) * mm, "end": v(-31.76, 43.52) * mm});
            skLineSegment(sketch, "E1962", {"start": v(-31.76, 43.52) * mm, "end": v(-30.17, 43.84) * mm});
            skLineSegment(sketch, "E1963", {"start": v(-30.17, 43.84) * mm, "end": v(-28.07, 44.07) * mm});
            skLineSegment(sketch, "E1964", {"start": v(-28.07, 44.07) * mm, "end": v(-25.52, 44.12) * mm});
            skLineSegment(sketch, "E1965", {"start": v(-25.52, 44.12) * mm, "end": v(-22.6, 43.85) * mm});
            skLineSegment(sketch, "E1966", {"start": v(-22.6, 43.85) * mm, "end": v(-19.4, 43.15) * mm});
            skLineSegment(sketch, "E1967", {"start": v(-19.4, 43.15) * mm, "end": v(-15.95, 41.9) * mm});
            skLineSegment(sketch, "E1968", {"start": v(-57.16, 70.98) * mm, "end": v(-56.95, 70.78) * mm});
            skLineSegment(sketch, "E1969", {"start": v(-56.95, 70.78) * mm, "end": v(-56.37, 70.28) * mm});
            skLineSegment(sketch, "E1970", {"start": v(-56.37, 70.28) * mm, "end": v(-55.43, 69.55) * mm});
            skLineSegment(sketch, "E1971", {"start": v(-55.43, 69.55) * mm, "end": v(-54.18, 68.72) * mm});
            skLineSegment(sketch, "E1972", {"start": v(-54.18, 68.72) * mm, "end": v(-52.63, 67.89) * mm});
            skLineSegment(sketch, "E1973", {"start": v(-52.63, 67.89) * mm, "end": v(-50.84, 67.14) * mm});
            skLineSegment(sketch, "E1974", {"start": v(-50.84, 67.14) * mm, "end": v(-48.82, 66.6) * mm});
            skLineSegment(sketch, "E1975", {"start": v(-48.82, 66.6) * mm, "end": v(-46.6, 66.37) * mm});
            skLineSegment(sketch, "E1976", {"start": v(-46.6, 66.37) * mm, "end": v(-44, 66.62) * mm});
            skLineSegment(sketch, "E1977", {"start": v(-44, 66.62) * mm, "end": v(-40.84, 67.28) * mm});
            skLineSegment(sketch, "E1978", {"start": v(-40.84, 67.28) * mm, "end": v(-37.2, 68.07) * mm});
            skLineSegment(sketch, "E1979", {"start": v(-37.2, 68.07) * mm, "end": v(-33.2, 68.7) * mm});
            skLineSegment(sketch, "E1980", {"start": v(-33.2, 68.7) * mm, "end": v(-28.9, 68.88) * mm});
            skLineSegment(sketch, "E1981", {"start": v(-28.9, 68.88) * mm, "end": v(-24.39, 68.31) * mm});
            skLineSegment(sketch, "E1982", {"start": v(-24.39, 68.31) * mm, "end": v(-19.77, 66.73) * mm});
            skLineSegment(sketch, "E1983", {"start": v(-19.77, 66.73) * mm, "end": v(-15.12, 63.82) * mm});
            skLineSegment(sketch, "E1984", {"start": v(-15.12, 63.82) * mm, "end": v(-15.18, 64.03) * mm});
            skLineSegment(sketch, "E1985", {"start": v(-15.18, 64.03) * mm, "end": v(-15.37, 64.59) * mm});
            skLineSegment(sketch, "E1986", {"start": v(-15.37, 64.59) * mm, "end": v(-15.7, 65.4) * mm});
            skLineSegment(sketch, "E1987", {"start": v(-15.7, 65.4) * mm, "end": v(-16.16, 66.38) * mm});
            skLineSegment(sketch, "E1988", {"start": v(-16.16, 66.38) * mm, "end": v(-16.77, 67.41) * mm});
            skLineSegment(sketch, "E1989", {"start": v(-16.77, 67.41) * mm, "end": v(-17.54, 68.42) * mm});
            skLineSegment(sketch, "E1990", {"start": v(-17.54, 68.42) * mm, "end": v(-18.47, 69.3) * mm});
            skLineSegment(sketch, "E1991", {"start": v(-18.47, 69.3) * mm, "end": v(-19.57, 69.94) * mm});
            skLineSegment(sketch, "E1992", {"start": v(-19.57, 69.94) * mm, "end": v(-19.1, 69.94) * mm});
            skLineSegment(sketch, "E1993", {"start": v(-19.1, 69.94) * mm, "end": v(-17.81, 69.92) * mm});
            skLineSegment(sketch, "E1994", {"start": v(-17.81, 69.92) * mm, "end": v(-15.94, 69.84) * mm});
            skLineSegment(sketch, "E1995", {"start": v(-15.94, 69.84) * mm, "end": v(-13.69, 69.67) * mm});
            skLineSegment(sketch, "E1996", {"start": v(-13.69, 69.67) * mm, "end": v(-11.28, 69.38) * mm});
            skLineSegment(sketch, "E1997", {"start": v(-11.28, 69.38) * mm, "end": v(-8.93, 68.93) * mm});
            skLineSegment(sketch, "E1998", {"start": v(-8.93, 68.93) * mm, "end": v(-6.86, 68.28) * mm});
            skLineSegment(sketch, "E1999", {"start": v(-6.86, 68.28) * mm, "end": v(-5.28, 67.4) * mm});
            skLineSegment(sketch, "E2000", {"start": v(-5.28, 67.4) * mm, "end": v(-5.14, 67.48) * mm});
            skLineSegment(sketch, "E2001", {"start": v(-5.14, 67.48) * mm, "end": v(-4.77, 67.7) * mm});
            skLineSegment(sketch, "E2002", {"start": v(-4.77, 67.7) * mm, "end": v(-4.24, 68.04) * mm});
            skLineSegment(sketch, "E2003", {"start": v(-4.24, 68.04) * mm, "end": v(-3.63, 68.48) * mm});
            skLineSegment(sketch, "E2004", {"start": v(-3.63, 68.48) * mm, "end": v(-3, 69.02) * mm});
            skLineSegment(sketch, "E2005", {"start": v(-3, 69.02) * mm, "end": v(-2.42, 69.62) * mm});
            skLineSegment(sketch, "E2006", {"start": v(-2.42, 69.62) * mm, "end": v(-1.97, 70.28) * mm});
            skLineSegment(sketch, "E2007", {"start": v(-1.97, 70.28) * mm, "end": v(-1.73, 70.98) * mm});
            skLineSegment(sketch, "E2008", {"start": v(-1.73, 70.98) * mm, "end": v(-2.53, 71.59) * mm});
            skLineSegment(sketch, "E2009", {"start": v(-2.53, 71.59) * mm, "end": v(-4.97, 72) * mm});
            skLineSegment(sketch, "E2010", {"start": v(-4.97, 72) * mm, "end": v(-8.67, 72.18) * mm});
            skLineSegment(sketch, "E2011", {"start": v(-8.67, 72.18) * mm, "end": v(-13.3, 72.14) * mm});
            skLineSegment(sketch, "E2012", {"start": v(-13.3, 72.14) * mm, "end": v(-18.5, 71.86) * mm});
            skLineSegment(sketch, "E2013", {"start": v(-18.5, 71.86) * mm, "end": v(-23.91, 71.32) * mm});
            skLineSegment(sketch, "E2014", {"start": v(-23.91, 71.32) * mm, "end": v(-29.2, 70.51) * mm});
            skLineSegment(sketch, "E2015", {"start": v(-29.2, 70.51) * mm, "end": v(-34, 69.43) * mm});
            skLineSegment(sketch, "E2016", {"start": v(-34, 69.43) * mm, "end": v(-36.42, 68.91) * mm});
            skLineSegment(sketch, "E2017", {"start": v(-36.42, 68.91) * mm, "end": v(-39.44, 68.51) * mm});
            skLineSegment(sketch, "E2018", {"start": v(-39.44, 68.51) * mm, "end": v(-42.84, 68.27) * mm});
            skLineSegment(sketch, "E2019", {"start": v(-42.84, 68.27) * mm, "end": v(-46.38, 68.23) * mm});
            skLineSegment(sketch, "E2020", {"start": v(-46.38, 68.23) * mm, "end": v(-49.82, 68.43) * mm});
            skLineSegment(sketch, "E2021", {"start": v(-49.82, 68.43) * mm, "end": v(-52.92, 68.93) * mm});
            skLineSegment(sketch, "E2022", {"start": v(-52.92, 68.93) * mm, "end": v(-55.45, 69.77) * mm});
            skLineSegment(sketch, "E2023", {"start": v(-55.45, 69.77) * mm, "end": v(-57.16, 70.98) * mm});
            skLineSegment(sketch, "E2024", {"start": v(42.38, 58.22) * mm, "end": v(43.9, 57.8) * mm});
            skLineSegment(sketch, "E2025", {"start": v(43.9, 57.8) * mm, "end": v(47.94, 56.41) * mm});
            skLineSegment(sketch, "E2026", {"start": v(47.94, 56.41) * mm, "end": v(53.69, 53.77) * mm});
            skLineSegment(sketch, "E2027", {"start": v(53.69, 53.77) * mm, "end": v(60.36, 49.62) * mm});
            skLineSegment(sketch, "E2028", {"start": v(60.36, 49.62) * mm, "end": v(67.15, 43.72) * mm});
            skLineSegment(sketch, "E2029", {"start": v(67.15, 43.72) * mm, "end": v(73.27, 35.81) * mm});
            skLineSegment(sketch, "E2030", {"start": v(73.27, 35.81) * mm, "end": v(77.92, 25.64) * mm});
            skLineSegment(sketch, "E2031", {"start": v(77.92, 25.64) * mm, "end": v(80.3, 12.94) * mm});
            skLineSegment(sketch, "E2032", {"start": v(80.3, 12.94) * mm, "end": v(79.98, 13.27) * mm});
            skLineSegment(sketch, "E2033", {"start": v(79.98, 13.27) * mm, "end": v(79.06, 14.14) * mm});
            skLineSegment(sketch, "E2034", {"start": v(79.06, 14.14) * mm, "end": v(77.66, 15.4) * mm});
            skLineSegment(sketch, "E2035", {"start": v(77.66, 15.4) * mm, "end": v(75.86, 16.9) * mm});
            skLineSegment(sketch, "E2036", {"start": v(75.86, 16.9) * mm, "end": v(73.77, 18.47) * mm});
            skLineSegment(sketch, "E2037", {"start": v(73.77, 18.47) * mm, "end": v(71.5, 19.96) * mm});
            skLineSegment(sketch, "E2038", {"start": v(71.5, 19.96) * mm, "end": v(69.11, 21.2) * mm});
            skLineSegment(sketch, "E2039", {"start": v(69.11, 21.2) * mm, "end": v(66.73, 22.03) * mm});
            skLineSegment(sketch, "E2040", {"start": v(66.73, 22.03) * mm, "end": v(67.14, 21.53) * mm});
            skLineSegment(sketch, "E2041", {"start": v(67.14, 21.53) * mm, "end": v(68.2, 20) * mm});
            skLineSegment(sketch, "E2042", {"start": v(68.2, 20) * mm, "end": v(69.7, 17.46) * mm});
            skLineSegment(sketch, "E2043", {"start": v(69.7, 17.46) * mm, "end": v(71.46, 13.9) * mm});
            skLineSegment(sketch, "E2044", {"start": v(71.46, 13.9) * mm, "end": v(73.23, 9.34) * mm});
            skLineSegment(sketch, "E2045", {"start": v(73.23, 9.34) * mm, "end": v(74.83, 3.75) * mm});
            skLineSegment(sketch, "E2046", {"start": v(74.83, 3.75) * mm, "end": v(76.04, -2.85) * mm});
            skLineSegment(sketch, "E2047", {"start": v(76.04, -2.85) * mm, "end": v(76.64, -10.46) * mm});
            skLineSegment(sketch, "E2048", {"start": v(76.64, -10.46) * mm, "end": v(75.95, -9.8) * mm});
            skLineSegment(sketch, "E2049", {"start": v(75.95, -9.8) * mm, "end": v(74.05, -8.04) * mm});
            skLineSegment(sketch, "E2050", {"start": v(74.05, -8.04) * mm, "end": v(71.21, -5.53) * mm});
            skLineSegment(sketch, "E2051", {"start": v(71.21, -5.53) * mm, "end": v(67.7, -2.61) * mm});
            skLineSegment(sketch, "E2052", {"start": v(67.7, -2.61) * mm, "end": v(63.78, 0.36) * mm});
            skLineSegment(sketch, "E2053", {"start": v(63.78, 0.36) * mm, "end": v(59.73, 3.04) * mm});
            skLineSegment(sketch, "E2054", {"start": v(59.73, 3.04) * mm, "end": v(55.8, 5.08) * mm});
            skLineSegment(sketch, "E2055", {"start": v(55.8, 5.08) * mm, "end": v(52.29, 6.13) * mm});
            skLineSegment(sketch, "E2056", {"start": v(52.29, 6.13) * mm, "end": v(52.68, 5.6) * mm});
            skLineSegment(sketch, "E2057", {"start": v(52.68, 5.6) * mm, "end": v(53.7, 4.06) * mm});
            skLineSegment(sketch, "E2058", {"start": v(53.7, 4.06) * mm, "end": v(55.16, 1.55) * mm});
            skLineSegment(sketch, "E2059", {"start": v(55.16, 1.55) * mm, "end": v(56.83, -1.9) * mm});
            skLineSegment(sketch, "E2060", {"start": v(56.83, -1.9) * mm, "end": v(58.5, -6.21) * mm});
            skLineSegment(sketch, "E2061", {"start": v(58.5, -6.21) * mm, "end": v(59.95, -11.37) * mm});
            skLineSegment(sketch, "E2062", {"start": v(59.95, -11.37) * mm, "end": v(60.98, -17.32) * mm});
            skLineSegment(sketch, "E2063", {"start": v(60.98, -17.32) * mm, "end": v(61.37, -24) * mm});
            skLineSegment(sketch, "E2064", {"start": v(61.37, -24) * mm, "end": v(60.81, -23.48) * mm});
            skLineSegment(sketch, "E2065", {"start": v(60.81, -23.48) * mm, "end": v(59.23, -22.1) * mm});
            skLineSegment(sketch, "E2066", {"start": v(59.23, -22.1) * mm, "end": v(56.71, -20.15) * mm});
            skLineSegment(sketch, "E2067", {"start": v(56.71, -20.15) * mm, "end": v(53.38, -17.9) * mm});
            skLineSegment(sketch, "E2068", {"start": v(53.38, -17.9) * mm, "end": v(49.34, -15.67) * mm});
            skLineSegment(sketch, "E2069", {"start": v(49.34, -15.67) * mm, "end": v(44.69, -13.72) * mm});
            skLineSegment(sketch, "E2070", {"start": v(44.69, -13.72) * mm, "end": v(39.54, -12.34) * mm});
            skLineSegment(sketch, "E2071", {"start": v(39.54, -12.34) * mm, "end": v(34.01, -11.81) * mm});
            skLineSegment(sketch, "E2072", {"start": v(34.01, -11.81) * mm, "end": v(34.26, -11.44) * mm});
            skLineSegment(sketch, "E2073", {"start": v(34.26, -11.44) * mm, "end": v(34.91, -10.37) * mm});
            skLineSegment(sketch, "E2074", {"start": v(34.91, -10.37) * mm, "end": v(35.83, -8.63) * mm});
            skLineSegment(sketch, "E2075", {"start": v(35.83, -8.63) * mm, "end": v(36.88, -6.27) * mm});
            skLineSegment(sketch, "E2076", {"start": v(36.88, -6.27) * mm, "end": v(37.92, -3.34) * mm});
            skLineSegment(sketch, "E2077", {"start": v(37.92, -3.34) * mm, "end": v(38.8, 0.11) * mm});
            skLineSegment(sketch, "E2078", {"start": v(38.8, 0.11) * mm, "end": v(39.4, 4.05) * mm});
            skLineSegment(sketch, "E2079", {"start": v(39.4, 4.05) * mm, "end": v(39.58, 8.42) * mm});
            skLineSegment(sketch, "E2080", {"start": v(39.58, 8.42) * mm, "end": v(39.74, 8.01) * mm});
            skLineSegment(sketch, "E2081", {"start": v(39.74, 8.01) * mm, "end": v(40.13, 6.89) * mm});
            skLineSegment(sketch, "E2082", {"start": v(40.13, 6.89) * mm, "end": v(40.68, 5.2) * mm});
            skLineSegment(sketch, "E2083", {"start": v(40.68, 5.2) * mm, "end": v(41.28, 3.1) * mm});
            skLineSegment(sketch, "E2084", {"start": v(41.28, 3.1) * mm, "end": v(41.84, 0.73) * mm});
            skLineSegment(sketch, "E2085", {"start": v(41.84, 0.73) * mm, "end": v(42.28, -1.76) * mm});
            skLineSegment(sketch, "E2086", {"start": v(42.28, -1.76) * mm, "end": v(42.49, -4.2) * mm});
            skLineSegment(sketch, "E2087", {"start": v(42.49, -4.2) * mm, "end": v(42.38, -6.45) * mm});
            skLineSegment(sketch, "E2088", {"start": v(42.38, -6.45) * mm, "end": v(42.87, -6.68) * mm});
            skLineSegment(sketch, "E2089", {"start": v(42.87, -6.68) * mm, "end": v(44.2, -7.33) * mm});
            skLineSegment(sketch, "E2090", {"start": v(44.2, -7.33) * mm, "end": v(46.1, -8.3) * mm});
            skLineSegment(sketch, "E2091", {"start": v(46.1, -8.3) * mm, "end": v(48.39, -9.55) * mm});
            skLineSegment(sketch, "E2092", {"start": v(48.39, -9.55) * mm, "end": v(50.8, -10.97) * mm});
            skLineSegment(sketch, "E2093", {"start": v(50.8, -10.97) * mm, "end": v(53.14, -12.5) * mm});
            skLineSegment(sketch, "E2094", {"start": v(53.14, -12.5) * mm, "end": v(55.15, -14.04) * mm});
            skLineSegment(sketch, "E2095", {"start": v(55.15, -14.04) * mm, "end": v(56.62, -15.54) * mm});
            skLineSegment(sketch, "E2096", {"start": v(56.62, -15.54) * mm, "end": v(56.5, -14.82) * mm});
            skLineSegment(sketch, "E2097", {"start": v(56.5, -14.82) * mm, "end": v(56.14, -12.85) * mm});
            skLineSegment(sketch, "E2098", {"start": v(56.14, -12.85) * mm, "end": v(55.5, -9.94) * mm});
            skLineSegment(sketch, "E2099", {"start": v(55.5, -9.94) * mm, "end": v(54.57, -6.39) * mm});
            skLineSegment(sketch, "E2100", {"start": v(54.57, -6.39) * mm, "end": v(53.32, -2.5) * mm});
            skLineSegment(sketch, "E2101", {"start": v(53.32, -2.5) * mm, "end": v(51.73, 1.41) * mm});
            skLineSegment(sketch, "E2102", {"start": v(51.73, 1.41) * mm, "end": v(49.76, 5.06) * mm});
            skLineSegment(sketch, "E2103", {"start": v(49.76, 5.06) * mm, "end": v(47.4, 8.13) * mm});
            skLineSegment(sketch, "E2104", {"start": v(47.4, 8.13) * mm, "end": v(47.95, 8.25) * mm});
            skLineSegment(sketch, "E2105", {"start": v(47.95, 8.25) * mm, "end": v(49.51, 8.47) * mm});
            skLineSegment(sketch, "E2106", {"start": v(49.51, 8.47) * mm, "end": v(51.96, 8.53) * mm});
            skLineSegment(sketch, "E2107", {"start": v(51.96, 8.53) * mm, "end": v(55.17, 8.18) * mm});
            skLineSegment(sketch, "E2108", {"start": v(55.17, 8.18) * mm, "end": v(59, 7.17) * mm});
            skLineSegment(sketch, "E2109", {"start": v(59, 7.17) * mm, "end": v(63.34, 5.26) * mm});
            skLineSegment(sketch, "E2110", {"start": v(63.34, 5.26) * mm, "end": v(68.04, 2.2) * mm});
            skLineSegment(sketch, "E2111", {"start": v(68.04, 2.2) * mm, "end": v(72.98, -2.27) * mm});
            skLineSegment(sketch, "E2112", {"start": v(72.98, -2.27) * mm, "end": v(72.8, -1.39) * mm});
            skLineSegment(sketch, "E2113", {"start": v(72.8, -1.39) * mm, "end": v(72.22, 1.01) * mm});
            skLineSegment(sketch, "E2114", {"start": v(72.22, 1.01) * mm, "end": v(71.28, 4.55) * mm});
            skLineSegment(sketch, "E2115", {"start": v(71.28, 4.55) * mm, "end": v(69.97, 8.84) * mm});
            skLineSegment(sketch, "E2116", {"start": v(69.97, 8.84) * mm, "end": v(68.3, 13.5) * mm});
            skLineSegment(sketch, "E2117", {"start": v(68.3, 13.5) * mm, "end": v(66.27, 18.16) * mm});
            skLineSegment(sketch, "E2118", {"start": v(66.27, 18.16) * mm, "end": v(63.89, 22.44) * mm});
            skLineSegment(sketch, "E2119", {"start": v(63.89, 22.44) * mm, "end": v(61.16, 25.95) * mm});
            skLineSegment(sketch, "E2120", {"start": v(61.16, 25.95) * mm, "end": v(61.47, 25.91) * mm});
            skLineSegment(sketch, "E2121", {"start": v(61.47, 25.91) * mm, "end": v(62.33, 25.78) * mm});
            skLineSegment(sketch, "E2122", {"start": v(62.33, 25.78) * mm, "end": v(63.7, 25.5) * mm});
            skLineSegment(sketch, "E2123", {"start": v(63.7, 25.5) * mm, "end": v(65.47, 25.03) * mm});
            skLineSegment(sketch, "E2124", {"start": v(65.47, 25.03) * mm, "end": v(67.6, 24.32) * mm});
            skLineSegment(sketch, "E2125", {"start": v(67.6, 24.32) * mm, "end": v(70, 23.33) * mm});
            skLineSegment(sketch, "E2126", {"start": v(70, 23.33) * mm, "end": v(72.62, 22.01) * mm});
            skLineSegment(sketch, "E2127", {"start": v(72.62, 22.01) * mm, "end": v(75.36, 20.32) * mm});
            skLineSegment(sketch, "E2128", {"start": v(75.36, 20.32) * mm, "end": v(75.07, 21.49) * mm});
            skLineSegment(sketch, "E2129", {"start": v(75.07, 21.49) * mm, "end": v(74.06, 24.67) * mm});
            skLineSegment(sketch, "E2130", {"start": v(74.06, 24.67) * mm, "end": v(72.16, 29.36) * mm});
            skLineSegment(sketch, "E2131", {"start": v(72.16, 29.36) * mm, "end": v(69.15, 35.07) * mm});
            skLineSegment(sketch, "E2132", {"start": v(69.15, 35.07) * mm, "end": v(64.87, 41.31) * mm});
            skLineSegment(sketch, "E2133", {"start": v(64.87, 41.31) * mm, "end": v(59.1, 47.58) * mm});
            skLineSegment(sketch, "E2134", {"start": v(59.1, 47.58) * mm, "end": v(51.67, 53.38) * mm});
            skLineSegment(sketch, "E2135", {"start": v(51.67, 53.38) * mm, "end": v(42.38, 58.22) * mm});
            skLineSegment(sketch, "E2136", {"start": v(34, 71.13) * mm, "end": v(35.45, 71.55) * mm});
            skLineSegment(sketch, "E2137", {"start": v(35.45, 71.55) * mm, "end": v(37.02, 71.87) * mm});
            skLineSegment(sketch, "E2138", {"start": v(37.02, 71.87) * mm, "end": v(38.7, 72.09) * mm});
            skLineSegment(sketch, "E2139", {"start": v(38.7, 72.09) * mm, "end": v(40.46, 72.24) * mm});
            skLineSegment(sketch, "E2140", {"start": v(40.46, 72.24) * mm, "end": v(42.3, 72.34) * mm});
            skLineSegment(sketch, "E2141", {"start": v(42.3, 72.34) * mm, "end": v(44.17, 72.4) * mm});
            skLineSegment(sketch, "E2142", {"start": v(44.17, 72.4) * mm, "end": v(46.08, 72.47) * mm});
            skLineSegment(sketch, "E2143", {"start": v(46.08, 72.47) * mm, "end": v(48, 72.55) * mm});
            skLineSegment(sketch, "E2144", {"start": v(48, 72.55) * mm, "end": v(49.25, 72.7) * mm});
            skLineSegment(sketch, "E2145", {"start": v(49.25, 72.7) * mm, "end": v(50.61, 73.01) * mm});
            skLineSegment(sketch, "E2146", {"start": v(50.61, 73.01) * mm, "end": v(52.07, 73.37) * mm});
            skLineSegment(sketch, "E2147", {"start": v(52.07, 73.37) * mm, "end": v(53.6, 73.69) * mm});
            skLineSegment(sketch, "E2148", {"start": v(53.6, 73.69) * mm, "end": v(55.2, 73.88) * mm});
            skLineSegment(sketch, "E2149", {"start": v(55.2, 73.88) * mm, "end": v(56.84, 73.85) * mm});
            skLineSegment(sketch, "E2150", {"start": v(56.84, 73.85) * mm, "end": v(58.52, 73.5) * mm});
            skLineSegment(sketch, "E2151", {"start": v(58.52, 73.5) * mm, "end": v(60.23, 72.75) * mm});
            skLineSegment(sketch, "E2152", {"start": v(60.23, 72.75) * mm, "end": v(61.77, 70.92) * mm});
            skLineSegment(sketch, "E2153", {"start": v(61.77, 70.92) * mm, "end": v(61.57, 68.55) * mm});
            skLineSegment(sketch, "E2154", {"start": v(61.57, 68.55) * mm, "end": v(60.1, 65.89) * mm});
            skLineSegment(sketch, "E2155", {"start": v(60.1, 65.89) * mm, "end": v(57.83, 63.16) * mm});
            skLineSegment(sketch, "E2156", {"start": v(57.83, 63.16) * mm, "end": v(55.24, 60.63) * mm});
            skLineSegment(sketch, "E2157", {"start": v(55.24, 60.63) * mm, "end": v(52.8, 58.52) * mm});
            skLineSegment(sketch, "E2158", {"start": v(52.8, 58.52) * mm, "end": v(51, 57.07) * mm});
            skLineSegment(sketch, "E2159", {"start": v(51, 57.07) * mm, "end": v(50.28, 56.54) * mm});
            skLineSegment(sketch, "E2160", {"start": v(50.28, 56.54) * mm, "end": v(49.87, 56.91) * mm});
            skLineSegment(sketch, "E2161", {"start": v(49.87, 56.91) * mm, "end": v(48.7, 57.9) * mm});
            skLineSegment(sketch, "E2162", {"start": v(48.7, 57.9) * mm, "end": v(46.89, 59.28) * mm});
            skLineSegment(sketch, "E2163", {"start": v(46.89, 59.28) * mm, "end": v(44.55, 60.87) * mm});
            skLineSegment(sketch, "E2164", {"start": v(44.55, 60.87) * mm, "end": v(41.81, 62.45) * mm});
            skLineSegment(sketch, "E2165", {"start": v(41.81, 62.45) * mm, "end": v(38.77, 63.82) * mm});
            skLineSegment(sketch, "E2166", {"start": v(38.77, 63.82) * mm, "end": v(35.56, 64.78) * mm});
            skLineSegment(sketch, "E2167", {"start": v(35.56, 64.78) * mm, "end": v(32.28, 65.13) * mm});
            skLineSegment(sketch, "E2168", {"start": v(32.28, 65.13) * mm, "end": v(28.51, 64.97) * mm});
            skLineSegment(sketch, "E2169", {"start": v(28.51, 64.97) * mm, "end": v(25.47, 64.63) * mm});
            skLineSegment(sketch, "E2170", {"start": v(25.47, 64.63) * mm, "end": v(23.08, 64.17) * mm});
            skLineSegment(sketch, "E2171", {"start": v(23.08, 64.17) * mm, "end": v(21.28, 63.66) * mm});
            skLineSegment(sketch, "E2172", {"start": v(21.28, 63.66) * mm, "end": v(20, 63.15) * mm});
            skLineSegment(sketch, "E2173", {"start": v(20, 63.15) * mm, "end": v(19.18, 62.7) * mm});
            skLineSegment(sketch, "E2174", {"start": v(19.18, 62.7) * mm, "end": v(18.73, 62.4) * mm});
            skLineSegment(sketch, "E2175", {"start": v(18.73, 62.4) * mm, "end": v(18.6, 62.28) * mm});
            skLineSegment(sketch, "E2176", {"start": v(18.6, 62.28) * mm, "end": v(18.86, 62.6) * mm});
            skLineSegment(sketch, "E2177", {"start": v(18.86, 62.6) * mm, "end": v(19.63, 63.42) * mm});
            skLineSegment(sketch, "E2178", {"start": v(19.63, 63.42) * mm, "end": v(20.94, 64.54) * mm});
            skLineSegment(sketch, "E2179", {"start": v(20.94, 64.54) * mm, "end": v(22.78, 65.75) * mm});
            skLineSegment(sketch, "E2180", {"start": v(22.78, 65.75) * mm, "end": v(25.19, 66.85) * mm});
            skLineSegment(sketch, "E2181", {"start": v(25.19, 66.85) * mm, "end": v(28.15, 67.62) * mm});
            skLineSegment(sketch, "E2182", {"start": v(28.15, 67.62) * mm, "end": v(31.7, 67.86) * mm});
            skLineSegment(sketch, "E2183", {"start": v(31.7, 67.86) * mm, "end": v(35.83, 67.36) * mm});
            skLineSegment(sketch, "E2184", {"start": v(35.83, 67.36) * mm, "end": v(38.08, 66.85) * mm});
            skLineSegment(sketch, "E2185", {"start": v(38.08, 66.85) * mm, "end": v(40.04, 66.35) * mm});
            skLineSegment(sketch, "E2186", {"start": v(40.04, 66.35) * mm, "end": v(41.78, 65.9) * mm});
            skLineSegment(sketch, "E2187", {"start": v(41.78, 65.9) * mm, "end": v(43.38, 65.52) * mm});
            skLineSegment(sketch, "E2188", {"start": v(43.38, 65.52) * mm, "end": v(44.9, 65.27) * mm});
            skLineSegment(sketch, "E2189", {"start": v(44.9, 65.27) * mm, "end": v(46.44, 65.17) * mm});
            skLineSegment(sketch, "E2190", {"start": v(46.44, 65.17) * mm, "end": v(48.04, 65.25) * mm});
            skLineSegment(sketch, "E2191", {"start": v(48.04, 65.25) * mm, "end": v(49.79, 65.56) * mm});
            skLineSegment(sketch, "E2192", {"start": v(49.79, 65.56) * mm, "end": v(51.63, 66.1) * mm});
            skLineSegment(sketch, "E2193", {"start": v(51.63, 66.1) * mm, "end": v(53.4, 66.85) * mm});
            skLineSegment(sketch, "E2194", {"start": v(53.4, 66.85) * mm, "end": v(55.04, 67.72) * mm});
            skLineSegment(sketch, "E2195", {"start": v(55.04, 67.72) * mm, "end": v(56.45, 68.63) * mm});
            skLineSegment(sketch, "E2196", {"start": v(56.45, 68.63) * mm, "end": v(57.56, 69.54) * mm});
            skLineSegment(sketch, "E2197", {"start": v(57.56, 69.54) * mm, "end": v(58.3, 70.36) * mm});
            skLineSegment(sketch, "E2198", {"start": v(58.3, 70.36) * mm, "end": v(58.58, 71.02) * mm});
            skLineSegment(sketch, "E2199", {"start": v(58.58, 71.02) * mm, "end": v(58.32, 71.46) * mm});
            skLineSegment(sketch, "E2200", {"start": v(58.32, 71.46) * mm, "end": v(57.7, 71.73) * mm});
            skLineSegment(sketch, "E2201", {"start": v(57.7, 71.73) * mm, "end": v(56.98, 71.92) * mm});
            skLineSegment(sketch, "E2202", {"start": v(56.98, 71.92) * mm, "end": v(56.1, 72.02) * mm});
            skLineSegment(sketch, "E2203", {"start": v(56.1, 72.02) * mm, "end": v(55.08, 72.04) * mm});
            skLineSegment(sketch, "E2204", {"start": v(55.08, 72.04) * mm, "end": v(53.9, 71.98) * mm});
            skLineSegment(sketch, "E2205", {"start": v(53.9, 71.98) * mm, "end": v(52.51, 71.84) * mm});
            skLineSegment(sketch, "E2206", {"start": v(52.51, 71.84) * mm, "end": v(50.93, 71.6) * mm});
            skLineSegment(sketch, "E2207", {"start": v(50.93, 71.6) * mm, "end": v(49.13, 71.3) * mm});
            skLineSegment(sketch, "E2208", {"start": v(49.13, 71.3) * mm, "end": v(47.46, 71.1) * mm});
            skLineSegment(sketch, "E2209", {"start": v(47.46, 71.1) * mm, "end": v(45.27, 71) * mm});
            skLineSegment(sketch, "E2210", {"start": v(45.27, 71) * mm, "end": v(42.78, 70.96) * mm});
            skLineSegment(sketch, "E2211", {"start": v(42.78, 70.96) * mm, "end": v(40.24, 70.97) * mm});
            skLineSegment(sketch, "E2212", {"start": v(40.24, 70.97) * mm, "end": v(37.86, 71) * mm});
            skLineSegment(sketch, "E2213", {"start": v(37.86, 71) * mm, "end": v(35.87, 71.06) * mm});
            skLineSegment(sketch, "E2214", {"start": v(35.87, 71.06) * mm, "end": v(34.51, 71.1) * mm});
            skLineSegment(sketch, "E2215", {"start": v(34.51, 71.1) * mm, "end": v(34, 71.13) * mm});
            skLineSegment(sketch, "E2216", {"start": v(15.95, 41.9) * mm, "end": v(16.7, 41.92) * mm});
            skLineSegment(sketch, "E2217", {"start": v(16.7, 41.92) * mm, "end": v(18.68, 41.85) * mm});
            skLineSegment(sketch, "E2218", {"start": v(18.68, 41.85) * mm, "end": v(21.54, 41.52) * mm});
            skLineSegment(sketch, "E2219", {"start": v(21.54, 41.52) * mm, "end": v(24.9, 40.75) * mm});
            skLineSegment(sketch, "E2220", {"start": v(24.9, 40.75) * mm, "end": v(28.36, 39.36) * mm});
            skLineSegment(sketch, "E2221", {"start": v(28.36, 39.36) * mm, "end": v(31.58, 37.18) * mm});
            skLineSegment(sketch, "E2222", {"start": v(31.58, 37.18) * mm, "end": v(34.17, 34.02) * mm});
            skLineSegment(sketch, "E2223", {"start": v(34.17, 34.02) * mm, "end": v(35.76, 29.72) * mm});
            skLineSegment(sketch, "E2224", {"start": v(35.76, 29.72) * mm, "end": v(36.07, 29) * mm});
            skLineSegment(sketch, "E2225", {"start": v(36.07, 29) * mm, "end": v(36.9, 26.94) * mm});
            skLineSegment(sketch, "E2226", {"start": v(36.9, 26.94) * mm, "end": v(38.1, 23.7) * mm});
            skLineSegment(sketch, "E2227", {"start": v(38.1, 23.7) * mm, "end": v(39.5, 19.43) * mm});
            skLineSegment(sketch, "E2228", {"start": v(39.5, 19.43) * mm, "end": v(40.93, 14.28) * mm});
            skLineSegment(sketch, "E2229", {"start": v(40.93, 14.28) * mm, "end": v(42.23, 8.42) * mm});
            skLineSegment(sketch, "E2230", {"start": v(42.23, 8.42) * mm, "end": v(43.24, 2) * mm});
            skLineSegment(sketch, "E2231", {"start": v(43.24, 2) * mm, "end": v(43.8, -4.84) * mm});
            skLineSegment(sketch, "E2232", {"start": v(43.8, -4.84) * mm, "end": v(44.16, -4.98) * mm});
            skLineSegment(sketch, "E2233", {"start": v(44.16, -4.98) * mm, "end": v(45.14, -5.38) * mm});
            skLineSegment(sketch, "E2234", {"start": v(45.14, -5.38) * mm, "end": v(46.56, -6) * mm});
            skLineSegment(sketch, "E2235", {"start": v(46.56, -6) * mm, "end": v(48.25, -6.84) * mm});
            skLineSegment(sketch, "E2236", {"start": v(48.25, -6.84) * mm, "end": v(50.05, -7.85) * mm});
            skLineSegment(sketch, "E2237", {"start": v(50.05, -7.85) * mm, "end": v(51.78, -9.02) * mm});
            skLineSegment(sketch, "E2238", {"start": v(51.78, -9.02) * mm, "end": v(53.28, -10.31) * mm});
            skLineSegment(sketch, "E2239", {"start": v(53.28, -10.31) * mm, "end": v(54.38, -11.7) * mm});
            skLineSegment(sketch, "E2240", {"start": v(54.38, -11.7) * mm, "end": v(54.2, -11) * mm});
            skLineSegment(sketch, "E2241", {"start": v(54.2, -11) * mm, "end": v(53.7, -9.1) * mm});
            skLineSegment(sketch, "E2242", {"start": v(53.7, -9.1) * mm, "end": v(52.9, -6.33) * mm});
            skLineSegment(sketch, "E2243", {"start": v(52.9, -6.33) * mm, "end": v(51.8, -3) * mm});
            skLineSegment(sketch, "E2244", {"start": v(51.8, -3) * mm, "end": v(50.45, 0.54) * mm});
            skLineSegment(sketch, "E2245", {"start": v(50.45, 0.54) * mm, "end": v(48.85, 4) * mm});
            skLineSegment(sketch, "E2246", {"start": v(48.85, 4) * mm, "end": v(47.04, 7.03) * mm});
            skLineSegment(sketch, "E2247", {"start": v(47.04, 7.03) * mm, "end": v(45.03, 9.31) * mm});
            skLineSegment(sketch, "E2248", {"start": v(45.03, 9.31) * mm, "end": v(45.74, 9.5) * mm});
            skLineSegment(sketch, "E2249", {"start": v(45.74, 9.5) * mm, "end": v(47.7, 9.86) * mm});
            skLineSegment(sketch, "E2250", {"start": v(47.7, 9.86) * mm, "end": v(50.64, 10.15) * mm});
            skLineSegment(sketch, "E2251", {"start": v(50.64, 10.15) * mm, "end": v(54.33, 10.08) * mm});
            skLineSegment(sketch, "E2252", {"start": v(54.33, 10.08) * mm, "end": v(58.5, 9.4) * mm});
            skLineSegment(sketch, "E2253", {"start": v(58.5, 9.4) * mm, "end": v(62.92, 7.85) * mm});
            skLineSegment(sketch, "E2254", {"start": v(62.92, 7.85) * mm, "end": v(67.32, 5.14) * mm});
            skLineSegment(sketch, "E2255", {"start": v(67.32, 5.14) * mm, "end": v(71.44, 1.02) * mm});
            skLineSegment(sketch, "E2256", {"start": v(71.44, 1.02) * mm, "end": v(71.2, 1.95) * mm});
            skLineSegment(sketch, "E2257", {"start": v(71.2, 1.95) * mm, "end": v(70.46, 4.45) * mm});
            skLineSegment(sketch, "E2258", {"start": v(70.46, 4.45) * mm, "end": v(69.28, 8.08) * mm});
            skLineSegment(sketch, "E2259", {"start": v(69.28, 8.08) * mm, "end": v(67.68, 12.43) * mm});
            skLineSegment(sketch, "E2260", {"start": v(67.68, 12.43) * mm, "end": v(65.68, 17.07) * mm});
            skLineSegment(sketch, "E2261", {"start": v(65.68, 17.07) * mm, "end": v(63.3, 21.56) * mm});
            skLineSegment(sketch, "E2262", {"start": v(63.3, 21.56) * mm, "end": v(60.6, 25.48) * mm});
            skLineSegment(sketch, "E2263", {"start": v(60.6, 25.48) * mm, "end": v(57.56, 28.4) * mm});
            skLineSegment(sketch, "E2264", {"start": v(57.56, 28.4) * mm, "end": v(58.07, 28.35) * mm});
            skLineSegment(sketch, "E2265", {"start": v(58.07, 28.35) * mm, "end": v(59.45, 28.18) * mm});
            skLineSegment(sketch, "E2266", {"start": v(59.45, 28.18) * mm, "end": v(61.48, 27.87) * mm});
            skLineSegment(sketch, "E2267", {"start": v(61.48, 27.87) * mm, "end": v(63.95, 27.38) * mm});
            skLineSegment(sketch, "E2268", {"start": v(63.95, 27.38) * mm, "end": v(66.62, 26.67) * mm});
            skLineSegment(sketch, "E2269", {"start": v(66.62, 26.67) * mm, "end": v(69.27, 25.73) * mm});
            skLineSegment(sketch, "E2270", {"start": v(69.27, 25.73) * mm, "end": v(71.7, 24.5) * mm});
            skLineSegment(sketch, "E2271", {"start": v(71.7, 24.5) * mm, "end": v(73.66, 22.98) * mm});
            skLineSegment(sketch, "E2272", {"start": v(73.66, 22.98) * mm, "end": v(73.35, 23.91) * mm});
            skLineSegment(sketch, "E2273", {"start": v(73.35, 23.91) * mm, "end": v(72.33, 26.49) * mm});
            skLineSegment(sketch, "E2274", {"start": v(72.33, 26.49) * mm, "end": v(70.4, 30.39) * mm});
            skLineSegment(sketch, "E2275", {"start": v(70.4, 30.39) * mm, "end": v(67.43, 35.28) * mm});
            skLineSegment(sketch, "E2276", {"start": v(67.43, 35.28) * mm, "end": v(63.23, 40.84) * mm});
            skLineSegment(sketch, "E2277", {"start": v(63.23, 40.84) * mm, "end": v(57.63, 46.73) * mm});
            skLineSegment(sketch, "E2278", {"start": v(57.63, 46.73) * mm, "end": v(50.47, 52.63) * mm});
            skLineSegment(sketch, "E2279", {"start": v(50.47, 52.63) * mm, "end": v(41.57, 58.22) * mm});
            skLineSegment(sketch, "E2280", {"start": v(41.57, 58.22) * mm, "end": v(40.86, 58.57) * mm});
            skLineSegment(sketch, "E2281", {"start": v(40.86, 58.57) * mm, "end": v(38.93, 59.43) * mm});
            skLineSegment(sketch, "E2282", {"start": v(38.93, 59.43) * mm, "end": v(36, 60.49) * mm});
            skLineSegment(sketch, "E2283", {"start": v(36, 60.49) * mm, "end": v(32.33, 61.44) * mm});
            skLineSegment(sketch, "E2284", {"start": v(32.33, 61.44) * mm, "end": v(28.16, 62) * mm});
            skLineSegment(sketch, "E2285", {"start": v(28.16, 62) * mm, "end": v(23.75, 61.85) * mm});
            skLineSegment(sketch, "E2286", {"start": v(23.75, 61.85) * mm, "end": v(19.35, 60.69) * mm});
            skLineSegment(sketch, "E2287", {"start": v(19.35, 60.69) * mm, "end": v(15.19, 58.22) * mm});
            skLineSegment(sketch, "E2288", {"start": v(15.19, 58.22) * mm, "end": v(15.8, 58.47) * mm});
            skLineSegment(sketch, "E2289", {"start": v(15.8, 58.47) * mm, "end": v(17.52, 59.07) * mm});
            skLineSegment(sketch, "E2290", {"start": v(17.52, 59.07) * mm, "end": v(20.14, 59.76) * mm});
            skLineSegment(sketch, "E2291", {"start": v(20.14, 59.76) * mm, "end": v(23.45, 60.3) * mm});
            skLineSegment(sketch, "E2292", {"start": v(23.45, 60.3) * mm, "end": v(27.25, 60.43) * mm});
            skLineSegment(sketch, "E2293", {"start": v(27.25, 60.43) * mm, "end": v(31.35, 59.91) * mm});
            skLineSegment(sketch, "E2294", {"start": v(31.35, 59.91) * mm, "end": v(35.52, 58.5) * mm});
            skLineSegment(sketch, "E2295", {"start": v(35.52, 58.5) * mm, "end": v(39.58, 55.92) * mm});
            skLineSegment(sketch, "E2296", {"start": v(39.58, 55.92) * mm, "end": v(42.88, 52.97) * mm});
            skLineSegment(sketch, "E2297", {"start": v(42.88, 52.97) * mm, "end": v(45.03, 50.53) * mm});
            skLineSegment(sketch, "E2298", {"start": v(45.03, 50.53) * mm, "end": v(46.22, 48.55) * mm});
            skLineSegment(sketch, "E2299", {"start": v(46.22, 48.55) * mm, "end": v(46.64, 47.01) * mm});
            skLineSegment(sketch, "E2300", {"start": v(46.64, 47.01) * mm, "end": v(46.48, 45.85) * mm});
            skLineSegment(sketch, "E2301", {"start": v(46.48, 45.85) * mm, "end": v(45.93, 45.04) * mm});
            skLineSegment(sketch, "E2302", {"start": v(45.93, 45.04) * mm, "end": v(45.18, 44.53) * mm});
            skLineSegment(sketch, "E2303", {"start": v(45.18, 44.53) * mm, "end": v(44.42, 44.27) * mm});
            skLineSegment(sketch, "E2304", {"start": v(44.42, 44.27) * mm, "end": v(42.66, 44.51) * mm});
            skLineSegment(sketch, "E2305", {"start": v(42.66, 44.51) * mm, "end": v(39.1, 45.32) * mm});
            skLineSegment(sketch, "E2306", {"start": v(39.1, 45.32) * mm, "end": v(34.26, 46.42) * mm});
            skLineSegment(sketch, "E2307", {"start": v(34.26, 46.42) * mm, "end": v(28.63, 47.54) * mm});
            skLineSegment(sketch, "E2308", {"start": v(28.63, 47.54) * mm, "end": v(22.73, 48.4) * mm});
            skLineSegment(sketch, "E2309", {"start": v(22.73, 48.4) * mm, "end": v(17.07, 48.7) * mm});
            skLineSegment(sketch, "E2310", {"start": v(17.07, 48.7) * mm, "end": v(12.14, 48.2) * mm});
            skLineSegment(sketch, "E2311", {"start": v(12.14, 48.2) * mm, "end": v(8.46, 46.6) * mm});
            skLineSegment(sketch, "E2312", {"start": v(8.46, 46.6) * mm, "end": v(9.05, 46.72) * mm});
            skLineSegment(sketch, "E2313", {"start": v(9.05, 46.72) * mm, "end": v(10.69, 46.98) * mm});
            skLineSegment(sketch, "E2314", {"start": v(10.69, 46.98) * mm, "end": v(13.22, 47.23) * mm});
            skLineSegment(sketch, "E2315", {"start": v(13.22, 47.23) * mm, "end": v(16.46, 47.32) * mm});
            skLineSegment(sketch, "E2316", {"start": v(16.46, 47.32) * mm, "end": v(20.24, 47.1) * mm});
            skLineSegment(sketch, "E2317", {"start": v(20.24, 47.1) * mm, "end": v(24.4, 46.43) * mm});
            skLineSegment(sketch, "E2318", {"start": v(24.4, 46.43) * mm, "end": v(28.74, 45.16) * mm});
            skLineSegment(sketch, "E2319", {"start": v(28.74, 45.16) * mm, "end": v(33.12, 43.13) * mm});
            skLineSegment(sketch, "E2320", {"start": v(33.12, 43.13) * mm, "end": v(32.77, 43.25) * mm});
            skLineSegment(sketch, "E2321", {"start": v(32.77, 43.25) * mm, "end": v(31.76, 43.52) * mm});
            skLineSegment(sketch, "E2322", {"start": v(31.76, 43.52) * mm, "end": v(30.17, 43.84) * mm});
            skLineSegment(sketch, "E2323", {"start": v(30.17, 43.84) * mm, "end": v(28.07, 44.07) * mm});
            skLineSegment(sketch, "E2324", {"start": v(28.07, 44.07) * mm, "end": v(25.52, 44.12) * mm});
            skLineSegment(sketch, "E2325", {"start": v(25.52, 44.12) * mm, "end": v(22.6, 43.85) * mm});
            skLineSegment(sketch, "E2326", {"start": v(22.6, 43.85) * mm, "end": v(19.4, 43.15) * mm});
            skLineSegment(sketch, "E2327", {"start": v(19.4, 43.15) * mm, "end": v(15.95, 41.9) * mm});
            skLineSegment(sketch, "E2328", {"start": v(57.16, 70.98) * mm, "end": v(56.96, 70.78) * mm});
            skLineSegment(sketch, "E2329", {"start": v(56.96, 70.78) * mm, "end": v(56.37, 70.28) * mm});
            skLineSegment(sketch, "E2330", {"start": v(56.37, 70.28) * mm, "end": v(55.43, 69.55) * mm});
            skLineSegment(sketch, "E2331", {"start": v(55.43, 69.55) * mm, "end": v(54.18, 68.72) * mm});
            skLineSegment(sketch, "E2332", {"start": v(54.18, 68.72) * mm, "end": v(52.63, 67.89) * mm});
            skLineSegment(sketch, "E2333", {"start": v(52.63, 67.89) * mm, "end": v(50.84, 67.14) * mm});
            skLineSegment(sketch, "E2334", {"start": v(50.84, 67.14) * mm, "end": v(48.82, 66.6) * mm});
            skLineSegment(sketch, "E2335", {"start": v(48.82, 66.6) * mm, "end": v(46.6, 66.37) * mm});
            skLineSegment(sketch, "E2336", {"start": v(46.6, 66.37) * mm, "end": v(44, 66.62) * mm});
            skLineSegment(sketch, "E2337", {"start": v(44, 66.62) * mm, "end": v(40.84, 67.28) * mm});
            skLineSegment(sketch, "E2338", {"start": v(40.84, 67.28) * mm, "end": v(37.2, 68.07) * mm});
            skLineSegment(sketch, "E2339", {"start": v(37.2, 68.07) * mm, "end": v(33.2, 68.7) * mm});
            skLineSegment(sketch, "E2340", {"start": v(33.2, 68.7) * mm, "end": v(28.9, 68.88) * mm});
            skLineSegment(sketch, "E2341", {"start": v(28.9, 68.88) * mm, "end": v(24.39, 68.31) * mm});
            skLineSegment(sketch, "E2342", {"start": v(24.39, 68.31) * mm, "end": v(19.77, 66.73) * mm});
            skLineSegment(sketch, "E2343", {"start": v(19.77, 66.73) * mm, "end": v(15.12, 63.82) * mm});
            skLineSegment(sketch, "E2344", {"start": v(15.12, 63.82) * mm, "end": v(15.18, 64.03) * mm});
            skLineSegment(sketch, "E2345", {"start": v(15.18, 64.03) * mm, "end": v(15.37, 64.59) * mm});
            skLineSegment(sketch, "E2346", {"start": v(15.37, 64.59) * mm, "end": v(15.7, 65.4) * mm});
            skLineSegment(sketch, "E2347", {"start": v(15.7, 65.4) * mm, "end": v(16.16, 66.38) * mm});
            skLineSegment(sketch, "E2348", {"start": v(16.16, 66.38) * mm, "end": v(16.77, 67.41) * mm});
            skLineSegment(sketch, "E2349", {"start": v(16.77, 67.41) * mm, "end": v(17.54, 68.42) * mm});
            skLineSegment(sketch, "E2350", {"start": v(17.54, 68.42) * mm, "end": v(18.47, 69.3) * mm});
            skLineSegment(sketch, "E2351", {"start": v(18.47, 69.3) * mm, "end": v(19.58, 69.94) * mm});
            skLineSegment(sketch, "E2352", {"start": v(19.58, 69.94) * mm, "end": v(19.1, 69.94) * mm});
            skLineSegment(sketch, "E2353", {"start": v(19.1, 69.94) * mm, "end": v(17.81, 69.92) * mm});
            skLineSegment(sketch, "E2354", {"start": v(17.81, 69.92) * mm, "end": v(15.94, 69.84) * mm});
            skLineSegment(sketch, "E2355", {"start": v(15.94, 69.84) * mm, "end": v(13.69, 69.67) * mm});
            skLineSegment(sketch, "E2356", {"start": v(13.69, 69.67) * mm, "end": v(11.28, 69.38) * mm});
            skLineSegment(sketch, "E2357", {"start": v(11.28, 69.38) * mm, "end": v(8.93, 68.93) * mm});
            skLineSegment(sketch, "E2358", {"start": v(8.93, 68.93) * mm, "end": v(6.86, 68.28) * mm});
            skLineSegment(sketch, "E2359", {"start": v(6.86, 68.28) * mm, "end": v(5.28, 67.4) * mm});
            skLineSegment(sketch, "E2360", {"start": v(5.28, 67.4) * mm, "end": v(5.15, 67.48) * mm});
            skLineSegment(sketch, "E2361", {"start": v(5.15, 67.48) * mm, "end": v(4.77, 67.7) * mm});
            skLineSegment(sketch, "E2362", {"start": v(4.77, 67.7) * mm, "end": v(4.24, 68.04) * mm});
            skLineSegment(sketch, "E2363", {"start": v(4.24, 68.04) * mm, "end": v(3.63, 68.48) * mm});
            skLineSegment(sketch, "E2364", {"start": v(3.63, 68.48) * mm, "end": v(3, 69.02) * mm});
            skLineSegment(sketch, "E2365", {"start": v(3, 69.02) * mm, "end": v(2.42, 69.62) * mm});
            skLineSegment(sketch, "E2366", {"start": v(2.42, 69.62) * mm, "end": v(1.97, 70.28) * mm});
            skLineSegment(sketch, "E2367", {"start": v(1.97, 70.28) * mm, "end": v(1.73, 70.98) * mm});
            skLineSegment(sketch, "E2368", {"start": v(1.73, 70.98) * mm, "end": v(2.53, 71.59) * mm});
            skLineSegment(sketch, "E2369", {"start": v(2.53, 71.59) * mm, "end": v(4.97, 72) * mm});
            skLineSegment(sketch, "E2370", {"start": v(4.97, 72) * mm, "end": v(8.67, 72.18) * mm});
            skLineSegment(sketch, "E2371", {"start": v(8.67, 72.18) * mm, "end": v(13.3, 72.14) * mm});
            skLineSegment(sketch, "E2372", {"start": v(13.3, 72.14) * mm, "end": v(18.5, 71.86) * mm});
            skLineSegment(sketch, "E2373", {"start": v(18.5, 71.86) * mm, "end": v(23.91, 71.32) * mm});
            skLineSegment(sketch, "E2374", {"start": v(23.91, 71.32) * mm, "end": v(29.2, 70.51) * mm});
            skLineSegment(sketch, "E2375", {"start": v(29.2, 70.51) * mm, "end": v(34, 69.43) * mm});
            skLineSegment(sketch, "E2376", {"start": v(34, 69.43) * mm, "end": v(36.42, 68.91) * mm});
            skLineSegment(sketch, "E2377", {"start": v(36.42, 68.91) * mm, "end": v(39.44, 68.51) * mm});
            skLineSegment(sketch, "E2378", {"start": v(39.44, 68.51) * mm, "end": v(42.84, 68.27) * mm});
            skLineSegment(sketch, "E2379", {"start": v(42.84, 68.27) * mm, "end": v(46.38, 68.23) * mm});
            skLineSegment(sketch, "E2380", {"start": v(46.38, 68.23) * mm, "end": v(49.82, 68.43) * mm});
            skLineSegment(sketch, "E2381", {"start": v(49.82, 68.43) * mm, "end": v(52.92, 68.93) * mm});
            skLineSegment(sketch, "E2382", {"start": v(52.92, 68.93) * mm, "end": v(55.45, 69.77) * mm});
            skLineSegment(sketch, "E2383", {"start": v(55.45, 69.77) * mm, "end": v(57.16, 70.98) * mm});
            skLineSegment(sketch, "E2384", {"start": v(-16.23, 37.17) * mm, "end": v(-17.68, 37.42) * mm});
            skLineSegment(sketch, "E2385", {"start": v(-17.68, 37.42) * mm, "end": v(-21.6, 38.1) * mm});
            skLineSegment(sketch, "E2386", {"start": v(-21.6, 38.1) * mm, "end": v(-27.3, 39.05) * mm});
            skLineSegment(sketch, "E2387", {"start": v(-27.3, 39.05) * mm, "end": v(-34.17, 40.14) * mm});
            skLineSegment(sketch, "E2388", {"start": v(-34.17, 40.14) * mm, "end": v(-41.52, 41.23) * mm});
            skLineSegment(sketch, "E2389", {"start": v(-41.52, 41.23) * mm, "end": v(-48.7, 42.18) * mm});
            skLineSegment(sketch, "E2390", {"start": v(-48.7, 42.18) * mm, "end": v(-55.07, 42.85) * mm});
            skLineSegment(sketch, "E2391", {"start": v(-55.07, 42.85) * mm, "end": v(-59.95, 43.1) * mm});
            skLineSegment(sketch, "E2392", {"start": v(-59.95, 43.1) * mm, "end": v(-58.32, 42.85) * mm});
            skLineSegment(sketch, "E2393", {"start": v(-58.32, 42.85) * mm, "end": v(-53.97, 42.2) * mm});
            skLineSegment(sketch, "E2394", {"start": v(-53.97, 42.2) * mm, "end": v(-47.72, 41.27) * mm});
            skLineSegment(sketch, "E2395", {"start": v(-47.72, 41.27) * mm, "end": v(-40.37, 40.2) * mm});
            skLineSegment(sketch, "E2396", {"start": v(-40.37, 40.2) * mm, "end": v(-32.74, 39.14) * mm});
            skLineSegment(sketch, "E2397", {"start": v(-32.74, 39.14) * mm, "end": v(-25.63, 38.18) * mm});
            skLineSegment(sketch, "E2398", {"start": v(-25.63, 38.18) * mm, "end": v(-19.86, 37.48) * mm});
            skLineSegment(sketch, "E2399", {"start": v(-19.86, 37.48) * mm, "end": v(-16.23, 37.17) * mm});
            skLineSegment(sketch, "E2400", {"start": v(-18.02, 35.71) * mm, "end": v(-19.52, 35.74) * mm});
            skLineSegment(sketch, "E2401", {"start": v(-19.52, 35.74) * mm, "end": v(-23.56, 35.83) * mm});
            skLineSegment(sketch, "E2402", {"start": v(-23.56, 35.83) * mm, "end": v(-29.46, 36) * mm});
            skLineSegment(sketch, "E2403", {"start": v(-29.46, 36) * mm, "end": v(-36.52, 36.24) * mm});
            skLineSegment(sketch, "E2404", {"start": v(-36.52, 36.24) * mm, "end": v(-44.07, 36.6) * mm});
            skLineSegment(sketch, "E2405", {"start": v(-44.07, 36.6) * mm, "end": v(-51.4, 37.06) * mm});
            skLineSegment(sketch, "E2406", {"start": v(-51.4, 37.06) * mm, "end": v(-57.85, 37.65) * mm});
            skLineSegment(sketch, "E2407", {"start": v(-57.85, 37.65) * mm, "end": v(-62.7, 38.37) * mm});
            skLineSegment(sketch, "E2408", {"start": v(-62.7, 38.37) * mm, "end": v(-61.03, 38.3) * mm});
            skLineSegment(sketch, "E2409", {"start": v(-61.03, 38.3) * mm, "end": v(-56.57, 38.1) * mm});
            skLineSegment(sketch, "E2410", {"start": v(-56.57, 38.1) * mm, "end": v(-50.15, 37.8) * mm});
            skLineSegment(sketch, "E2411", {"start": v(-50.15, 37.8) * mm, "end": v(-42.61, 37.43) * mm});
            skLineSegment(sketch, "E2412", {"start": v(-42.61, 37.43) * mm, "end": v(-34.8, 37) * mm});
            skLineSegment(sketch, "E2413", {"start": v(-34.8, 37) * mm, "end": v(-27.53, 36.56) * mm});
            skLineSegment(sketch, "E2414", {"start": v(-27.53, 36.56) * mm, "end": v(-21.66, 36.12) * mm});
            skLineSegment(sketch, "E2415", {"start": v(-21.66, 36.12) * mm, "end": v(-18.02, 35.71) * mm});
            skLineSegment(sketch, "E2416", {"start": v(-20.6, 33.87) * mm, "end": v(-22.16, 33.77) * mm});
            skLineSegment(sketch, "E2417", {"start": v(-22.16, 33.77) * mm, "end": v(-26.36, 33.53) * mm});
            skLineSegment(sketch, "E2418", {"start": v(-26.36, 33.53) * mm, "end": v(-32.48, 33.2) * mm});
            skLineSegment(sketch, "E2419", {"start": v(-32.48, 33.2) * mm, "end": v(-39.8, 32.86) * mm});
            skLineSegment(sketch, "E2420", {"start": v(-39.8, 32.86) * mm, "end": v(-47.62, 32.59) * mm});
            skLineSegment(sketch, "E2421", {"start": v(-47.62, 32.59) * mm, "end": v(-55.2, 32.44) * mm});
            skLineSegment(sketch, "E2422", {"start": v(-55.2, 32.44) * mm, "end": v(-61.84, 32.5) * mm});
            skLineSegment(sketch, "E2423", {"start": v(-61.84, 32.5) * mm, "end": v(-66.8, 32.82) * mm});
            skLineSegment(sketch, "E2424", {"start": v(-66.8, 32.82) * mm, "end": v(-65.07, 32.88) * mm});
            skLineSegment(sketch, "E2425", {"start": v(-65.07, 32.88) * mm, "end": v(-60.44, 33.05) * mm});
            skLineSegment(sketch, "E2426", {"start": v(-60.44, 33.05) * mm, "end": v(-53.78, 33.29) * mm});
            skLineSegment(sketch, "E2427", {"start": v(-53.78, 33.29) * mm, "end": v(-45.97, 33.54) * mm});
            skLineSegment(sketch, "E2428", {"start": v(-45.97, 33.54) * mm, "end": v(-37.88, 33.77) * mm});
            skLineSegment(sketch, "E2429", {"start": v(-37.88, 33.77) * mm, "end": v(-30.38, 33.93) * mm});
            skLineSegment(sketch, "E2430", {"start": v(-30.38, 33.93) * mm, "end": v(-24.33, 33.98) * mm});
            skLineSegment(sketch, "E2431", {"start": v(-24.33, 33.98) * mm, "end": v(-20.6, 33.87) * mm});
            skLineSegment(sketch, "E2432", {"start": v(16.13, 37.16) * mm, "end": v(17.58, 37.41) * mm});
            skLineSegment(sketch, "E2433", {"start": v(17.58, 37.41) * mm, "end": v(21.5, 38.09) * mm});
            skLineSegment(sketch, "E2434", {"start": v(21.5, 38.09) * mm, "end": v(27.21, 39.04) * mm});
            skLineSegment(sketch, "E2435", {"start": v(27.21, 39.04) * mm, "end": v(34.07, 40.13) * mm});
            skLineSegment(sketch, "E2436", {"start": v(34.07, 40.13) * mm, "end": v(41.42, 41.22) * mm});
            skLineSegment(sketch, "E2437", {"start": v(41.42, 41.22) * mm, "end": v(48.6, 42.17) * mm});
            skLineSegment(sketch, "E2438", {"start": v(48.6, 42.17) * mm, "end": v(54.97, 42.83) * mm});
            skLineSegment(sketch, "E2439", {"start": v(54.97, 42.83) * mm, "end": v(59.85, 43.08) * mm});
            skLineSegment(sketch, "E2440", {"start": v(59.85, 43.08) * mm, "end": v(58.22, 42.84) * mm});
            skLineSegment(sketch, "E2441", {"start": v(58.22, 42.84) * mm, "end": v(53.87, 42.19) * mm});
            skLineSegment(sketch, "E2442", {"start": v(53.87, 42.19) * mm, "end": v(47.62, 41.26) * mm});
            skLineSegment(sketch, "E2443", {"start": v(47.62, 41.26) * mm, "end": v(40.27, 40.2) * mm});
            skLineSegment(sketch, "E2444", {"start": v(40.27, 40.2) * mm, "end": v(32.64, 39.12) * mm});
            skLineSegment(sketch, "E2445", {"start": v(32.64, 39.12) * mm, "end": v(25.53, 38.17) * mm});
            skLineSegment(sketch, "E2446", {"start": v(25.53, 38.17) * mm, "end": v(19.76, 37.47) * mm});
            skLineSegment(sketch, "E2447", {"start": v(19.76, 37.47) * mm, "end": v(16.13, 37.16) * mm});
            skLineSegment(sketch, "E2448", {"start": v(17.92, 35.7) * mm, "end": v(19.42, 35.73) * mm});
            skLineSegment(sketch, "E2449", {"start": v(19.42, 35.73) * mm, "end": v(23.46, 35.82) * mm});
            skLineSegment(sketch, "E2450", {"start": v(23.46, 35.82) * mm, "end": v(29.36, 35.98) * mm});
            skLineSegment(sketch, "E2451", {"start": v(29.36, 35.98) * mm, "end": v(36.42, 36.23) * mm});
            skLineSegment(sketch, "E2452", {"start": v(36.42, 36.23) * mm, "end": v(43.97, 36.59) * mm});
            skLineSegment(sketch, "E2453", {"start": v(43.97, 36.59) * mm, "end": v(51.3, 37.05) * mm});
            skLineSegment(sketch, "E2454", {"start": v(51.3, 37.05) * mm, "end": v(57.75, 37.64) * mm});
            skLineSegment(sketch, "E2455", {"start": v(57.75, 37.64) * mm, "end": v(62.6, 38.36) * mm});
            skLineSegment(sketch, "E2456", {"start": v(62.6, 38.36) * mm, "end": v(60.94, 38.3) * mm});
            skLineSegment(sketch, "E2457", {"start": v(60.94, 38.3) * mm, "end": v(56.47, 38.1) * mm});
            skLineSegment(sketch, "E2458", {"start": v(56.47, 38.1) * mm, "end": v(50.05, 37.8) * mm});
            skLineSegment(sketch, "E2459", {"start": v(50.05, 37.8) * mm, "end": v(42.52, 37.42) * mm});
            skLineSegment(sketch, "E2460", {"start": v(42.52, 37.42) * mm, "end": v(34.7, 37) * mm});
            skLineSegment(sketch, "E2461", {"start": v(34.7, 37) * mm, "end": v(27.43, 36.55) * mm});
            skLineSegment(sketch, "E2462", {"start": v(27.43, 36.55) * mm, "end": v(21.56, 36.1) * mm});
            skLineSegment(sketch, "E2463", {"start": v(21.56, 36.1) * mm, "end": v(17.92, 35.7) * mm});
            skLineSegment(sketch, "E2464", {"start": v(20.5, 33.86) * mm, "end": v(22.06, 33.76) * mm});
            skLineSegment(sketch, "E2465", {"start": v(22.06, 33.76) * mm, "end": v(26.26, 33.52) * mm});
            skLineSegment(sketch, "E2466", {"start": v(26.26, 33.52) * mm, "end": v(32.38, 33.19) * mm});
            skLineSegment(sketch, "E2467", {"start": v(32.38, 33.19) * mm, "end": v(39.71, 32.85) * mm});
            skLineSegment(sketch, "E2468", {"start": v(39.71, 32.85) * mm, "end": v(47.53, 32.57) * mm});
            skLineSegment(sketch, "E2469", {"start": v(47.53, 32.57) * mm, "end": v(55.1, 32.43) * mm});
            skLineSegment(sketch, "E2470", {"start": v(55.1, 32.43) * mm, "end": v(61.74, 32.48) * mm});
            skLineSegment(sketch, "E2471", {"start": v(61.74, 32.48) * mm, "end": v(66.7, 32.8) * mm});
            skLineSegment(sketch, "E2472", {"start": v(66.7, 32.8) * mm, "end": v(64.97, 32.87) * mm});
            skLineSegment(sketch, "E2473", {"start": v(64.97, 32.87) * mm, "end": v(60.34, 33.04) * mm});
            skLineSegment(sketch, "E2474", {"start": v(60.34, 33.04) * mm, "end": v(53.68, 33.28) * mm});
            skLineSegment(sketch, "E2475", {"start": v(53.68, 33.28) * mm, "end": v(45.88, 33.53) * mm});
            skLineSegment(sketch, "E2476", {"start": v(45.88, 33.53) * mm, "end": v(37.79, 33.76) * mm});
            skLineSegment(sketch, "E2477", {"start": v(37.79, 33.76) * mm, "end": v(30.28, 33.92) * mm});
            skLineSegment(sketch, "E2478", {"start": v(30.28, 33.92) * mm, "end": v(24.23, 33.97) * mm});
            skLineSegment(sketch, "E2479", {"start": v(24.23, 33.97) * mm, "end": v(20.5, 33.86) * mm});
            skLineSegment(sketch, "E2480", {"start": v(-17.2, 17.72) * mm, "end": v(-17.14, 17.7) * mm});
            skLineSegment(sketch, "E2481", {"start": v(-17.14, 17.7) * mm, "end": v(-16.95, 17.64) * mm});
            skLineSegment(sketch, "E2482", {"start": v(-16.95, 17.64) * mm, "end": v(-16.68, 17.53) * mm});
            skLineSegment(sketch, "E2483", {"start": v(-16.68, 17.53) * mm, "end": v(-16.34, 17.37) * mm});
            skLineSegment(sketch, "E2484", {"start": v(-16.34, 17.37) * mm, "end": v(-15.98, 17.17) * mm});
            skLineSegment(sketch, "E2485", {"start": v(-15.98, 17.17) * mm, "end": v(-15.62, 16.92) * mm});
            skLineSegment(sketch, "E2486", {"start": v(-15.62, 16.92) * mm, "end": v(-15.29, 16.63) * mm});
            skLineSegment(sketch, "E2487", {"start": v(-15.29, 16.63) * mm, "end": v(-15.02, 16.28) * mm});
            skLineSegment(sketch, "E2488", {"start": v(-15.02, 16.28) * mm, "end": v(-15.13, 15.16) * mm});
            skLineSegment(sketch, "E2489", {"start": v(-15.13, 15.16) * mm, "end": v(-15.42, 11.73) * mm});
            skLineSegment(sketch, "E2490", {"start": v(-15.42, 11.73) * mm, "end": v(-15.78, 5.9) * mm});
            skLineSegment(sketch, "E2491", {"start": v(-15.78, 5.9) * mm, "end": v(-16.13, -2.45) * mm});
            skLineSegment(sketch, "E2492", {"start": v(-16.13, -2.45) * mm, "end": v(-16.37, -13.42) * mm});
            skLineSegment(sketch, "E2493", {"start": v(-16.37, -13.42) * mm, "end": v(-16.42, -27.1) * mm});
            skLineSegment(sketch, "E2494", {"start": v(-16.42, -27.1) * mm, "end": v(-16.19, -43.58) * mm});
            skLineSegment(sketch, "E2495", {"start": v(-16.19, -43.58) * mm, "end": v(-15.57, -63) * mm});
            skLineSegment(sketch, "E2496", {"start": v(-15.57, -63) * mm, "end": v(-15.73, -62.04) * mm});
            skLineSegment(sketch, "E2497", {"start": v(-15.73, -62.04) * mm, "end": v(-16.12, -58.99) * mm});
            skLineSegment(sketch, "E2498", {"start": v(-16.12, -58.99) * mm, "end": v(-16.64, -53.58) * mm});
            skLineSegment(sketch, "E2499", {"start": v(-16.64, -53.58) * mm, "end": v(-17.18, -45.57) * mm});
            skLineSegment(sketch, "E2500", {"start": v(-17.18, -45.57) * mm, "end": v(-17.61, -34.7) * mm});
            skLineSegment(sketch, "E2501", {"start": v(-17.61, -34.7) * mm, "end": v(-17.84, -20.7) * mm});
            skLineSegment(sketch, "E2502", {"start": v(-17.84, -20.7) * mm, "end": v(-17.74, -3.3) * mm});
            skLineSegment(sketch, "E2503", {"start": v(-17.74, -3.3) * mm, "end": v(-17.2, 17.72) * mm});
            skLineSegment(sketch, "E2504", {"start": v(24.24, 17.94) * mm, "end": v(24.43, 15.33) * mm});
            skLineSegment(sketch, "E2505", {"start": v(24.43, 15.33) * mm, "end": v(24.8, 8.2) * mm});
            skLineSegment(sketch, "E2506", {"start": v(24.8, 8.2) * mm, "end": v(25.05, -2.39) * mm});
            skLineSegment(sketch, "E2507", {"start": v(25.05, -2.39) * mm, "end": v(24.9, -15.4) * mm});
            skLineSegment(sketch, "E2508", {"start": v(24.9, -15.4) * mm, "end": v(24.03, -29.77) * mm});
            skLineSegment(sketch, "E2509", {"start": v(24.03, -29.77) * mm, "end": v(22.17, -44.45) * mm});
            skLineSegment(sketch, "E2510", {"start": v(22.17, -44.45) * mm, "end": v(19.02, -58.4) * mm});
            skLineSegment(sketch, "E2511", {"start": v(19.02, -58.4) * mm, "end": v(14.27, -70.55) * mm});
            skLineSegment(sketch, "E2512", {"start": v(14.27, -70.55) * mm, "end": v(14.37, -67.96) * mm});
            skLineSegment(sketch, "E2513", {"start": v(14.37, -67.96) * mm, "end": v(14.61, -60.91) * mm});
            skLineSegment(sketch, "E2514", {"start": v(14.61, -60.91) * mm, "end": v(14.89, -50.45) * mm});
            skLineSegment(sketch, "E2515", {"start": v(14.89, -50.45) * mm, "end": v(15.1, -37.6) * mm});
            skLineSegment(sketch, "E2516", {"start": v(15.1, -37.6) * mm, "end": v(15.15, -23.45) * mm});
            skLineSegment(sketch, "E2517", {"start": v(15.15, -23.45) * mm, "end": v(14.95, -9) * mm});
            skLineSegment(sketch, "E2518", {"start": v(14.95, -9) * mm, "end": v(14.38, 4.65) * mm});
            skLineSegment(sketch, "E2519", {"start": v(14.38, 4.65) * mm, "end": v(13.36, 16.5) * mm});
            skLineSegment(sketch, "E2520", {"start": v(13.36, 16.5) * mm, "end": v(13.4, 16.6) * mm});
            skLineSegment(sketch, "E2521", {"start": v(13.4, 16.6) * mm, "end": v(13.54, 16.85) * mm});
            skLineSegment(sketch, "E2522", {"start": v(13.54, 16.85) * mm, "end": v(13.82, 17.22) * mm});
            skLineSegment(sketch, "E2523", {"start": v(13.82, 17.22) * mm, "end": v(14.27, 17.67) * mm});
            skLineSegment(sketch, "E2524", {"start": v(14.27, 17.67) * mm, "end": v(14.93, 18.14) * mm});
            skLineSegment(sketch, "E2525", {"start": v(14.93, 18.14) * mm, "end": v(15.82, 18.6) * mm});
            skLineSegment(sketch, "E2526", {"start": v(15.82, 18.6) * mm, "end": v(17, 19) * mm});
            skLineSegment(sketch, "E2527", {"start": v(17, 19) * mm, "end": v(18.48, 19.3) * mm});
            skLineSegment(sketch, "E2528", {"start": v(18.48, 19.3) * mm, "end": v(20, 19.43) * mm});
            skLineSegment(sketch, "E2529", {"start": v(20, 19.43) * mm, "end": v(21.23, 19.39) * mm});
            skLineSegment(sketch, "E2530", {"start": v(21.23, 19.39) * mm, "end": v(22.23, 19.21) * mm});
            skLineSegment(sketch, "E2531", {"start": v(22.23, 19.21) * mm, "end": v(23, 18.95) * mm});
            skLineSegment(sketch, "E2532", {"start": v(23, 18.95) * mm, "end": v(23.57, 18.65) * mm});
            skLineSegment(sketch, "E2533", {"start": v(23.57, 18.65) * mm, "end": v(23.95, 18.35) * mm});
            skLineSegment(sketch, "E2534", {"start": v(23.95, 18.35) * mm, "end": v(24.17, 18.1) * mm});
            skLineSegment(sketch, "E2535", {"start": v(24.17, 18.1) * mm, "end": v(24.24, 17.94) * mm});
            skLineSegment(sketch, "E2536", {"start": v(17.11, 17.72) * mm, "end": v(17.04, 17.7) * mm});
            skLineSegment(sketch, "E2537", {"start": v(17.04, 17.7) * mm, "end": v(16.86, 17.64) * mm});
            skLineSegment(sketch, "E2538", {"start": v(16.86, 17.64) * mm, "end": v(16.58, 17.53) * mm});
            skLineSegment(sketch, "E2539", {"start": v(16.58, 17.53) * mm, "end": v(16.25, 17.37) * mm});
            skLineSegment(sketch, "E2540", {"start": v(16.25, 17.37) * mm, "end": v(15.88, 17.17) * mm});
            skLineSegment(sketch, "E2541", {"start": v(15.88, 17.17) * mm, "end": v(15.52, 16.92) * mm});
            skLineSegment(sketch, "E2542", {"start": v(15.52, 16.92) * mm, "end": v(15.2, 16.63) * mm});
            skLineSegment(sketch, "E2543", {"start": v(15.2, 16.63) * mm, "end": v(14.92, 16.28) * mm});
            skLineSegment(sketch, "E2544", {"start": v(14.92, 16.28) * mm, "end": v(15.04, 15.16) * mm});
            skLineSegment(sketch, "E2545", {"start": v(15.04, 15.16) * mm, "end": v(15.32, 11.73) * mm});
            skLineSegment(sketch, "E2546", {"start": v(15.32, 11.73) * mm, "end": v(15.68, 5.9) * mm});
            skLineSegment(sketch, "E2547", {"start": v(15.68, 5.9) * mm, "end": v(16.03, -2.45) * mm});
            skLineSegment(sketch, "E2548", {"start": v(16.03, -2.45) * mm, "end": v(16.28, -13.42) * mm});
            skLineSegment(sketch, "E2549", {"start": v(16.28, -13.42) * mm, "end": v(16.33, -27.1) * mm});
            skLineSegment(sketch, "E2550", {"start": v(16.33, -27.1) * mm, "end": v(16.09, -43.58) * mm});
            skLineSegment(sketch, "E2551", {"start": v(16.09, -43.58) * mm, "end": v(15.48, -63) * mm});
            skLineSegment(sketch, "E2552", {"start": v(15.48, -63) * mm, "end": v(15.63, -62.04) * mm});
            skLineSegment(sketch, "E2553", {"start": v(15.63, -62.04) * mm, "end": v(16.03, -58.99) * mm});
            skLineSegment(sketch, "E2554", {"start": v(16.03, -58.99) * mm, "end": v(16.55, -53.58) * mm});
            skLineSegment(sketch, "E2555", {"start": v(16.55, -53.58) * mm, "end": v(17.08, -45.57) * mm});
            skLineSegment(sketch, "E2556", {"start": v(17.08, -45.57) * mm, "end": v(17.52, -34.7) * mm});
            skLineSegment(sketch, "E2557", {"start": v(17.52, -34.7) * mm, "end": v(17.74, -20.7) * mm});
            skLineSegment(sketch, "E2558", {"start": v(17.74, -20.7) * mm, "end": v(17.64, -3.3) * mm});
            skLineSegment(sketch, "E2559", {"start": v(17.64, -3.3) * mm, "end": v(17.11, 17.72) * mm});
            skSolve(sketch);
        }
        {
            var Q0;
            Q0=makeQuery(id+"F0.imprint","IMPRINT",FACE,{"disambiguationData":[TD([[makeQuery(id+"F0.imprint","IMPRINT",EDGE,{"derivedFrom":sQuery(id+"F0.wireOp",EDGE,"E1968")}),1.0]])]});
            var Q1;
            Q1=makeQuery(id+"F0.imprint","IMPRINT",FACE,{"disambiguationData":[TD([[makeQuery(id+"F0.imprint","IMPRINT",EDGE,{"derivedFrom":sQuery(id+"F0.wireOp",EDGE,"E2328")}),-1.0]])]});
            var Q2;
            Q2=makeQuery(id+"F0.imprint","IMPRINT",FACE,{"disambiguationData":[TD([[makeQuery(id+"F0.imprint","IMPRINT",EDGE,{"derivedFrom":sQuery(id+"F0.wireOp",EDGE,"E2216")}),1.0]])]});
            var Q3;
            Q3=makeQuery(id+"F0.imprint","IMPRINT",FACE,{"disambiguationData":[TD([[makeQuery(id+"F0.imprint","IMPRINT",EDGE,{"derivedFrom":sQuery(id+"F0.wireOp",EDGE,"E1856")}),-1.0]])]});
            var Q4;
            Q4=makeQuery(id+"F0.imprint","IMPRINT",FACE,{"disambiguationData":[TD([[makeQuery(id+"F0.imprint","IMPRINT",EDGE,{"derivedFrom":sQuery(id+"F0.wireOp",EDGE,"E1296")}),1.0]])]});
            var Q5;
            Q5=makeQuery(id+"F0.imprint","IMPRINT",FACE,{"disambiguationData":[TD([[makeQuery(id+"F0.imprint","IMPRINT",EDGE,{"derivedFrom":sQuery(id+"F0.wireOp",EDGE,"E1416")}),-1.0]])]});
            var Q6;
            Q6=makeQuery(id+"F0.imprint","IMPRINT",FACE,{"disambiguationData":[TD([[makeQuery(id+"F0.imprint","IMPRINT",EDGE,{"derivedFrom":sQuery(id+"F0.wireOp",EDGE,"E1088")}),1.0]])]});
            var Q7;
            {var subQ48=sQuery(id+"F0.wireOp",EDGE,"E13");Q7=makeQuery(id+"F0.imprint","IMPRINT",FACE,{"disambiguationData":[TD([[makeQuery(id+"F0.imprint","IMPRINT",EDGE,{"derivedFrom":subQ48}),1.0]])]});}
            var Q8;
            {var subQ7=sQuery(id+"F0.wireOp",EDGE,"E140");Q8=makeQuery(id+"F0.imprint","IMPRINT",FACE,{"disambiguationData":[TD([[makeQuery(id+"F0.imprint","IMPRINT",EDGE,{"derivedFrom":subQ7}),1.0]])]});}
            extrude(context, id + "F1", {"entities" : qUnion([Q0, Q1, Q2, Q3, Q4, Q5, Q6, Q7, Q8]), "depth" : 3.8 * mm, "offsetDistance" : 25.4 * mm});
        }
        {
            var Q0;
            Q0=makeQuery(id+"F0.imprint","IMPRINT",FACE,{"disambiguationData":[TD([[makeQuery(id+"F0.imprint","IMPRINT",EDGE,{"derivedFrom":sQuery(id+"F0.wireOp",EDGE,"E1584")}),1.0]])]});
            var Q1;
            Q1=makeQuery(id+"F0.imprint","IMPRINT",FACE,{"disambiguationData":[TD([[makeQuery(id+"F0.imprint","IMPRINT",EDGE,{"derivedFrom":sQuery(id+"F0.wireOp",EDGE,"E2136")}),-1.0]])]});
            var Q2;
            Q2=makeQuery(id+"F0.imprint","IMPRINT",FACE,{"disambiguationData":[TD([[makeQuery(id+"F0.imprint","IMPRINT",EDGE,{"derivedFrom":sQuery(id+"F0.wireOp",EDGE,"E1664")}),1.0]])]});
            var Q3;
            Q3=makeQuery(id+"F0.imprint","IMPRINT",FACE,{"disambiguationData":[TD([[makeQuery(id+"F0.imprint","IMPRINT",EDGE,{"derivedFrom":sQuery(id+"F0.wireOp",EDGE,"E1232")}),-1.0]])]});
            var Q4;
            Q4=makeQuery(id+"F0.imprint","IMPRINT",FACE,{"disambiguationData":[TD([[makeQuery(id+"F0.imprint","IMPRINT",EDGE,{"derivedFrom":sQuery(id+"F0.wireOp",EDGE,"E1352")}),1.0]])]});
            var Q5;
            {var subQ39=sQuery(id+"F0.wireOp",EDGE,"E33");Q5=makeQuery(id+"F0.imprint","IMPRINT",FACE,{"disambiguationData":[TD([[makeQuery(id+"F0.imprint","IMPRINT",EDGE,{"derivedFrom":subQ39}),1.0]])]});}
            var Q6;
            Q6=makeQuery(id+"F0.imprint","IMPRINT",FACE,{"disambiguationData":[TD([[makeQuery(id+"F0.imprint","IMPRINT",EDGE,{"derivedFrom":sQuery(id+"F0.wireOp",EDGE,"E1472")}),1.0]])]});
            var Q7;
            Q7=makeQuery(id+"F0.imprint","IMPRINT",FACE,{"disambiguationData":[TD([[makeQuery(id+"F0.imprint","IMPRINT",EDGE,{"derivedFrom":sQuery(id+"F0.wireOp",EDGE,"E2024")}),-1.0]])]});
            var Q8;
            Q8=makeQuery(id+"F0.imprint","IMPRINT",FACE,{"disambiguationData":[TD([[makeQuery(id+"F0.imprint","IMPRINT",EDGE,{"derivedFrom":sQuery(id+"F0.wireOp",EDGE,"E1696")}),-1.0]])]});
            var Q9;
            Q9=makeQuery(id+"F0.imprint","IMPRINT",FACE,{"disambiguationData":[TD([[makeQuery(id+"F0.imprint","IMPRINT",EDGE,{"derivedFrom":sQuery(id+"F0.wireOp",EDGE,"E160")}),-1.0]])]});
            var Q10;
            Q10=makeQuery(id+"F0.imprint","IMPRINT",FACE,{"disambiguationData":[TD([[makeQuery(id+"F0.imprint","IMPRINT",EDGE,{"derivedFrom":sQuery(id+"F0.wireOp",EDGE,"E0")}),-1.0]])]});
            var Q11;
            {var subQ0=sQuery(id+"F0.wireOp",EDGE,"E2552");Q11=makeQuery(id+"F0.imprint","IMPRINT",FACE,{"disambiguationData":[TD([[makeQuery(id+"F0.imprint","IMPRINT",EDGE,{"derivedFrom":subQ0}),1.0]])]});}
            var Q12;
            {var subQ16=sQuery(id+"F0.wireOp",EDGE,"E517");Q12=makeQuery(id+"F0.imprint","IMPRINT",FACE,{"disambiguationData":[TD([[makeQuery(id+"F0.imprint","IMPRINT",EDGE,{"derivedFrom":subQ16}),-1.0]])]});}
            var Q13;
            {var subQ1=sQuery(id+"F0.wireOp",EDGE,"E265");Q13=makeQuery(id+"F0.imprint","IMPRINT",FACE,{"disambiguationData":[TD([[makeQuery(id+"F0.imprint","IMPRINT",EDGE,{"derivedFrom":subQ1}),1.0]])]});}
            var Q14;
            {var subQ6=sQuery(id+"F0.wireOp",EDGE,"E554");Q14=makeQuery(id+"F0.imprint","IMPRINT",FACE,{"disambiguationData":[TD([[makeQuery(id+"F0.imprint","IMPRINT",EDGE,{"derivedFrom":subQ6}),-1.0]])]});}
            var Q15;
            {var subQ5=sQuery(id+"F0.wireOp",EDGE,"E517");Q15=makeQuery(id+"F0.imprint","IMPRINT",FACE,{"disambiguationData":[TD([[makeQuery(id+"F0.imprint","IMPRINT",EDGE,{"derivedFrom":subQ5}),1.0]])]});}
            var Q16;
            {var subQ8=sQuery(id+"F0.wireOp",EDGE,"E268");Q16=makeQuery(id+"F0.imprint","IMPRINT",FACE,{"disambiguationData":[TD([[makeQuery(id+"F0.imprint","IMPRINT",EDGE,{"derivedFrom":subQ8}),1.0]])]});}
            var Q17;
            {var subQ4=sQuery(id+"F0.wireOp",EDGE,"E544");Q17=makeQuery(id+"F0.imprint","IMPRINT",FACE,{"disambiguationData":[TD([[makeQuery(id+"F0.imprint","IMPRINT",EDGE,{"derivedFrom":subQ4}),-1.0]])]});}
            var Q18;
            {var subQ4=sQuery(id+"F0.wireOp",EDGE,"E522");Q18=makeQuery(id+"F0.imprint","IMPRINT",FACE,{"disambiguationData":[TD([[makeQuery(id+"F0.imprint","IMPRINT",EDGE,{"derivedFrom":subQ4}),-1.0]])]});}
            var Q19;
            {var subQ5=sQuery(id+"F0.wireOp",EDGE,"E159");var subQ6=sQuery(id+"F0.wireOp",EDGE,"E136");var subQ7=makeQuery(id+"F0.imprint","INTERSECT",VERTEX,{"derivedFrom":[subQ6,subQ5]});Q19=makeQuery(id+"F0.imprint","IMPRINT",FACE,{"disambiguationData":[TD([[makeQuery(id+"F0.imprint","IMPRINT",EDGE,{"disambiguationData":[TD([[subQ7,-1.0]])],"derivedFrom":subQ6}),-1.0]])]});}
            var Q20;
            {var subQ5=sQuery(id+"F0.wireOp",EDGE,"E265");Q20=makeQuery(id+"F0.imprint","IMPRINT",FACE,{"disambiguationData":[TD([[makeQuery(id+"F0.imprint","IMPRINT",EDGE,{"derivedFrom":subQ5}),-1.0]])]});}
            var Q21;
            {var subQ10=sQuery(id+"F0.wireOp",EDGE,"E268");Q21=makeQuery(id+"F0.imprint","IMPRINT",FACE,{"disambiguationData":[TD([[makeQuery(id+"F0.imprint","IMPRINT",EDGE,{"derivedFrom":subQ10}),-1.0]])]});}
            extrude(context, id + "F2", {"entities" : qUnion([Q0, Q1, Q2, Q3, Q4, Q5, Q6, Q7, Q8, Q9, Q10, Q11, Q12, Q13, Q14, Q15, Q16, Q17, Q18, Q19, Q20, Q21]), "depth" : 3.8 * mm, "offsetDistance" : 25.4 * mm});
        }
        {
            var Q0;
            Q0=qCreatedBy(makeId("Top.planeOp"),FACE);
            var sketch = newSketch(context, id + "F3", { "sketchPlane" : qUnion([Q0])});
            skFitSpline(sketch, "E2560", {"points": [v(0, -5.7) * mm, v(-1.01, -0.13) * mm, v(-1.54, 3.96) * mm, v(-1.92, 6.07) * mm, v(-2.17, 6.72) * mm, v(-2.44, 7.45) * mm, v(-2.82, 8.27) * mm, v(-3.36, 9.18) * mm, v(-4.46, 10.34) * mm, v(-6.23, 11.54) * mm, v(-8.32, 12.2) * mm, v(-10.36, 11.8) * mm, v(-10.72, 9.34) * mm, v(-10.4, 4.33) * mm, v(-10.24, -1.43) * mm, v(-11.12, -6.14) * mm, v(-12.7, -10.69) * mm, v(-13.79, -16.27) * mm, v(-13.83, -21.55) * mm, v(-12.31, -25.18) * mm, v(-10.15, -27.35) * mm, v(-8.5, -29.21) * mm, v(-7.18, -30.87) * mm, v(-6.03, -32.42) * mm, v(-4.58, -33.47) * mm, v(-2.8, -33.79) * mm, v(-1.22, -33.72) * mm, v(-0.36, -33.7) * mm], "startDerivative": vector(-14.56, 90.93) * mm, "endDerivative": vector(37.23, -0.28) * mm});
            skFitSpline(sketch, "E2561.MirrorCS", {"points": [v(0, -5.7) * mm, v(1.16, -0.16) * mm, v(1.79, 3.91) * mm, v(2.23, 6.02) * mm, v(2.48, 6.66) * mm, v(2.78, 7.38) * mm, v(3.18, 8.19) * mm, v(3.74, 9.09) * mm, v(4.87, 10.22) * mm, v(6.67, 11.37) * mm, v(8.77, 12) * mm, v(10.8, 11.53) * mm, v(11.1, 9.06) * mm, v(10.65, 4.06) * mm, v(10.34, -1.7) * mm, v(11.1, -6.42) * mm, v(12.58, -11.01) * mm, v(13.51, -16.62) * mm, v(13.42, -21.9) * mm, v(11.8, -25.49) * mm, v(9.6, -27.6) * mm, v(7.9, -29.42) * mm, v(6.54, -31.04) * mm, v(5.35, -32.56) * mm, v(3.87, -33.58) * mm, v(2.08, -33.85) * mm, v(0.5, -33.74) * mm, v(-0.36, -33.7) * mm], "startDerivative": vector(16.89, 90.53) * mm, "endDerivative": vector(-37.23, 0.67) * mm});
            skSolve(sketch);
        }
        {
            var Q0;
            Q0 = qSketchRegion(id + "F3", true);
            extrude(context, id + "F4", {"entities" : qUnion([Q0]), "depth" : 3.8 * mm, "offsetDistance" : 25.4 * mm});
        }
        {
            var Q0;
            Q0=makeQuery(id+"F4.opExtrude","SWEPT_BODY",BODY,{"disambiguationData":[OSD([sQuery(id+"F3.wireOp",EDGE,"E2560"),sQuery(id+"F3.wireOp",EDGE,"E2561.MirrorCS")])]});
            var Q1;
            Q1=makeQuery(id+"F1.opExtrude","SWEPT_BODY",BODY,{"disambiguationData":[OSD([sQuery(id+"F0.wireOp",EDGE,"E12"),sQuery(id+"F0.wireOp",EDGE,"E13"),sQuery(id+"F0.wireOp",EDGE,"E14"),sQuery(id+"F0.wireOp",EDGE,"E15"),sQuery(id+"F0.wireOp",EDGE,"E16"),sQuery(id+"F0.wireOp",EDGE,"E17"),sQuery(id+"F0.wireOp",EDGE,"E18"),sQuery(id+"F0.wireOp",EDGE,"E19"),sQuery(id+"F0.wireOp",EDGE,"E20"),sQuery(id+"F0.wireOp",EDGE,"E21"),sQuery(id+"F0.wireOp",EDGE,"E22"),sQuery(id+"F0.wireOp",EDGE,"E23"),sQuery(id+"F0.wireOp",EDGE,"E24"),sQuery(id+"F0.wireOp",EDGE,"E25"),sQuery(id+"F0.wireOp",EDGE,"E26"),sQuery(id+"F0.wireOp",EDGE,"E27"),sQuery(id+"F0.wireOp",EDGE,"E28"),sQuery(id+"F0.wireOp",EDGE,"E29"),sQuery(id+"F0.wireOp",EDGE,"E30"),sQuery(id+"F0.wireOp",EDGE,"E31"),sQuery(id+"F0.wireOp",EDGE,"E32"),sQuery(id+"F0.wireOp",EDGE,"E223"),sQuery(id+"F0.wireOp",EDGE,"E224"),sQuery(id+"F0.wireOp",EDGE,"E225"),sQuery(id+"F0.wireOp",EDGE,"E226"),sQuery(id+"F0.wireOp",EDGE,"E227"),sQuery(id+"F0.wireOp",EDGE,"E228"),sQuery(id+"F0.wireOp",EDGE,"E229"),sQuery(id+"F0.wireOp",EDGE,"E230"),sQuery(id+"F0.wireOp",EDGE,"E231"),sQuery(id+"F0.wireOp",EDGE,"E232"),sQuery(id+"F0.wireOp",EDGE,"E233"),sQuery(id+"F0.wireOp",EDGE,"E234"),sQuery(id+"F0.wireOp",EDGE,"E235"),sQuery(id+"F0.wireOp",EDGE,"E513"),sQuery(id+"F0.wireOp",EDGE,"E514"),sQuery(id+"F0.wireOp",EDGE,"E530"),sQuery(id+"F0.wireOp",EDGE,"E531"),sQuery(id+"F0.wireOp",EDGE,"E532"),sQuery(id+"F0.wireOp",EDGE,"E533"),sQuery(id+"F0.wireOp",EDGE,"E535"),sQuery(id+"F0.wireOp",EDGE,"E536"),sQuery(id+"F0.wireOp",EDGE,"E538"),sQuery(id+"F0.wireOp",EDGE,"E540"),sQuery(id+"F0.wireOp",EDGE,"E541"),sQuery(id+"F0.wireOp",EDGE,"E542"),sQuery(id+"F0.wireOp",EDGE,"E557"),sQuery(id+"F0.wireOp",EDGE,"E558"),sQuery(id+"F0.wireOp",EDGE,"E613"),sQuery(id+"F0.wireOp",EDGE,"E614"),sQuery(id+"F0.wireOp",EDGE,"E615"),sQuery(id+"F0.wireOp",EDGE,"E616"),sQuery(id+"F0.wireOp",EDGE,"E617"),sQuery(id+"F0.wireOp",EDGE,"E618"),sQuery(id+"F0.wireOp",EDGE,"E619"),sQuery(id+"F0.wireOp",EDGE,"E620"),sQuery(id+"F0.wireOp",EDGE,"E621"),sQuery(id+"F0.wireOp",EDGE,"E622"),sQuery(id+"F0.wireOp",EDGE,"E647"),sQuery(id+"F0.wireOp",EDGE,"E648"),sQuery(id+"F0.wireOp",EDGE,"E649"),sQuery(id+"F0.wireOp",EDGE,"E650"),sQuery(id+"F0.wireOp",EDGE,"E651"),sQuery(id+"F0.wireOp",EDGE,"E652"),sQuery(id+"F0.wireOp",EDGE,"E653"),sQuery(id+"F0.wireOp",EDGE,"E654"),sQuery(id+"F0.wireOp",EDGE,"E655"),sQuery(id+"F0.wireOp",EDGE,"E656"),sQuery(id+"F0.wireOp",EDGE,"E657"),sQuery(id+"F0.wireOp",EDGE,"E658"),sQuery(id+"F0.wireOp",EDGE,"E659"),sQuery(id+"F0.wireOp",EDGE,"E660"),sQuery(id+"F0.wireOp",EDGE,"E661"),sQuery(id+"F0.wireOp",EDGE,"E662"),sQuery(id+"F0.wireOp",EDGE,"E663"),sQuery(id+"F0.wireOp",EDGE,"E679"),sQuery(id+"F0.wireOp",EDGE,"E680"),sQuery(id+"F0.wireOp",EDGE,"E681"),sQuery(id+"F0.wireOp",EDGE,"E682"),sQuery(id+"F0.wireOp",EDGE,"E683"),sQuery(id+"F0.wireOp",EDGE,"E684"),sQuery(id+"F0.wireOp",EDGE,"E685"),sQuery(id+"F0.wireOp",EDGE,"E686"),sQuery(id+"F0.wireOp",EDGE,"E687"),sQuery(id+"F0.wireOp",EDGE,"E688"),sQuery(id+"F0.wireOp",EDGE,"E689"),sQuery(id+"F0.wireOp",EDGE,"E690"),sQuery(id+"F0.wireOp",EDGE,"E691"),sQuery(id+"F0.wireOp",EDGE,"E692"),sQuery(id+"F0.wireOp",EDGE,"E693"),sQuery(id+"F0.wireOp",EDGE,"E694"),sQuery(id+"F0.wireOp",EDGE,"E695"),sQuery(id+"F0.wireOp",EDGE,"E696"),sQuery(id+"F0.wireOp",EDGE,"E709"),sQuery(id+"F0.wireOp",EDGE,"E710"),sQuery(id+"F0.wireOp",EDGE,"E711"),sQuery(id+"F0.wireOp",EDGE,"E712"),sQuery(id+"F0.wireOp",EDGE,"E713"),sQuery(id+"F0.wireOp",EDGE,"E714"),sQuery(id+"F0.wireOp",EDGE,"E715"),sQuery(id+"F0.wireOp",EDGE,"E716"),sQuery(id+"F0.wireOp",EDGE,"E717"),sQuery(id+"F0.wireOp",EDGE,"E718"),sQuery(id+"F0.wireOp",EDGE,"E743"),sQuery(id+"F0.wireOp",EDGE,"E744"),sQuery(id+"F0.wireOp",EDGE,"E745"),sQuery(id+"F0.wireOp",EDGE,"E746"),sQuery(id+"F0.wireOp",EDGE,"E747"),sQuery(id+"F0.wireOp",EDGE,"E748"),sQuery(id+"F0.wireOp",EDGE,"E749"),sQuery(id+"F0.wireOp",EDGE,"E750"),sQuery(id+"F0.wireOp",EDGE,"E751"),sQuery(id+"F0.wireOp",EDGE,"E752"),sQuery(id+"F0.wireOp",EDGE,"E753"),sQuery(id+"F0.wireOp",EDGE,"E754"),sQuery(id+"F0.wireOp",EDGE,"E755"),sQuery(id+"F0.wireOp",EDGE,"E756"),sQuery(id+"F0.wireOp",EDGE,"E757"),sQuery(id+"F0.wireOp",EDGE,"E758"),sQuery(id+"F0.wireOp",EDGE,"E759"),sQuery(id+"F0.wireOp",EDGE,"E775"),sQuery(id+"F0.wireOp",EDGE,"E776"),sQuery(id+"F0.wireOp",EDGE,"E777"),sQuery(id+"F0.wireOp",EDGE,"E778"),sQuery(id+"F0.wireOp",EDGE,"E779"),sQuery(id+"F0.wireOp",EDGE,"E780"),sQuery(id+"F0.wireOp",EDGE,"E781"),sQuery(id+"F0.wireOp",EDGE,"E782"),sQuery(id+"F0.wireOp",EDGE,"E783"),sQuery(id+"F0.wireOp",EDGE,"E784"),sQuery(id+"F0.wireOp",EDGE,"E785"),sQuery(id+"F0.wireOp",EDGE,"E786"),sQuery(id+"F0.wireOp",EDGE,"E787"),sQuery(id+"F0.wireOp",EDGE,"E788"),sQuery(id+"F0.wireOp",EDGE,"E789"),sQuery(id+"F0.wireOp",EDGE,"E790"),sQuery(id+"F0.wireOp",EDGE,"E791"),sQuery(id+"F0.wireOp",EDGE,"E792"),sQuery(id+"F0.wireOp",EDGE,"E810"),sQuery(id+"F0.wireOp",EDGE,"E811"),sQuery(id+"F0.wireOp",EDGE,"E812"),sQuery(id+"F0.wireOp",EDGE,"E813"),sQuery(id+"F0.wireOp",EDGE,"E814"),sQuery(id+"F0.wireOp",EDGE,"E815"),sQuery(id+"F0.wireOp",EDGE,"E816"),sQuery(id+"F0.wireOp",EDGE,"E817"),sQuery(id+"F0.wireOp",EDGE,"E818"),sQuery(id+"F0.wireOp",EDGE,"E819"),sQuery(id+"F0.wireOp",EDGE,"E820"),sQuery(id+"F0.wireOp",EDGE,"E821"),sQuery(id+"F0.wireOp",EDGE,"E822"),sQuery(id+"F0.wireOp",EDGE,"E823"),sQuery(id+"F0.wireOp",EDGE,"E832"),sQuery(id+"F0.wireOp",EDGE,"E833"),sQuery(id+"F0.wireOp",EDGE,"E834"),sQuery(id+"F0.wireOp",EDGE,"E835"),sQuery(id+"F0.wireOp",EDGE,"E836"),sQuery(id+"F0.wireOp",EDGE,"E859"),sQuery(id+"F0.wireOp",EDGE,"E860"),sQuery(id+"F0.wireOp",EDGE,"E861"),sQuery(id+"F0.wireOp",EDGE,"E862"),sQuery(id+"F0.wireOp",EDGE,"E863"),sQuery(id+"F0.wireOp",EDGE,"E864"),sQuery(id+"F0.wireOp",EDGE,"E865"),sQuery(id+"F0.wireOp",EDGE,"E866"),sQuery(id+"F0.wireOp",EDGE,"E867"),sQuery(id+"F0.wireOp",EDGE,"E868"),sQuery(id+"F0.wireOp",EDGE,"E869"),sQuery(id+"F0.wireOp",EDGE,"E900"),sQuery(id+"F0.wireOp",EDGE,"E901"),sQuery(id+"F0.wireOp",EDGE,"E902"),sQuery(id+"F0.wireOp",EDGE,"E903"),sQuery(id+"F0.wireOp",EDGE,"E904"),sQuery(id+"F0.wireOp",EDGE,"E905"),sQuery(id+"F0.wireOp",EDGE,"E906"),sQuery(id+"F0.wireOp",EDGE,"E907"),sQuery(id+"F0.wireOp",EDGE,"E908"),sQuery(id+"F0.wireOp",EDGE,"E909"),sQuery(id+"F0.wireOp",EDGE,"E939"),sQuery(id+"F0.wireOp",EDGE,"E940"),sQuery(id+"F0.wireOp",EDGE,"E941"),sQuery(id+"F0.wireOp",EDGE,"E942"),sQuery(id+"F0.wireOp",EDGE,"E943"),sQuery(id+"F0.wireOp",EDGE,"E954"),sQuery(id+"F0.wireOp",EDGE,"E955"),sQuery(id+"F0.wireOp",EDGE,"E956"),sQuery(id+"F0.wireOp",EDGE,"E957"),sQuery(id+"F0.wireOp",EDGE,"E958"),sQuery(id+"F0.wireOp",EDGE,"E959"),sQuery(id+"F0.wireOp",EDGE,"E960"),sQuery(id+"F0.wireOp",EDGE,"E961"),sQuery(id+"F0.wireOp",EDGE,"E962"),sQuery(id+"F0.wireOp",EDGE,"E963"),sQuery(id+"F0.wireOp",EDGE,"E964"),sQuery(id+"F0.wireOp",EDGE,"E965"),sQuery(id+"F0.wireOp",EDGE,"E966"),sQuery(id+"F0.wireOp",EDGE,"E967"),sQuery(id+"F0.wireOp",EDGE,"E976"),sQuery(id+"F0.wireOp",EDGE,"E977"),sQuery(id+"F0.wireOp",EDGE,"E978"),sQuery(id+"F0.wireOp",EDGE,"E979"),sQuery(id+"F0.wireOp",EDGE,"E980"),sQuery(id+"F0.wireOp",EDGE,"E1003"),sQuery(id+"F0.wireOp",EDGE,"E1004"),sQuery(id+"F0.wireOp",EDGE,"E1005"),sQuery(id+"F0.wireOp",EDGE,"E1006"),sQuery(id+"F0.wireOp",EDGE,"E1007"),sQuery(id+"F0.wireOp",EDGE,"E1008"),sQuery(id+"F0.wireOp",EDGE,"E1009"),sQuery(id+"F0.wireOp",EDGE,"E1010"),sQuery(id+"F0.wireOp",EDGE,"E1011"),sQuery(id+"F0.wireOp",EDGE,"E1012"),sQuery(id+"F0.wireOp",EDGE,"E1013"),sQuery(id+"F0.wireOp",EDGE,"E1044"),sQuery(id+"F0.wireOp",EDGE,"E1045"),sQuery(id+"F0.wireOp",EDGE,"E1046"),sQuery(id+"F0.wireOp",EDGE,"E1047"),sQuery(id+"F0.wireOp",EDGE,"E1048"),sQuery(id+"F0.wireOp",EDGE,"E1049"),sQuery(id+"F0.wireOp",EDGE,"E1050"),sQuery(id+"F0.wireOp",EDGE,"E1051"),sQuery(id+"F0.wireOp",EDGE,"E1052"),sQuery(id+"F0.wireOp",EDGE,"E1053"),sQuery(id+"F0.wireOp",EDGE,"E1083"),sQuery(id+"F0.wireOp",EDGE,"E1084"),sQuery(id+"F0.wireOp",EDGE,"E1085"),sQuery(id+"F0.wireOp",EDGE,"E1086"),sQuery(id+"F0.wireOp",EDGE,"E1087")])]});
            booleanBodies(context, id + "F5", {"operationType" : BooleanOperationType.SUBTRACTION, "tools" : qUnion([Q0]), "targets" : qUnion([Q1]), "keepTools" : true});
        }
        {
            var Q0;
            Q0=qCreatedBy(makeId("Top.planeOp"),FACE);
            var sketch = newSketch(context, id + "F6", { "sketchPlane" : qUnion([Q0])});
            skLineSegment(sketch, "E2562", {"start": v(8.84, 57.66) * mm, "end": v(6.5, 57.06) * mm});
            skLineSegment(sketch, "E2563", {"start": v(6.5, 57.06) * mm, "end": v(3.65, 56.02) * mm});
            skLineSegment(sketch, "E2564", {"start": v(3.65, 56.02) * mm, "end": v(3.97, 56.77) * mm});
            skLineSegment(sketch, "E2565", {"start": v(3.97, 56.77) * mm, "end": v(5.14, 58.67) * mm});
            skLineSegment(sketch, "E2566", {"start": v(5.14, 58.67) * mm, "end": v(7.48, 61.2) * mm});
            skLineSegment(sketch, "E2567", {"start": v(7.48, 61.2) * mm, "end": v(11.3, 63.82) * mm});
            skLineSegment(sketch, "E2568", {"start": v(11.3, 63.82) * mm, "end": v(10.54, 63.67) * mm});
            skLineSegment(sketch, "E2569", {"start": v(10.54, 63.67) * mm, "end": v(8.59, 63.12) * mm});
            skLineSegment(sketch, "E2570", {"start": v(8.59, 63.12) * mm, "end": v(6.02, 62.04) * mm});
            skLineSegment(sketch, "E2571", {"start": v(6.02, 62.04) * mm, "end": v(3.38, 60.27) * mm});
            skLineSegment(sketch, "E2572", {"start": v(3.38, 60.27) * mm, "end": v(2.78, 61.08) * mm});
            skLineSegment(sketch, "E2573", {"start": v(2.78, 61.08) * mm, "end": v(1.46, 63.07) * mm});
            skLineSegment(sketch, "E2574", {"start": v(1.46, 63.07) * mm, "end": v(0.15, 65.6) * mm});
            skLineSegment(sketch, "E2575", {"start": v(0.15, 65.6) * mm, "end": v(-0.43, 68.02) * mm});
            skLineSegment(sketch, "E2576", {"start": v(-0.43, 68.02) * mm, "end": v(-1, 65.6) * mm});
            skLineSegment(sketch, "E2577", {"start": v(-1, 65.6) * mm, "end": v(-2.31, 63.07) * mm});
            skLineSegment(sketch, "E2578", {"start": v(-2.31, 63.07) * mm, "end": v(-3.63, 61.08) * mm});
            skLineSegment(sketch, "E2579", {"start": v(-3.63, 61.08) * mm, "end": v(-4.23, 60.27) * mm});
            skLineSegment(sketch, "E2580", {"start": v(-4.23, 60.27) * mm, "end": v(-6.87, 62.04) * mm});
            skLineSegment(sketch, "E2581", {"start": v(-6.87, 62.04) * mm, "end": v(-9.44, 63.12) * mm});
            skLineSegment(sketch, "E2582", {"start": v(-9.44, 63.12) * mm, "end": v(-11.39, 63.67) * mm});
            skLineSegment(sketch, "E2583", {"start": v(-11.39, 63.67) * mm, "end": v(-12.16, 63.82) * mm});
            skLineSegment(sketch, "E2584", {"start": v(-12.16, 63.82) * mm, "end": v(-8.33, 61.2) * mm});
            skLineSegment(sketch, "E2585", {"start": v(-8.33, 61.2) * mm, "end": v(-5.99, 58.67) * mm});
            skLineSegment(sketch, "E2586", {"start": v(-5.99, 58.67) * mm, "end": v(-4.82, 56.77) * mm});
            skLineSegment(sketch, "E2587", {"start": v(-4.82, 56.77) * mm, "end": v(-4.5, 56.02) * mm});
            skLineSegment(sketch, "E2588", {"start": v(-4.5, 56.02) * mm, "end": v(-7.35, 57.06) * mm});
            skLineSegment(sketch, "E2589", {"start": v(-7.35, 57.06) * mm, "end": v(-9.69, 57.66) * mm});
            skLineSegment(sketch, "E2590", {"start": v(-9.69, 57.66) * mm, "end": v(-11.27, 57.94) * mm});
            skLineSegment(sketch, "E2591", {"start": v(-11.27, 57.94) * mm, "end": v(-11.85, 58.01) * mm});
            skLineSegment(sketch, "E2592", {"start": v(-11.85, 58.01) * mm, "end": v(-5.64, 54.28) * mm});
            skLineSegment(sketch, "E2593", {"start": v(-5.64, 54.28) * mm, "end": v(-2.2, 50.78) * mm});
            skLineSegment(sketch, "E2594", {"start": v(-2.2, 50.78) * mm, "end": v(-0.73, 48.17) * mm});
            skLineSegment(sketch, "E2595", {"start": v(-0.73, 48.17) * mm, "end": v(-0.43, 47.15) * mm});
            skLineSegment(sketch, "E2596", {"start": v(-0.43, 47.15) * mm, "end": v(-0.12, 48.17) * mm});
            skLineSegment(sketch, "E2597", {"start": v(-0.12, 48.17) * mm, "end": v(1.35, 50.78) * mm});
            skLineSegment(sketch, "E2598", {"start": v(1.35, 50.78) * mm, "end": v(4.79, 54.28) * mm});
            skLineSegment(sketch, "E2599", {"start": v(4.79, 54.28) * mm, "end": v(11, 58.01) * mm});
            skLineSegment(sketch, "E2600", {"start": v(11, 58.01) * mm, "end": v(10.42, 57.94) * mm});
            skLineSegment(sketch, "E2601", {"start": v(10.42, 57.94) * mm, "end": v(8.84, 57.66) * mm});
            skSolve(sketch);
        }
        {
            var Q0;
            Q0=makeQuery(id+"F6.imprint","IMPRINT",FACE,{"disambiguationData":[TD([[makeQuery(id+"F6.imprint","IMPRINT",EDGE,{"derivedFrom":sQuery(id+"F6.wireOp",EDGE,"E2562")}),1.0]])]});
            var Q1;
            Q1=sQuery(id+"F6.wireOp",EDGE,"E2587");
            var Q2;
            Q2=sQuery(id+"F6.wireOp",EDGE,"E2573");
            var Q3;
            Q3=sQuery(id+"F6.wireOp",EDGE,"E2584");
            var Q4;
            Q4=sQuery(id+"F6.wireOp",EDGE,"E2562");
            var Q5;
            Q5=sQuery(id+"F6.wireOp",EDGE,"E2567");
            var Q6;
            Q6=sQuery(id+"F6.wireOp",EDGE,"E2569");
            var Q7;
            Q7=sQuery(id+"F6.wireOp",EDGE,"E2571");
            var Q8;
            Q8=sQuery(id+"F6.wireOp",EDGE,"E2570");
            var Q9;
            Q9=sQuery(id+"F6.wireOp",EDGE,"E2598");
            var Q10;
            Q10=sQuery(id+"F6.wireOp",EDGE,"E2597");
            var Q11;
            Q11=sQuery(id+"F6.wireOp",EDGE,"E2582");
            var Q12;
            Q12=sQuery(id+"F6.wireOp",EDGE,"E2588");
            var Q13;
            Q13=sQuery(id+"F6.wireOp",EDGE,"E2594");
            var Q14;
            Q14=sQuery(id+"F6.wireOp",EDGE,"E2595");
            var Q15;
            Q15=sQuery(id+"F6.wireOp",EDGE,"E2564");
            var Q16;
            Q16=sQuery(id+"F6.wireOp",EDGE,"E2599");
            var Q17;
            Q17=sQuery(id+"F6.wireOp",EDGE,"E2568");
            var Q18;
            Q18=sQuery(id+"F6.wireOp",EDGE,"E2566");
            var Q19;
            Q19=sQuery(id+"F6.wireOp",EDGE,"E2563");
            var Q20;
            Q20=sQuery(id+"F6.wireOp",EDGE,"E2565");
            var Q21;
            Q21=sQuery(id+"F6.wireOp",EDGE,"E2593");
            var Q22;
            Q22=sQuery(id+"F6.wireOp",EDGE,"E2572");
            var Q23;
            Q23=sQuery(id+"F6.wireOp",EDGE,"E2596");
            var Q24;
            Q24=sQuery(id+"F6.wireOp",EDGE,"E2592");
            var Q25;
            Q25=sQuery(id+"F6.wireOp",EDGE,"E2583");
            var Q26;
            Q26=sQuery(id+"F6.wireOp",EDGE,"E2577");
            var Q27;
            Q27=sQuery(id+"F6.wireOp",EDGE,"E2576");
            var Q28;
            Q28=sQuery(id+"F6.wireOp",EDGE,"E2589");
            var Q29;
            Q29=sQuery(id+"F6.wireOp",EDGE,"E2591");
            var Q30;
            Q30=sQuery(id+"F6.wireOp",EDGE,"E2581");
            var Q31;
            Q31=sQuery(id+"F6.wireOp",EDGE,"E2585");
            var Q32;
            Q32=sQuery(id+"F6.wireOp",EDGE,"E2590");
            var Q33;
            Q33=sQuery(id+"F6.wireOp",EDGE,"E2586");
            var Q34;
            Q34=sQuery(id+"F6.wireOp",EDGE,"E2574");
            var Q35;
            Q35=sQuery(id+"F6.wireOp",EDGE,"E2575");
            var Q36;
            Q36=sQuery(id+"F6.wireOp",EDGE,"E2580");
            var Q37;
            Q37=sQuery(id+"F6.wireOp",EDGE,"E2579");
            var Q38;
            Q38=sQuery(id+"F6.wireOp",EDGE,"E2578");
            var Q39;
            Q39=sQuery(id+"F6.wireOp",EDGE,"E2601");
            var Q40;
            Q40=sQuery(id+"F6.wireOp",EDGE,"E2600");
            extrude(context, id + "F7", {"entities" : qUnion([Q0]), "surfaceEntities" : qUnion([Q1, Q2, Q3, Q4, Q5, Q6, Q7, Q8, Q9, Q10, Q11, Q12, Q13, Q14, Q15, Q16, Q17, Q18, Q19, Q20, Q21, Q22, Q23, Q24, Q25, Q26, Q27, Q28, Q29, Q30, Q31, Q32, Q33, Q34, Q35, Q36, Q37, Q38, Q39, Q40]), "depth" : 3.8 * mm, "offsetDistance" : 25.4 * mm});
        }
        {
            var Q0;
            Q0=qCreatedBy(makeId("Top.planeOp"),FACE);
            var sketch = newSketch(context, id + "F8", { "sketchPlane" : qUnion([Q0])});
            skLineSegment(sketch, "E2602", {"start": v(28.42, 9.16) * mm, "end": v(26.93, 14) * mm});
            skLineSegment(sketch, "E2603", {"start": v(26.93, 14) * mm, "end": v(25.48, 16.64) * mm});
            skLineSegment(sketch, "E2604", {"start": v(25.48, 16.64) * mm, "end": v(24.83, 17.43) * mm});
            skLineSegment(sketch, "E2605", {"start": v(24.83, 17.43) * mm, "end": v(24.83, 17.74) * mm});
            skLineSegment(sketch, "E2606", {"start": v(24.83, 17.74) * mm, "end": v(24.83, 18.05) * mm});
            skLineSegment(sketch, "E2607", {"start": v(24.83, 18.05) * mm, "end": v(24.83, 18.35) * mm});
            skLineSegment(sketch, "E2608", {"start": v(24.83, 18.35) * mm, "end": v(24.83, 18.66) * mm});
            skLineSegment(sketch, "E2609", {"start": v(24.83, 18.66) * mm, "end": v(22.88, 20.86) * mm});
            skLineSegment(sketch, "E2610", {"start": v(22.88, 20.86) * mm, "end": v(19.48, 21.33) * mm});
            skLineSegment(sketch, "E2611", {"start": v(19.48, 21.33) * mm, "end": v(16.26, 20.95) * mm});
            skLineSegment(sketch, "E2612", {"start": v(16.26, 20.95) * mm, "end": v(14.82, 20.63) * mm});
            skLineSegment(sketch, "E2613", {"start": v(14.82, 20.63) * mm, "end": v(14.81, 21.36) * mm});
            skLineSegment(sketch, "E2614", {"start": v(14.81, 21.36) * mm, "end": v(14.7, 22.3) * mm});
            skLineSegment(sketch, "E2615", {"start": v(14.7, 22.3) * mm, "end": v(14.34, 23.3) * mm});
            skLineSegment(sketch, "E2616", {"start": v(14.34, 23.3) * mm, "end": v(13.61, 24.13) * mm});
            skLineSegment(sketch, "E2617", {"start": v(13.61, 24.13) * mm, "end": v(12.45, 24.55) * mm});
            skLineSegment(sketch, "E2618", {"start": v(12.45, 24.55) * mm, "end": v(10.94, 24.5) * mm});
            skLineSegment(sketch, "E2619", {"start": v(10.94, 24.5) * mm, "end": v(9.14, 24.1) * mm});
            skLineSegment(sketch, "E2620", {"start": v(9.14, 24.1) * mm, "end": v(7.14, 23.5) * mm});
            skLineSegment(sketch, "E2621", {"start": v(7.14, 23.5) * mm, "end": v(5, 23.2) * mm});
            skLineSegment(sketch, "E2622", {"start": v(5, 23.2) * mm, "end": v(3.04, 23.34) * mm});
            skLineSegment(sketch, "E2623", {"start": v(3.04, 23.34) * mm, "end": v(1.59, 23.65) * mm});
            skLineSegment(sketch, "E2624", {"start": v(1.59, 23.65) * mm, "end": v(1.03, 23.82) * mm});
            skLineSegment(sketch, "E2625", {"start": v(1.03, 23.82) * mm, "end": v(0.77, 24.44) * mm});
            skLineSegment(sketch, "E2626", {"start": v(0.77, 24.44) * mm, "end": v(0.51, 25.06) * mm});
            skLineSegment(sketch, "E2627", {"start": v(0.51, 25.06) * mm, "end": v(0.26, 25.68) * mm});
            skLineSegment(sketch, "E2628", {"start": v(0.26, 25.68) * mm, "end": v(0, 26.3) * mm});
            skLineSegment(sketch, "E2629", {"start": v(0, 26.3) * mm, "end": v(-0.26, 25.68) * mm});
            skLineSegment(sketch, "E2630", {"start": v(-0.26, 25.68) * mm, "end": v(-0.51, 25.06) * mm});
            skLineSegment(sketch, "E2631", {"start": v(-0.51, 25.06) * mm, "end": v(-0.77, 24.44) * mm});
            skLineSegment(sketch, "E2632", {"start": v(-0.77, 24.44) * mm, "end": v(-1.03, 23.82) * mm});
            skLineSegment(sketch, "E2633", {"start": v(-1.03, 23.82) * mm, "end": v(-1.59, 23.65) * mm});
            skLineSegment(sketch, "E2634", {"start": v(-1.59, 23.65) * mm, "end": v(-3.04, 23.34) * mm});
            skLineSegment(sketch, "E2635", {"start": v(-3.04, 23.34) * mm, "end": v(-5, 23.2) * mm});
            skLineSegment(sketch, "E2636", {"start": v(-5, 23.2) * mm, "end": v(-7.14, 23.5) * mm});
            skLineSegment(sketch, "E2637", {"start": v(-7.14, 23.5) * mm, "end": v(-9.14, 24.1) * mm});
            skLineSegment(sketch, "E2638", {"start": v(-9.14, 24.1) * mm, "end": v(-10.94, 24.5) * mm});
            skLineSegment(sketch, "E2639", {"start": v(-10.94, 24.5) * mm, "end": v(-12.46, 24.55) * mm});
            skLineSegment(sketch, "E2640", {"start": v(-12.46, 24.55) * mm, "end": v(-13.61, 24.13) * mm});
            skLineSegment(sketch, "E2641", {"start": v(-13.61, 24.13) * mm, "end": v(-14.34, 23.3) * mm});
            skLineSegment(sketch, "E2642", {"start": v(-14.34, 23.3) * mm, "end": v(-14.7, 22.3) * mm});
            skLineSegment(sketch, "E2643", {"start": v(-14.7, 22.3) * mm, "end": v(-14.82, 21.36) * mm});
            skLineSegment(sketch, "E2644", {"start": v(-14.82, 21.36) * mm, "end": v(-14.83, 20.63) * mm});
            skLineSegment(sketch, "E2645", {"start": v(-14.83, 20.63) * mm, "end": v(-16.26, 20.95) * mm});
            skLineSegment(sketch, "E2646", {"start": v(-16.26, 20.95) * mm, "end": v(-19.48, 21.33) * mm});
            skLineSegment(sketch, "E2647", {"start": v(-19.48, 21.33) * mm, "end": v(-22.88, 20.86) * mm});
            skLineSegment(sketch, "E2648", {"start": v(-22.88, 20.86) * mm, "end": v(-24.83, 18.66) * mm});
            skLineSegment(sketch, "E2649", {"start": v(-24.83, 18.66) * mm, "end": v(-24.83, 18.35) * mm});
            skLineSegment(sketch, "E2650", {"start": v(-24.83, 18.35) * mm, "end": v(-24.83, 18.05) * mm});
            skLineSegment(sketch, "E2651", {"start": v(-24.83, 18.05) * mm, "end": v(-24.83, 17.74) * mm});
            skLineSegment(sketch, "E2652", {"start": v(-24.83, 17.74) * mm, "end": v(-24.83, 17.43) * mm});
            skLineSegment(sketch, "E2653", {"start": v(-24.83, 17.43) * mm, "end": v(-25.48, 16.64) * mm});
            skLineSegment(sketch, "E2654", {"start": v(-25.48, 16.64) * mm, "end": v(-26.93, 14) * mm});
            skLineSegment(sketch, "E2655", {"start": v(-26.93, 14) * mm, "end": v(-28.42, 9.16) * mm});
            skLineSegment(sketch, "E2656", {"start": v(-28.42, 9.16) * mm, "end": v(-29.18, 1.76) * mm});
            skLineSegment(sketch, "E2657", {"start": v(-29.18, 1.76) * mm, "end": v(-26.88, -9.53) * mm});
            skLineSegment(sketch, "E2658", {"start": v(-26.88, -9.53) * mm, "end": v(-21.64, -22.9) * mm});
            skLineSegment(sketch, "E2659", {"start": v(-16.37, -34.06) * mm, "end": v(-13.97, -38.73) * mm});
            skLineSegment(sketch, "E2660", {"start": v(-13.97, -38.73) * mm, "end": v(-13.84, -39.4) * mm});
            skLineSegment(sketch, "E2661", {"start": v(-13.84, -39.4) * mm, "end": v(-13.43, -40.87) * mm});
            skLineSegment(sketch, "E2662", {"start": v(-13.43, -40.87) * mm, "end": v(-12.71, -42.4) * mm});
            skLineSegment(sketch, "E2663", {"start": v(-12.71, -42.4) * mm, "end": v(-11.65, -43.24) * mm});
            skLineSegment(sketch, "E2664", {"start": v(-11.65, -43.24) * mm, "end": v(-10.49, -43.38) * mm});
            skLineSegment(sketch, "E2665", {"start": v(-10.49, -43.38) * mm, "end": v(-9.54, -43.36) * mm});
            skLineSegment(sketch, "E2666", {"start": v(-9.54, -43.36) * mm, "end": v(-8.9, -43.29) * mm});
            skLineSegment(sketch, "E2667", {"start": v(-8.9, -43.29) * mm, "end": v(-8.67, -43.24) * mm});
            skLineSegment(sketch, "E2668", {"start": v(-8.67, -43.24) * mm, "end": v(-8.53, -43.44) * mm});
            skLineSegment(sketch, "E2669", {"start": v(-8.53, -43.44) * mm, "end": v(-8, -43.87) * mm});
            skLineSegment(sketch, "E2670", {"start": v(-8, -43.87) * mm, "end": v(-6.93, -44.25) * mm});
            skLineSegment(sketch, "E2671", {"start": v(-6.93, -44.25) * mm, "end": v(-5.14, -44.3) * mm});
            skLineSegment(sketch, "E2672", {"start": v(-5.14, -44.3) * mm, "end": v(-4.95, -44.36) * mm});
            skLineSegment(sketch, "E2673", {"start": v(-4.95, -44.36) * mm, "end": v(-4.43, -44.46) * mm});
            skLineSegment(sketch, "E2674", {"start": v(-4.43, -44.46) * mm, "end": v(-3.67, -44.49) * mm});
            skLineSegment(sketch, "E2675", {"start": v(-3.67, -44.49) * mm, "end": v(-2.72, -44.34) * mm});
            skLineSegment(sketch, "E2676", {"start": v(-2.72, -44.34) * mm, "end": v(-2.39, -44.4) * mm});
            skLineSegment(sketch, "E2677", {"start": v(-2.39, -44.4) * mm, "end": v(-1.6, -44.52) * mm});
            skLineSegment(sketch, "E2678", {"start": v(-1.6, -44.52) * mm, "end": v(-0.7, -44.58) * mm});
            skLineSegment(sketch, "E2679", {"start": v(-0.7, -44.58) * mm, "end": v(0, -44.5) * mm});
            skLineSegment(sketch, "E2680", {"start": v(16.37, -34.06) * mm, "end": v(21.64, -22.9) * mm});
            skLineSegment(sketch, "E2681", {"start": v(21.64, -22.9) * mm, "end": v(26.88, -9.53) * mm});
            skLineSegment(sketch, "E2682", {"start": v(26.88, -9.53) * mm, "end": v(29.18, 1.76) * mm});
            skLineSegment(sketch, "E2683", {"start": v(29.18, 1.76) * mm, "end": v(28.42, 9.16) * mm});
            skLineSegment(sketch, "E2684", {"start": v(-16.37, -34.06) * mm, "end": v(-16.37, -45.16) * mm});
            skLineSegment(sketch, "E2685", {"start": v(-16.37, -45.16) * mm, "end": v(-14.27, -46.55) * mm});
            skLineSegment(sketch, "E2686", {"start": v(-14.27, -46.55) * mm, "end": v(-14.17, -46.39) * mm});
            skLineSegment(sketch, "E2687", {"start": v(-14.17, -46.39) * mm, "end": v(-13.07, -47.12) * mm});
            skLineSegment(sketch, "E2688", {"start": v(-13.07, -47.12) * mm, "end": v(-10.09, -48.65) * mm});
            skLineSegment(sketch, "E2689", {"start": v(-10.09, -48.65) * mm, "end": v(-7.05, -49.88) * mm});
            skLineSegment(sketch, "E2690", {"start": v(-7.05, -49.88) * mm, "end": v(-4.46, -50.66) * mm});
            skLineSegment(sketch, "E2691", {"start": v(-4.46, -50.66) * mm, "end": v(-2.5, -51.13) * mm});
            skLineSegment(sketch, "E2692", {"start": v(-2.5, -51.13) * mm, "end": v(-0.68, -51.33) * mm});
            skLineSegment(sketch, "E2693", {"start": v(-0.68, -51.33) * mm, "end": v(0, -51.33) * mm});
            skLineSegment(sketch, "E2694", {"start": v(0, -51.33) * mm, "end": v(0, -44.5) * mm});
            skLineSegment(sketch, "E2695.MirrorCS", {"start": v(4.95, -44.36) * mm, "end": v(4.43, -44.46) * mm});
            skLineSegment(sketch, "E2696.MirrorCS", {"start": v(4.43, -44.46) * mm, "end": v(3.66, -44.49) * mm});
            skLineSegment(sketch, "E2697.MirrorCS", {"start": v(8.67, -43.24) * mm, "end": v(8.53, -43.44) * mm});
            skLineSegment(sketch, "E2698.MirrorCS", {"start": v(2.72, -44.34) * mm, "end": v(2.39, -44.4) * mm});
            skLineSegment(sketch, "E2699.MirrorCS", {"start": v(13.96, -38.73) * mm, "end": v(13.84, -39.4) * mm});
            skLineSegment(sketch, "E2700.MirrorCS", {"start": v(3.66, -44.49) * mm, "end": v(2.72, -44.34) * mm});
            skLineSegment(sketch, "E2701.MirrorCS", {"start": v(0.68, -51.33) * mm, "end": v(0, -51.33) * mm});
            skLineSegment(sketch, "E2702.MirrorCS", {"start": v(14.27, -46.55) * mm, "end": v(14.17, -46.39) * mm});
            skLineSegment(sketch, "E2703.MirrorCS", {"start": v(9.54, -43.36) * mm, "end": v(8.9, -43.29) * mm});
            skLineSegment(sketch, "E2704.MirrorCS", {"start": v(10.49, -43.38) * mm, "end": v(9.54, -43.36) * mm});
            skLineSegment(sketch, "E2705.MirrorCS", {"start": v(14.17, -46.39) * mm, "end": v(13.07, -47.12) * mm});
            skLineSegment(sketch, "E2706.MirrorCS", {"start": v(11.65, -43.24) * mm, "end": v(10.49, -43.38) * mm});
            skLineSegment(sketch, "E2707.MirrorCS", {"start": v(5.14, -44.3) * mm, "end": v(4.95, -44.36) * mm});
            skLineSegment(sketch, "E2708.MirrorCS", {"start": v(8.9, -43.29) * mm, "end": v(8.67, -43.24) * mm});
            skLineSegment(sketch, "E2709.MirrorCS", {"start": v(2.39, -44.4) * mm, "end": v(1.6, -44.52) * mm});
            skLineSegment(sketch, "E2710.MirrorCS", {"start": v(8.53, -43.44) * mm, "end": v(8, -43.87) * mm});
            skLineSegment(sketch, "E2711.MirrorCS", {"start": v(12.71, -42.4) * mm, "end": v(11.65, -43.24) * mm});
            skLineSegment(sketch, "E2712.MirrorCS", {"start": v(8, -43.87) * mm, "end": v(6.92, -44.25) * mm});
            skLineSegment(sketch, "E2713.MirrorCS", {"start": v(0.7, -44.58) * mm, "end": v(0, -44.5) * mm});
            skLineSegment(sketch, "E2714.MirrorCS", {"start": v(1.6, -44.52) * mm, "end": v(0.7, -44.58) * mm});
            skLineSegment(sketch, "E2715.MirrorCS", {"start": v(13.84, -39.4) * mm, "end": v(13.43, -40.87) * mm});
            skLineSegment(sketch, "E2716.MirrorCS", {"start": v(4.46, -50.66) * mm, "end": v(2.5, -51.13) * mm});
            skLineSegment(sketch, "E2717.MirrorCS", {"start": v(2.5, -51.13) * mm, "end": v(0.68, -51.33) * mm});
            skLineSegment(sketch, "E2718.MirrorCS", {"start": v(16.37, -34.06) * mm, "end": v(13.96, -38.73) * mm});
            skLineSegment(sketch, "E2719.MirrorCS", {"start": v(16.37, -45.16) * mm, "end": v(14.27, -46.55) * mm});
            skLineSegment(sketch, "E2720.MirrorCS", {"start": v(13.43, -40.87) * mm, "end": v(12.71, -42.4) * mm});
            skLineSegment(sketch, "E2721.MirrorCS", {"start": v(13.07, -47.12) * mm, "end": v(10.09, -48.65) * mm});
            skLineSegment(sketch, "E2722.MirrorCS", {"start": v(6.92, -44.25) * mm, "end": v(5.14, -44.3) * mm});
            skLineSegment(sketch, "E2723.MirrorCS", {"start": v(10.09, -48.65) * mm, "end": v(7.05, -49.88) * mm});
            skLineSegment(sketch, "E2724.MirrorCS", {"start": v(16.37, -34.06) * mm, "end": v(16.37, -45.16) * mm});
            skLineSegment(sketch, "E2725.MirrorCS", {"start": v(7.05, -49.88) * mm, "end": v(4.46, -50.66) * mm});
            skSolve(sketch);
        }
        {
            var Q0;
            Q0 = qSketchRegion(id + "F8", true);
            extrude(context, id + "F9", {"entities" : qUnion([Q0]), "depth" : 3.8 * mm, "offsetDistance" : 25.4 * mm});
        }
    });
